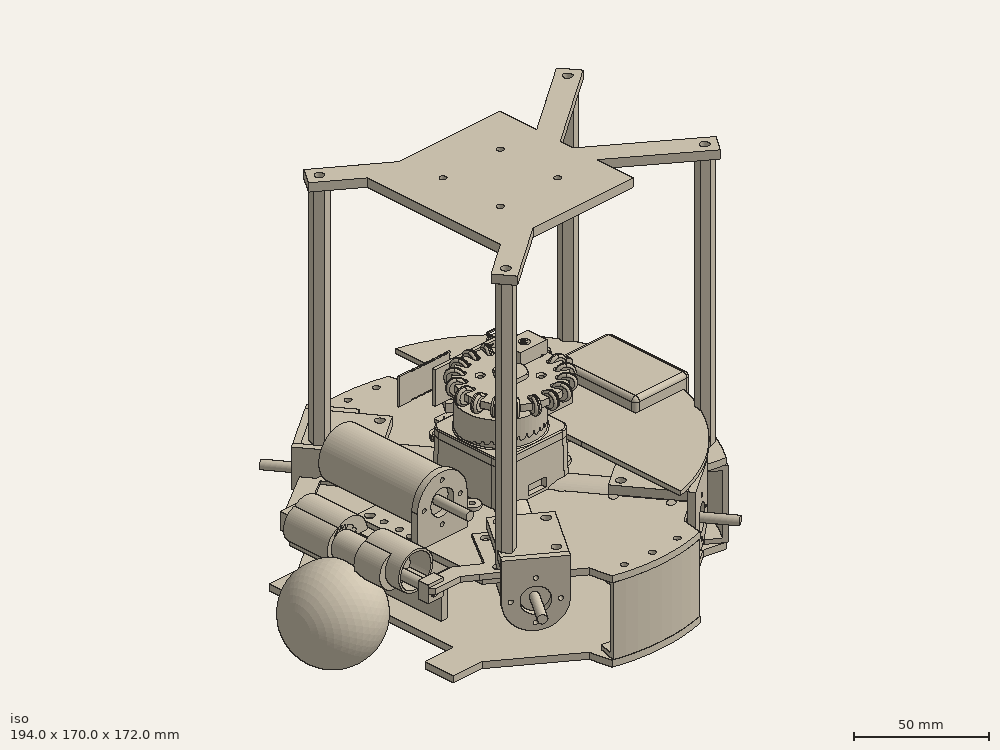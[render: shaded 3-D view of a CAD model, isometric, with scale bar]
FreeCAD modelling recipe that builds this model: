
FCSTD DOCUMENT  (FreeCAD 1.0R39109 (Git))
Label: SN_model_2025
License: All rights reserved
LicenseURL: https://en.wikipedia.org/wiki/All_rights_reserved
objects: Part::Feature×311, Sketcher::SketchObject×77, App::Part×52, PartDesign::Pad×50, PartDesign::Pocket×47, PartDesign::Body×32, PartDesign::SubShapeBinder×27, PartDesign::PolarPattern×11, PartDesign::Revolution×4, Part::FeaturePython×2, Part::Sphere×1, PartDesign::Fillet×1, Part::Cylinder×1, Part::Cut×1
note: 857 computed .brp shape members not serialized (recipe doc carries the construction recipe); baked Part::Feature solids carry a one-line shape summary decoded from their .brp

FEATURE [Sketcher::SketchObject] Sketch
  ArcFitTolerance = 0
  AttachmentSupport = -> [XY_Plane008]
  FullyConstrained = true
  MakeInternals = false
  MapMode = 5
  sketch-geometry (1):
    g0: Circle CenterX=0 CenterY=0 CenterZ=0 NormalX=0 NormalY=0 NormalZ=1 AngleXU=0 Radius=85
  constraints (2):
    c: Coincident(g0,g-1)
    c: Diameter(g0) = 170
FEATURE [Sketcher::SketchObject] Sketch005
  ArcFitTolerance = 0
  AttachmentSupport = -> [XZ_Plane009]
  FullyConstrained = true
  MakeInternals = false
  MapMode = 5
  Placement = pos=(0,0,0) rot=(1,0,0;1.5708rad)
  sketch-geometry (6):
    g0: ArcOfHyperbola CenterX=0 CenterY=94.5 CenterZ=0 NormalX=0 NormalY=0 NormalZ=1 MajorRadius=17.5 MinorRadius=15.6742 AngleXU=1.5708 StartAngle=0 EndAngle=1.02375
    g1: LineSegment [constr] StartX=5e-16 StartY=112 StartZ=0 EndX=-5e-16 EndY=77 EndZ=0
    g2: LineSegment [constr] StartX=-15.6742 StartY=112 StartZ=0 EndX=15.6742 EndY=112 EndZ=0
    g3: GeomPoint [constr] X=2.6e-15 Y=117.993 Z=0
    g4: LineSegment StartX=-19 StartY=122 StartZ=0 EndX=0 EndY=122 EndZ=0
    g5: LineSegment StartX=0 StartY=112 StartZ=0 EndX=0 EndY=122 EndZ=0
  constraints (15):
    c: InternalAlignment(g1,g0)
    c: InternalAlignment(g2,g0)
    c: InternalAlignment(g3,g0)
    c: Horizontal(g2)
    c: PointOnObject(g0,g-2)
    c: PointOnObject(g0,g-2)
    c: DistanceY(g0,g0) = 10
    c: DistanceX(g0,g0) = 19
    c: DistanceY(g1,g0) = 35
    c: Coincident(g4,g0)
    c: Coincident(g5,g0)
    c: Coincident(g5,g4)
    c: Vertical(g5)
    c: Horizontal(g4)
    c: DistanceY(g-1,g0) = 112
FEATURE [PartDesign::Pad] Pad  label="Structural layer"
  Direction = (0,0,1)
  Length = 3
  Length2 = 10
  Profile = -> Sketch
  ReferenceAxis = -> Sketch [N_Axis]
  Suppressed = false
  Type = 0
FEATURE [Sketcher::SketchObject] Sketch001
  ArcFitTolerance = 0
  AttachmentSupport = -> [Pad]
  ExternalGeometry = -> [Pad]
  FullyConstrained = false
  MakeInternals = false
  MapMode = 5
  Placement = pos=(0,0,3) rot=(0,0,1;0rad)
  sketch-geometry (7):
    g0: LineSegment StartX=-10.6686 StartY=100.741 StartZ=0 EndX=44.4806 EndY=91.0164 EndZ=0
    g1: LineSegment StartX=44.4806 StartY=91.0164 StartZ=0 EndX=41.5109 EndY=74.1744 EndZ=0
    g2: LineSegment StartX=32.942 StartY=68.1744 StartZ=0 EndX=-7.63834 EndY=75.3298 EndZ=0
    g3: LineSegment StartX=-13.6383 StartY=83.8987 StartZ=0 EndX=-10.6686 EndY=100.741 EndZ=0
    g4: LineSegment StartX=32.942 StartY=68.1744 StartZ=0 EndX=41.5109 EndY=74.1744 EndZ=0
    g5: LineSegment StartX=-13.6383 StartY=83.8987 StartZ=0 EndX=-7.63834 EndY=75.3298 EndZ=0
    g6: LineSegment [constr] StartX=-98.5042 StartY=90.5189 StartZ=0 EndX=89.0462 EndY=57.4487 EndZ=0
  constraints (18):
    c: Coincident(g0,g1)
    c: Coincident(g3,g0)
    c: Coincident(g4,g2)
    c: Coincident(g4,g1)
    c: Coincident(g5,g3)
    c: Coincident(g5,g2)
    c: Angle(g4,g2) = 2.35619
    c: Angle(g2,g5) = 2.35619
    c: DistanceX(g3,g2) = 6
    c: Angle(g6,g-1) = 0.174533
    c: Parallel(g2,g6)
    c: Parallel(g0,g2)
    c: Perpendicular(g6,g1)
    c: Equal(g1,g3)
    c: Parallel(g1,g3)
    c: PointOnObject(g3,g-3)
    c: PointOnObject(g1,g-3)
    c: Distance(g0) = 56
FEATURE [PartDesign::Pocket] Pocket
  BaseFeature = -> Pad
  Direction = (0,0,-1)
  Length = 5
  Length2 = 5
  Profile = -> Sketch001
  ReferenceAxis = -> Sketch001 [N_Axis]
  Suppressed = false
  Type = 1
FEATURE [PartDesign::PolarPattern] PolarPattern
  Angle = 110
  Axis = -> Sketch001 [N_Axis]
  BaseFeature = -> Pocket
  Mode = 0
  Occurrences = 2
  Offset = 120
  Originals = -> [Pocket]
  Suppressed = false
  TransformMode = 0
FEATURE [PartDesign::Revolution] Revolution
  Angle = 360
  Angle2 = 60
  Axis = (0,2e-16,1)
  Base = (0,0,0)
  Placement = pos=(0,0,0) rot=(1,0,0;1.5708rad)
  Profile = -> Sketch005
  ReferenceAxis = -> Sketch005 [V_Axis]
  Suppressed = false
  Type = 0
FEATURE [Sketcher::SketchObject] Sketch015
  ArcFitTolerance = 0
  AttachmentSupport = -> [PolarPattern]
  FullyConstrained = true
  MakeInternals = false
  MapMode = 5
  Placement = pos=(0,0,3) rot=(0,0,1;0rad)
  sketch-geometry (4):
    g0: LineSegment StartX=-111 StartY=31 StartZ=0 EndX=-31 EndY=111 EndZ=0
    g1: LineSegment StartX=-31 StartY=111 StartZ=0 EndX=-1 EndY=81 EndZ=0
    g2: LineSegment StartX=-1 StartY=81 StartZ=0 EndX=-81 EndY=1 EndZ=0
    g3: LineSegment StartX=-81 StartY=1 StartZ=0 EndX=-111 EndY=31 EndZ=0
  constraints (12):
    c: Coincident(g0,g1)
    c: Coincident(g1,g2)
    c: Coincident(g2,g3)
    c: Coincident(g3,g0)
    c: Equal(g3,g1)
    c: Equal(g0,g2)
    c: Angle(g3,g0) = 1.5708
    c: DistanceX(g2,g-1) = 81
    c: DistanceY(g-1,g1) = 81
    c: DistanceX(g0,g1) = 30
    c: DistanceX(g2,g1) = 80
    c: Angle(g-1,g2) = 0.785398
FEATURE [PartDesign::Pocket] Pocket004
  BaseFeature = -> PolarPattern
  Direction = (0,0,-1)
  Length = 5
  Length2 = 5
  Profile = -> Sketch015
  ReferenceAxis = -> Sketch015 [N_Axis]
  Suppressed = false
  Type = 1
FEATURE [Sketcher::SketchObject] Sketch016
  ArcFitTolerance = 0
  AttachmentSupport = -> [XZ_Plane016]
  FullyConstrained = true
  MakeInternals = false
  MapMode = 5
  Placement = pos=(0,0,0) rot=(1,0,0;1.5708rad)
  sketch-geometry (8):
    g0: LineSegment StartX=-88 StartY=-1 StartZ=0 EndX=-79 EndY=-1 EndZ=0
    g1: LineSegment StartX=-79 StartY=-34 StartZ=0 EndX=-88 EndY=-34 EndZ=0
    g2: LineSegment StartX=-88 StartY=-34 StartZ=0 EndX=-88 EndY=-1 EndZ=0
    g3: LineSegment StartX=-79 StartY=-1 StartZ=0 EndX=-79 EndY=-3 EndZ=0
    g4: LineSegment StartX=-79 StartY=-3 StartZ=0 EndX=-86 EndY=-3 EndZ=0
    g5: LineSegment StartX=-86 StartY=-3 StartZ=0 EndX=-86 EndY=-32 EndZ=0
    g6: LineSegment StartX=-86 StartY=-32 StartZ=0 EndX=-79 EndY=-32 EndZ=0
    g7: LineSegment StartX=-79 StartY=-32 StartZ=0 EndX=-79 EndY=-34 EndZ=0
  constraints (24):
    c: Coincident(g1,g2)
    c: Coincident(g2,g0)
    c: Horizontal(g0)
    c: Horizontal(g1)
    c: Vertical(g2)
    c: DistanceY(g1,g0) = 33
    c: DistanceX(g1,g1) = 9
    c: DistanceX(g0,g-1) = 88
    c: DistanceY(g1,g-1) = 34
    c: Equal(g1,g0)
    c: Coincident(g3,g0)
    c: Vertical(g3)
    c: Coincident(g4,g3)
    c: Horizontal(g4)
    c: Coincident(g5,g4)
    c: Vertical(g5)
    c: Coincident(g6,g5)
    c: Horizontal(g6)
    c: Coincident(g7,g6)
    c: Coincident(g7,g1)
    c: Vertical(g7)
    c: Equal(g3,g7)
    c: DistanceY(g3,g3) = 2
    c: DistanceX(g0,g4) = 2
FEATURE [PartDesign::Revolution] Revolution001
  Angle = 30
  Angle2 = 60
  Axis = (1e-16,1e-16,1)
  Base = (0,0,0)
  Midplane = true
  Placement = pos=(0,0,0) rot=(1,0,0;1.5708rad)
  Profile = -> Sketch016
  ReferenceAxis = -> Z_Axis016
  Reversed = true
  Suppressed = false
  Type = 0
FEATURE [Part::Feature] Part__Feature268  label="OmniBase_Predeterminado004"
  Placement = pos=(4.80373,-0.638646,40.5) rot=(0,0,1;0rad)
  shape: bbox 44 x 43.9 x 9 mm, 104 faces (baked)
FEATURE [Part::Feature] Part__Feature269  label="Roller_Predeterminado072"
  Placement = pos=(4.80373,20.3614,41.6192) rot=(0,0,1;0rad)
  shape: bbox 2.6 x 8.659 x 8.659 mm, 10 faces (baked)
FEATURE [Part::Feature] Part__Feature270  label="Roller_Predeterminado073"
  Placement = pos=(-2.3787,19.0949,41.6192) rot=(0,0,1;0.349066rad)
  shape: bbox 4.664 x 8.342 x 8.659 mm, 10 faces (baked)
FEATURE [Part::Feature] Part__Feature271  label="Roller_Predeterminado074"
  Placement = pos=(-8.69481,15.4483,41.6192) rot=(0,0,1;0.698132rad)
  shape: bbox 6.71 x 7.451 x 8.659 mm, 10 faces (baked)
FEATURE [Part::Feature] Part__Feature272  label="Roller_Predeterminado075"
  Placement = pos=(-13.3828,9.86135,41.6192) rot=(0,0,1;1.0472rad)
  shape: bbox 7.965 x 5.765 x 8.659 mm, 10 faces (baked)
FEATURE [Part::Feature] Part__Feature273  label="Roller_Predeterminado076"
  Placement = pos=(-15.8772,3.00797,41.6192) rot=(0,0,1;1.39626rad)
  shape: bbox 8.632 x 3.688 x 8.659 mm, 10 faces (baked)
FEATURE [Part::Feature] Part__Feature274  label="Roller_Predeterminado077"
  Placement = pos=(-15.8772,-4.28526,41.6192) rot=(0,0,1;1.74533rad)
  shape: bbox 8.632 x 3.688 x 8.659 mm, 10 faces (baked)
FEATURE [Part::Feature] Part__Feature275  label="Roller_Predeterminado078"
  Placement = pos=(-13.3828,-11.1386,41.6192) rot=(0,0,1;2.0944rad)
  shape: bbox 7.965 x 5.765 x 8.659 mm, 10 faces (baked)
FEATURE [Part::Feature] Part__Feature276  label="Roller_Predeterminado079"
  Placement = pos=(-8.69481,-16.7256,41.6192) rot=(0,0,1;2.44346rad)
  shape: bbox 6.71 x 7.451 x 8.659 mm, 10 faces (baked)
FEATURE [Part::Feature] Part__Feature277  label="Roller_Predeterminado080"
  Placement = pos=(-2.3787,-20.3722,41.6192) rot=(0,0,1;2.79253rad)
  shape: bbox 4.664 x 8.342 x 8.659 mm, 10 faces (baked)
FEATURE [Part::Feature] Part__Feature278  label="Roller_Predeterminado081"
  Placement = pos=(4.80373,-21.6386,41.6192) rot=(0,0,1;3.14159rad)
  shape: bbox 2.6 x 8.659 x 8.659 mm, 10 faces (baked)
FEATURE [Part::Feature] Part__Feature279  label="Roller_Predeterminado082"
  Placement = pos=(11.9862,-20.3722,41.6192) rot=(0,0,1;3.49066rad)
  shape: bbox 4.664 x 8.342 x 8.659 mm, 10 faces (baked)
FEATURE [Part::Feature] Part__Feature280  label="Roller_Predeterminado083"
  Placement = pos=(18.3023,-16.7256,41.6192) rot=(0,0,1;3.83972rad)
  shape: bbox 6.71 x 7.451 x 8.659 mm, 10 faces (baked)
FEATURE [Part::Feature] Part__Feature281  label="Roller_Predeterminado084"
  Placement = pos=(22.9903,-11.1386,41.6192) rot=(0,0,-1;2.0944rad)
  shape: bbox 7.965 x 5.765 x 8.659 mm, 10 faces (baked)
FEATURE [Part::Feature] Part__Feature282  label="Roller_Predeterminado085"
  Placement = pos=(25.4847,-4.28526,41.6192) rot=(0,0,-1;1.74533rad)
  shape: bbox 8.632 x 3.688 x 8.659 mm, 10 faces (baked)
FEATURE [Part::Feature] Part__Feature283  label="Roller_Predeterminado086"
  Placement = pos=(25.4847,3.00797,41.6192) rot=(0,0,-1;1.39626rad)
  shape: bbox 8.632 x 3.688 x 8.659 mm, 10 faces (baked)
FEATURE [Part::Feature] Part__Feature284  label="Roller_Predeterminado087"
  Placement = pos=(22.9903,9.86135,41.6192) rot=(0,0,-1;1.0472rad)
  shape: bbox 7.965 x 5.765 x 8.659 mm, 10 faces (baked)
FEATURE [Part::Feature] Part__Feature285  label="Roller_Predeterminado088"
  Placement = pos=(18.3023,15.4483,41.6192) rot=(0,0,-1;0.698132rad)
  shape: bbox 6.71 x 7.451 x 8.659 mm, 10 faces (baked)
FEATURE [Part::Feature] Part__Feature286  label="Roller_Predeterminado089"
  Placement = pos=(11.9862,19.0949,41.6192) rot=(0,0,-1;0.349066rad)
  shape: bbox 4.664 x 8.342 x 8.659 mm, 10 faces (baked)
FEATURE [Part::Feature] Part__Feature287  label="Nut_Predeterminado004"
  Placement = pos=(4.80373,-0.638646,43.5) rot=(0,0,1;1.0472rad)
  shape: bbox 13.86 x 12.93 x 2 mm, 24 faces (baked)
FEATURE [App::Part] OmniWheel054  label="OmniWheel 1"
  Group = -> [Part__Feature268,Part__Feature269,Part__Feature270,Part__Feature271,Part__Feature272,Part__Feature273,Part__Feature274,Part__Feature275,Part__Feature276,Part__Feature277,Part__Feature278,Part__Feature279,Part__Feature280,Part__Feature281,Part__Feature282,Part__Feature283,Part__Feature284,Part__Feature285,Part__Feature286,Part__Feature287]
  Origin = -> Origin019
  Placement = pos=(-23.8855,35.1581,-6.8) rot=(-0.419215,-0.805305,-0.419215;1.78566rad)
FEATURE [Sketcher::SketchObject] Sketch023
  ArcFitTolerance = 0
  AttachmentSupport = -> [XY_Plane024]
  FullyConstrained = true
  MakeInternals = false
  MapMode = 5
  sketch-geometry (9):
    g0: Circle CenterX=0 CenterY=0 CenterZ=0 NormalX=0 NormalY=0 NormalZ=1 AngleXU=0 Radius=20
    g1: LineSegment StartX=27.7128 StartY=-4 StartZ=0 EndX=35.7128 EndY=-4 EndZ=0
    g2: LineSegment StartX=35.7128 StartY=-4 StartZ=0 EndX=35.7128 EndY=4 EndZ=0
    g3: LineSegment StartX=35.7128 StartY=4 StartZ=0 EndX=27.7128 EndY=4 EndZ=0
    g4: LineSegment StartX=-27.7128 StartY=-4 StartZ=0 EndX=-35.7128 EndY=-4 EndZ=0
    g5: LineSegment StartX=-35.7128 StartY=-4 StartZ=0 EndX=-35.7128 EndY=4 EndZ=0
    g6: LineSegment StartX=-35.7128 StartY=4 StartZ=0 EndX=-27.7128 EndY=4 EndZ=0
    g7: ArcOfCircle CenterX=0 CenterY=0 CenterZ=0 NormalX=0 NormalY=0 NormalZ=1 AngleXU=0 Radius=28 StartAngle=0.143348 EndAngle=2.99825
    g8: ArcOfCircle CenterX=0 CenterY=0 CenterZ=0 NormalX=0 NormalY=0 NormalZ=1 AngleXU=0 Radius=28 StartAngle=3.28494 EndAngle=6.13984
  constraints (25):
    c: Coincident(g0,g-1)
    c: Diameter(g0) = 40
    c: Horizontal(g1)
    c: Coincident(g2,g1)
    c: Coincident(g3,g2)
    c: Horizontal(g3)
    c: Horizontal(g4)
    c: Coincident(g5,g4)
    c: Vertical(g5)
    c: Coincident(g6,g5)
    c: Horizontal(g6)
    c: Coincident(g7,g0)
    c: Coincident(g7,g6)
    c: Coincident(g7,g3)
    c: Coincident(g8,g0)
    c: Coincident(g8,g4)
    c: Coincident(g8,g1)
    c: Diameter(g7) = 56
    c: Diameter(g8) = 56
    c: Symmetric(g1,g2,g-1)
    c: Equal(g5,g2)
    c: Equal(g6,g3)
    c: Equal(g4,g1)
    c: DistanceY(g2,g2) = 8
    c: DistanceX(g6,g6) = 8
FEATURE [PartDesign::Pad] Pad007
  Direction = (0,0,1)
  Length = 3
  Length2 = 10
  Profile = -> Sketch023
  ReferenceAxis = -> Sketch023 [N_Axis]
  Suppressed = false
  Type = 0
FEATURE [Sketcher::SketchObject] Sketch025
  ArcFitTolerance = 0
  AttachmentSupport = -> [XY_Plane026]
  FullyConstrained = true
  MakeInternals = false
  MapMode = 5
  sketch-geometry (2):
    g0: Circle CenterX=0 CenterY=0 CenterZ=0 NormalX=0 NormalY=0 NormalZ=1 AngleXU=0 Radius=90
    g1: Circle CenterX=0 CenterY=0 CenterZ=0 NormalX=0 NormalY=0 NormalZ=1 AngleXU=0 Radius=95
  constraints (4):
    c: Diameter(g0) = 180
    c: Coincident(g1,g-1)
    c: Diameter(g1) = 190
    c: Coincident(g0,g-1)
FEATURE [PartDesign::Pad] Pad008
  Direction = (0,0,1)
  Length = 180
  Length2 = 10
  Profile = -> Sketch025
  ReferenceAxis = -> Sketch025 [N_Axis]
  Suppressed = false
  Type = 0
FEATURE [PartDesign::Body] Body008  label="Cylinder"
  AllowCompound = false
  Group = -> [Sketch025,Pad008]
  Origin = -> Origin026
  Placement = pos=(0,0,-44) rot=(0,0,1;0rad)
  Tip = -> Pad008
FEATURE [Sketcher::SketchObject] Sketch061
  ArcFitTolerance = 0
  FullyConstrained = true
  MakeInternals = false
  MapMode = 5
  Placement = pos=(0,0,2) rot=(0,0,1;0rad)
  sketch-geometry (1):
    g0: Circle CenterX=0 CenterY=0 CenterZ=0 NormalX=0 NormalY=0 NormalZ=1 AngleXU=0 Radius=12.5
  constraints (2):
    c: Coincident(g0,g-1)
    c: Diameter(g0) = 25
FEATURE [PartDesign::Pocket] Pocket019
  BaseFeature = -> Pocket004
  Direction = (0,0,-1)
  Length = 5
  Length2 = 5
  Profile = -> Sketch061
  ReferenceAxis = -> Sketch061 [N_Axis]
  Suppressed = false
  Type = 4
FEATURE [Part::Feature] Part__Feature439  label="114-00841-68--3DModel-STEP-56544 v1"
  Placement = pos=(24.0935,-0.00012972,0.814608) rot=(0.57735,0.57735,0.57735;2.0944rad)
  shape: bbox 11.35 x 11.95 x 1.68 mm, 239 faces (baked)
FEATURE [Part::Feature] Part__Feature453  label="MIMXRT1052CVJ5B v1"
  Placement = pos=(1.30183,-0.0809243,0.815) rot=(0,0.707107,0.707107;3.14159rad)
  shape: bbox 12 x 12 x 1.27 mm, 6 faces (baked)
FEATURE [App::Part] MIMXRT1052CVJ5B_v1  label="MIMXRT1052CVJ5B v198"
  Group = -> [Part__Feature453]
  Origin = -> Origin053
FEATURE [Part::Feature] Part__Feature589  label="MicroUSB Molex 473460001 v1"
  Placement = pos=(-28.9499,0.13174,2.07033) rot=(0.57735,-0.57735,-0.57735;2.0944rad)
  shape: bbox 5.43 x 7.98 x 2.94 mm, 406 faces (baked)
FEATURE [Part::Feature] Part__Feature590  label="COMPOUND"
  shape: bbox 2.54 x 2.54 x 2.799 mm, 22 faces, 0 solids (baked)
FEATURE [Part::Feature] Part__Feature591  label="COMPOUND001"
  shape: bbox 2.54 x 2.54 x 2.799 mm, 22 faces, 0 solids (baked)
FEATURE [Part::Feature] Part__Feature592  label="COMPOUND002"
  shape: bbox 2.54 x 2.54 x 2.799 mm, 23 faces, 0 solids (baked)
FEATURE [Part::Feature] Part__Feature593  label="COMPOUND003"
  shape: bbox 2.54 x 2.54 x 2.799 mm, 22 faces, 0 solids (baked)
FEATURE [Part::Feature] Part__Feature594  label="COMPOUND004"
  shape: bbox 2.54 x 2.54 x 2.799 mm, 22 faces, 0 solids (baked)
FEATURE [Part::Feature] Part__Feature595  label="COMPOUND005"
  shape: bbox 2.54 x 2.54 x 2.799 mm, 23 faces, 0 solids (baked)
FEATURE [App::Part] COMPOUND  label="COMPOUND006"
  Group = -> [Part__Feature590,Part__Feature591,Part__Feature592,Part__Feature593,Part__Feature594,Part__Feature595]
  Origin = -> Origin055
FEATURE [Part::Feature] Part__Feature596  label="COMPOUND007"
  shape: bbox 0.6304 x 0.63 x 12.7 mm, 14 faces (baked)
FEATURE [Part::Feature] Part__Feature597  label="COMPOUND008"
  shape: bbox 0.6304 x 0.63 x 12.7 mm, 14 faces (baked)
FEATURE [Part::Feature] Part__Feature598  label="COMPOUND009"
  shape: bbox 0.6304 x 0.63 x 12.7 mm, 14 faces (baked)
FEATURE [Part::Feature] Part__Feature599  label="COMPOUND010"
  shape: bbox 0.6304 x 0.63 x 12.7 mm, 14 faces (baked)
FEATURE [Part::Feature] Part__Feature600  label="COMPOUND011"
  shape: bbox 0.6304 x 0.63 x 12.7 mm, 14 faces (baked)
FEATURE [Part::Feature] Part__Feature601  label="COMPOUND012"
  shape: bbox 0.6304 x 0.63 x 12.7 mm, 14 faces (baked)
FEATURE [App::Part] COMPOUND001  label="COMPOUND013"
  Group = -> [Part__Feature596,Part__Feature597,Part__Feature598,Part__Feature599,Part__Feature600,Part__Feature601]
  Origin = -> Origin056
FEATURE [App::Part] Pin_Header_1x6_TH_Pitch_2_54mm_v1  label="Pin Header 1x6 TH Pitch 2.54mm v1"
  Group = -> [COMPOUND,COMPOUND001]
  Origin = -> Origin054
  Placement = pos=(-16.51,-7.62,-0.814) rot=(0,1,0;3.14159rad)
FEATURE [Part::Feature] Part__Feature602  label="COMPOUND014"
  shape: bbox 2.54 x 2.54 x 2.799 mm, 22 faces, 0 solids (baked)
FEATURE [Part::Feature] Part__Feature603  label="COMPOUND015"
  shape: bbox 2.54 x 2.54 x 2.799 mm, 22 faces, 0 solids (baked)
FEATURE [Part::Feature] Part__Feature604  label="COMPOUND016"
  shape: bbox 2.54 x 2.54 x 2.799 mm, 23 faces, 0 solids (baked)
FEATURE [Part::Feature] Part__Feature605  label="COMPOUND017"
  shape: bbox 2.54 x 2.54 x 2.799 mm, 22 faces, 0 solids (baked)
FEATURE [Part::Feature] Part__Feature606  label="COMPOUND018"
  shape: bbox 2.54 x 2.54 x 2.799 mm, 22 faces, 0 solids (baked)
FEATURE [Part::Feature] Part__Feature607  label="COMPOUND019"
  shape: bbox 2.54 x 2.54 x 2.799 mm, 23 faces, 0 solids (baked)
FEATURE [App::Part] COMPOUND002  label="COMPOUND020"
  Group = -> [Part__Feature602,Part__Feature603,Part__Feature604,Part__Feature605,Part__Feature606,Part__Feature607]
  Origin = -> Origin058
FEATURE [Part::Feature] Part__Feature608  label="COMPOUND021"
  shape: bbox 0.6304 x 0.63 x 12.7 mm, 14 faces (baked)
FEATURE [Part::Feature] Part__Feature609  label="COMPOUND022"
  shape: bbox 0.6304 x 0.63 x 12.7 mm, 14 faces (baked)
FEATURE [Part::Feature] Part__Feature610  label="COMPOUND023"
  shape: bbox 0.6304 x 0.63 x 12.7 mm, 14 faces (baked)
FEATURE [Part::Feature] Part__Feature611  label="COMPOUND024"
  shape: bbox 0.6304 x 0.63 x 12.7 mm, 14 faces (baked)
FEATURE [Part::Feature] Part__Feature612  label="COMPOUND025"
  shape: bbox 0.6304 x 0.63 x 12.7 mm, 14 faces (baked)
FEATURE [Part::Feature] Part__Feature613  label="COMPOUND026"
  shape: bbox 0.6304 x 0.63 x 12.7 mm, 14 faces (baked)
FEATURE [App::Part] COMPOUND003  label="COMPOUND027"
  Group = -> [Part__Feature608,Part__Feature609,Part__Feature610,Part__Feature611,Part__Feature612,Part__Feature613]
  Origin = -> Origin059
FEATURE [App::Part] Pin_Header_1x6_TH_Pitch_2_54mm_v002  label="Pin Header 1x6 TH Pitch 2.54mm v002"
  Group = -> [COMPOUND002,COMPOUND003]
  Origin = -> Origin057
  Placement = pos=(-1.27,-7.62,-0.814) rot=(0,1,0;3.14159rad)
FEATURE [Part::Feature] Part__Feature614  label="COMPOUND028"
  shape: bbox 2.54 x 2.54 x 2.799 mm, 22 faces, 0 solids (baked)
FEATURE [Part::Feature] Part__Feature615  label="COMPOUND029"
  shape: bbox 2.54 x 2.54 x 2.799 mm, 22 faces, 0 solids (baked)
FEATURE [Part::Feature] Part__Feature616  label="COMPOUND030"
  shape: bbox 2.54 x 2.54 x 2.799 mm, 23 faces, 0 solids (baked)
FEATURE [Part::Feature] Part__Feature617  label="COMPOUND031"
  shape: bbox 2.54 x 2.54 x 2.799 mm, 22 faces, 0 solids (baked)
FEATURE [Part::Feature] Part__Feature618  label="COMPOUND032"
  shape: bbox 2.54 x 2.54 x 2.799 mm, 22 faces, 0 solids (baked)
FEATURE [Part::Feature] Part__Feature619  label="COMPOUND033"
  shape: bbox 2.54 x 2.54 x 2.799 mm, 23 faces, 0 solids (baked)
FEATURE [App::Part] COMPOUND004  label="COMPOUND034"
  Group = -> [Part__Feature614,Part__Feature615,Part__Feature616,Part__Feature617,Part__Feature618,Part__Feature619]
  Origin = -> Origin060
FEATURE [Part::Feature] Part__Feature620  label="COMPOUND035"
  shape: bbox 0.6304 x 0.63 x 12.7 mm, 14 faces (baked)
FEATURE [Part::Feature] Part__Feature621  label="COMPOUND036"
  shape: bbox 0.6304 x 0.63 x 12.7 mm, 14 faces (baked)
FEATURE [Part::Feature] Part__Feature622  label="COMPOUND037"
  shape: bbox 0.6304 x 0.63 x 12.7 mm, 14 faces (baked)
FEATURE [Part::Feature] Part__Feature623  label="COMPOUND038"
  shape: bbox 0.6304 x 0.63 x 12.7 mm, 14 faces (baked)
FEATURE [Part::Feature] Part__Feature624  label="COMPOUND039"
  shape: bbox 0.6304 x 0.63 x 12.7 mm, 14 faces (baked)
FEATURE [Part::Feature] Part__Feature625  label="COMPOUND040"
  shape: bbox 0.6304 x 0.63 x 12.7 mm, 14 faces (baked)
FEATURE [App::Part] COMPOUND005  label="COMPOUND041"
  Group = -> [Part__Feature620,Part__Feature621,Part__Feature622,Part__Feature623,Part__Feature624,Part__Feature625]
  Origin = -> Origin010
FEATURE [App::Part] Pin_Header_1x6_TH_Pitch_2_54mm_v003  label="Pin Header 1x6 TH Pitch 2.54mm v003"
  Group = -> [COMPOUND004,COMPOUND005]
  Origin = -> Origin011
  Placement = pos=(13.97,-7.62,-0.814) rot=(0,1,0;3.14159rad)
FEATURE [Part::Feature] Part__Feature626  label="COMPOUND042"
  shape: bbox 2.54 x 2.54 x 2.799 mm, 22 faces, 0 solids (baked)
FEATURE [Part::Feature] Part__Feature627  label="COMPOUND043"
  shape: bbox 2.54 x 2.54 x 2.799 mm, 22 faces, 0 solids (baked)
FEATURE [Part::Feature] Part__Feature628  label="COMPOUND044"
  shape: bbox 2.54 x 2.54 x 2.799 mm, 23 faces, 0 solids (baked)
FEATURE [Part::Feature] Part__Feature629  label="COMPOUND045"
  shape: bbox 2.54 x 2.54 x 2.799 mm, 22 faces, 0 solids (baked)
FEATURE [Part::Feature] Part__Feature630  label="COMPOUND046"
  shape: bbox 2.54 x 2.54 x 2.799 mm, 22 faces, 0 solids (baked)
FEATURE [Part::Feature] Part__Feature631  label="COMPOUND047"
  shape: bbox 2.54 x 2.54 x 2.799 mm, 23 faces, 0 solids (baked)
FEATURE [App::Part] COMPOUND006  label="COMPOUND048"
  Group = -> [Part__Feature626,Part__Feature627,Part__Feature628,Part__Feature629,Part__Feature630,Part__Feature631]
  Origin = -> Origin012
FEATURE [Part::Feature] Part__Feature632  label="COMPOUND049"
  shape: bbox 0.6304 x 0.63 x 12.7 mm, 14 faces (baked)
FEATURE [Part::Feature] Part__Feature633  label="COMPOUND050"
  shape: bbox 0.6304 x 0.63 x 12.7 mm, 14 faces (baked)
FEATURE [Part::Feature] Part__Feature634  label="COMPOUND051"
  shape: bbox 0.6304 x 0.63 x 12.7 mm, 14 faces (baked)
FEATURE [Part::Feature] Part__Feature635  label="COMPOUND052"
  shape: bbox 0.6304 x 0.63 x 12.7 mm, 14 faces (baked)
FEATURE [Part::Feature] Part__Feature636  label="COMPOUND053"
  shape: bbox 0.6304 x 0.63 x 12.7 mm, 14 faces (baked)
FEATURE [Part::Feature] Part__Feature637  label="COMPOUND054"
  shape: bbox 0.6304 x 0.63 x 12.7 mm, 14 faces (baked)
FEATURE [App::Part] COMPOUND007  label="COMPOUND055"
  Group = -> [Part__Feature632,Part__Feature633,Part__Feature634,Part__Feature635,Part__Feature636,Part__Feature637]
  Origin = -> Origin013
FEATURE [App::Part] Pin_Header_1x6_TH_Pitch_2_54mm_v004  label="Pin Header 1x6 TH Pitch 2.54mm v004"
  Group = -> [COMPOUND006,COMPOUND007]
  Origin = -> Origin014
  Placement = pos=(29.21,-7.62,-0.814) rot=(0,1,0;3.14159rad)
FEATURE [Part::Feature] Part__Feature638  label="COMPOUND056"
  shape: bbox 2.54 x 2.54 x 2.799 mm, 22 faces, 0 solids (baked)
FEATURE [Part::Feature] Part__Feature639  label="COMPOUND057"
  shape: bbox 2.54 x 2.54 x 2.799 mm, 22 faces, 0 solids (baked)
FEATURE [Part::Feature] Part__Feature640  label="COMPOUND058"
  shape: bbox 2.54 x 2.54 x 2.799 mm, 23 faces, 0 solids (baked)
FEATURE [Part::Feature] Part__Feature641  label="COMPOUND059"
  shape: bbox 2.54 x 2.54 x 2.799 mm, 22 faces, 0 solids (baked)
FEATURE [Part::Feature] Part__Feature642  label="COMPOUND060"
  shape: bbox 2.54 x 2.54 x 2.799 mm, 22 faces, 0 solids (baked)
FEATURE [Part::Feature] Part__Feature643  label="COMPOUND061"
  shape: bbox 2.54 x 2.54 x 2.799 mm, 23 faces, 0 solids (baked)
FEATURE [App::Part] COMPOUND008  label="COMPOUND062"
  Group = -> [Part__Feature638,Part__Feature639,Part__Feature640,Part__Feature641,Part__Feature642,Part__Feature643]
  Origin = -> Origin061
FEATURE [Part::Feature] Part__Feature644  label="COMPOUND063"
  shape: bbox 0.6304 x 0.63 x 12.7 mm, 14 faces (baked)
FEATURE [Part::Feature] Part__Feature645  label="COMPOUND064"
  shape: bbox 0.6304 x 0.63 x 12.7 mm, 14 faces (baked)
FEATURE [Part::Feature] Part__Feature646  label="COMPOUND065"
  shape: bbox 0.6304 x 0.63 x 12.7 mm, 14 faces (baked)
FEATURE [Part::Feature] Part__Feature647  label="COMPOUND066"
  shape: bbox 0.6304 x 0.63 x 12.7 mm, 14 faces (baked)
FEATURE [Part::Feature] Part__Feature648  label="COMPOUND067"
  shape: bbox 0.6304 x 0.63 x 12.7 mm, 14 faces (baked)
FEATURE [Part::Feature] Part__Feature649  label="COMPOUND068"
  shape: bbox 0.6304 x 0.63 x 12.7 mm, 14 faces (baked)
FEATURE [App::Part] COMPOUND009  label="COMPOUND069"
  Group = -> [Part__Feature644,Part__Feature645,Part__Feature646,Part__Feature647,Part__Feature648,Part__Feature649]
  Origin = -> Origin062
FEATURE [App::Part] Pin_Header_1x6_TH_Pitch_2_54mm_v1_Mirror_  label="Pin Header 1x6 TH Pitch 2.54mm v1(Mirror)"
  Group = -> [COMPOUND008,COMPOUND009]
  Origin = -> Origin017
  Placement = pos=(-16.51,7.62,-0.814) rot=(0,0,1;3.14159rad)
FEATURE [Part::Feature] Part__Feature650  label="COMPOUND070"
  shape: bbox 2.54 x 2.54 x 2.799 mm, 22 faces, 0 solids (baked)
FEATURE [Part::Feature] Part__Feature651  label="COMPOUND071"
  shape: bbox 2.54 x 2.54 x 2.799 mm, 22 faces, 0 solids (baked)
FEATURE [Part::Feature] Part__Feature652  label="COMPOUND072"
  shape: bbox 2.54 x 2.54 x 2.799 mm, 23 faces, 0 solids (baked)
FEATURE [Part::Feature] Part__Feature653  label="COMPOUND073"
  shape: bbox 2.54 x 2.54 x 2.799 mm, 22 faces, 0 solids (baked)
FEATURE [Part::Feature] Part__Feature654  label="COMPOUND074"
  shape: bbox 2.54 x 2.54 x 2.799 mm, 22 faces, 0 solids (baked)
FEATURE [Part::Feature] Part__Feature655  label="COMPOUND075"
  shape: bbox 2.54 x 2.54 x 2.799 mm, 23 faces, 0 solids (baked)
FEATURE [App::Part] COMPOUND010  label="COMPOUND076"
  Group = -> [Part__Feature650,Part__Feature651,Part__Feature652,Part__Feature653,Part__Feature654,Part__Feature655]
  Origin = -> Origin064
FEATURE [Part::Feature] Part__Feature656  label="COMPOUND077"
  shape: bbox 0.6304 x 0.63 x 12.7 mm, 14 faces (baked)
FEATURE [Part::Feature] Part__Feature657  label="COMPOUND078"
  shape: bbox 0.6304 x 0.63 x 12.7 mm, 14 faces (baked)
FEATURE [Part::Feature] Part__Feature658  label="COMPOUND079"
  shape: bbox 0.6304 x 0.63 x 12.7 mm, 14 faces (baked)
FEATURE [Part::Feature] Part__Feature659  label="COMPOUND080"
  shape: bbox 0.6304 x 0.63 x 12.7 mm, 14 faces (baked)
FEATURE [Part::Feature] Part__Feature660  label="COMPOUND081"
  shape: bbox 0.6304 x 0.63 x 12.7 mm, 14 faces (baked)
FEATURE [Part::Feature] Part__Feature661  label="COMPOUND082"
  shape: bbox 0.6304 x 0.63 x 12.7 mm, 14 faces (baked)
FEATURE [App::Part] COMPOUND011  label="COMPOUND083"
  Group = -> [Part__Feature656,Part__Feature657,Part__Feature658,Part__Feature659,Part__Feature660,Part__Feature661]
  Origin = -> Origin065
FEATURE [App::Part] Pin_Header_1x6_TH_Pitch_2_54mm_v1_Mirror_001  label="Pin Header 1x6 TH Pitch 2.54mm v1(Mirror)001"
  Group = -> [COMPOUND010,COMPOUND011]
  Origin = -> Origin063
  Placement = pos=(-1.27,7.62,-0.814) rot=(0,0,1;3.14159rad)
FEATURE [Part::Feature] Part__Feature662  label="COMPOUND084"
  shape: bbox 2.54 x 2.54 x 2.799 mm, 22 faces, 0 solids (baked)
FEATURE [Part::Feature] Part__Feature663  label="COMPOUND085"
  shape: bbox 2.54 x 2.54 x 2.799 mm, 22 faces, 0 solids (baked)
FEATURE [Part::Feature] Part__Feature664  label="COMPOUND086"
  shape: bbox 2.54 x 2.54 x 2.799 mm, 23 faces, 0 solids (baked)
FEATURE [Part::Feature] Part__Feature665  label="COMPOUND087"
  shape: bbox 2.54 x 2.54 x 2.799 mm, 22 faces, 0 solids (baked)
FEATURE [Part::Feature] Part__Feature666  label="COMPOUND088"
  shape: bbox 2.54 x 2.54 x 2.799 mm, 22 faces, 0 solids (baked)
FEATURE [Part::Feature] Part__Feature667  label="COMPOUND089"
  shape: bbox 2.54 x 2.54 x 2.799 mm, 23 faces, 0 solids (baked)
FEATURE [App::Part] COMPOUND012  label="COMPOUND090"
  Group = -> [Part__Feature662,Part__Feature663,Part__Feature664,Part__Feature665,Part__Feature666,Part__Feature667]
  Origin = -> Origin067
FEATURE [Part::Feature] Part__Feature668  label="COMPOUND091"
  shape: bbox 0.6304 x 0.63 x 12.7 mm, 14 faces (baked)
FEATURE [Part::Feature] Part__Feature669  label="COMPOUND092"
  shape: bbox 0.6304 x 0.63 x 12.7 mm, 14 faces (baked)
FEATURE [Part::Feature] Part__Feature670  label="COMPOUND093"
  shape: bbox 0.6304 x 0.63 x 12.7 mm, 14 faces (baked)
FEATURE [Part::Feature] Part__Feature671  label="COMPOUND094"
  shape: bbox 0.6304 x 0.63 x 12.7 mm, 14 faces (baked)
FEATURE [Part::Feature] Part__Feature672  label="COMPOUND095"
  shape: bbox 0.6304 x 0.63 x 12.7 mm, 14 faces (baked)
FEATURE [Part::Feature] Part__Feature673  label="COMPOUND096"
  shape: bbox 0.6304 x 0.63 x 12.7 mm, 14 faces (baked)
FEATURE [App::Part] COMPOUND013  label="COMPOUND097"
  Group = -> [Part__Feature668,Part__Feature669,Part__Feature670,Part__Feature671,Part__Feature672,Part__Feature673]
  Origin = -> Origin022
FEATURE [App::Part] Pin_Header_1x6_TH_Pitch_2_54mm_v1_Mirror_002  label="Pin Header 1x6 TH Pitch 2.54mm v1(Mirror)002"
  Group = -> [COMPOUND012,COMPOUND013]
  Origin = -> Origin066
  Placement = pos=(13.97,7.62,-0.814) rot=(0,0,1;3.14159rad)
FEATURE [Part::Feature] Part__Feature674  label="COMPOUND098"
  shape: bbox 2.54 x 2.54 x 2.799 mm, 22 faces, 0 solids (baked)
FEATURE [Part::Feature] Part__Feature675  label="COMPOUND099"
  shape: bbox 2.54 x 2.54 x 2.799 mm, 22 faces, 0 solids (baked)
FEATURE [Part::Feature] Part__Feature676  label="COMPOUND100"
  shape: bbox 2.54 x 2.54 x 2.799 mm, 23 faces, 0 solids (baked)
FEATURE [Part::Feature] Part__Feature677  label="COMPOUND101"
  shape: bbox 2.54 x 2.54 x 2.799 mm, 22 faces, 0 solids (baked)
FEATURE [Part::Feature] Part__Feature678  label="COMPOUND102"
  shape: bbox 2.54 x 2.54 x 2.799 mm, 22 faces, 0 solids (baked)
FEATURE [Part::Feature] Part__Feature679  label="COMPOUND103"
  shape: bbox 2.54 x 2.54 x 2.799 mm, 23 faces, 0 solids (baked)
FEATURE [App::Part] COMPOUND014  label="COMPOUND104"
  Group = -> [Part__Feature674,Part__Feature675,Part__Feature676,Part__Feature677,Part__Feature678,Part__Feature679]
  Origin = -> Origin069
FEATURE [Part::Feature] Part__Feature680  label="COMPOUND105"
  shape: bbox 0.6304 x 0.63 x 12.7 mm, 14 faces (baked)
FEATURE [Part::Feature] Part__Feature681  label="COMPOUND106"
  shape: bbox 0.6304 x 0.63 x 12.7 mm, 14 faces (baked)
FEATURE [Part::Feature] Part__Feature682  label="COMPOUND107"
  shape: bbox 0.6304 x 0.63 x 12.7 mm, 14 faces (baked)
FEATURE [Part::Feature] Part__Feature683  label="COMPOUND108"
  shape: bbox 0.6304 x 0.63 x 12.7 mm, 14 faces (baked)
FEATURE [Part::Feature] Part__Feature684  label="COMPOUND109"
  shape: bbox 0.6304 x 0.63 x 12.7 mm, 14 faces (baked)
FEATURE [Part::Feature] Part__Feature685  label="COMPOUND110"
  shape: bbox 0.6304 x 0.63 x 12.7 mm, 14 faces (baked)
FEATURE [App::Part] COMPOUND015  label="COMPOUND111"
  Group = -> [Part__Feature680,Part__Feature681,Part__Feature682,Part__Feature683,Part__Feature684,Part__Feature685]
  Origin = -> Origin070
FEATURE [App::Part] Pin_Header_1x6_TH_Pitch_2_54mm_v1_Mirror_003  label="Pin Header 1x6 TH Pitch 2.54mm v1(Mirror)003"
  Group = -> [COMPOUND014,COMPOUND015]
  Origin = -> Origin068
  Placement = pos=(29.21,7.62,-0.814) rot=(0,0,1;3.14159rad)
FEATURE [Part::Feature] Part__Feature716  label="PTS810 SJK 250 SMTR LFS v1"
  Placement = pos=(12.85,-0.068585,1.06859) rot=(1,0,0;1.5708rad)
  shape: bbox 4.2 x 3.2 x 2 mm, 27 faces (baked)
FEATURE [Part::Feature] Part__Feature717  label="PTS810 SJK 250 SMTR LFS v002"
  Placement = pos=(12.85,-0.068585,1.06859) rot=(1,0,0;1.5708rad)
  shape: bbox 3.181 x 2.381 x 1.2 mm, 10 faces (baked)
FEATURE [App::Part] PTS810_SJK_250_SMTR_LFS_v1  label="PTS810 SJK 250 SMTR LFS v007"
  Group = -> [Part__Feature716,Part__Feature717]
  Origin = -> Origin075
FEATURE [Part::Feature] Part__Feature722  label="COMPOUND136"
  shape: bbox 60.96 x 17.78 x 1.63 mm, 71 faces (baked)
FEATURE [App::Part] COMPOUND020  label="COMPOUND159"
  Group = -> [Part__Feature722]
  Origin = -> Origin076
FEATURE [Part::Sphere] Sphere  label="Ball"
  Angle1 = -90
  Angle2 = 90
  Angle3 = 360
  AttacherType = Attacher::AttachEngine3D
  Placement = pos=(-88,0,-21) rot=(0,1,0;1.5708rad)
  Radius = 21
FEATURE [Sketcher::SketchObject] Sketch065
  ArcFitTolerance = 0
  AttachmentSupport = -> [XY_Plane226]
  FullyConstrained = true
  MakeInternals = false
  MapMode = 5
  sketch-geometry (12):
    g0: LineSegment StartX=101.78 StartY=40.22 StartZ=0 EndX=101.78 EndY=32.22 EndZ=0
    g1: LineSegment StartX=-66.22 StartY=32.22 StartZ=0 EndX=-66.22 EndY=40.22 EndZ=0
    g2: LineSegment StartX=-66.22 StartY=32.22 StartZ=0 EndX=7.78 EndY=32.22 EndZ=0
    g3: LineSegment StartX=7.78 StartY=32.22 StartZ=0 EndX=7.78 EndY=0 EndZ=0
    g4: LineSegment StartX=7.78 StartY=0 StartZ=0 EndX=27.78 EndY=0 EndZ=0
    g5: LineSegment StartX=27.78 StartY=0 StartZ=0 EndX=27.78 EndY=32.22 EndZ=0
    g6: LineSegment StartX=27.78 StartY=32.22 StartZ=0 EndX=101.78 EndY=32.22 EndZ=0
    g7: LineSegment StartX=-66.22 StartY=40.22 StartZ=0 EndX=0 EndY=40.22 EndZ=0
    g8: LineSegment StartX=101.78 StartY=40.22 StartZ=0 EndX=35.56 EndY=40.22 EndZ=0
    g9: LineSegment StartX=0 StartY=40.22 StartZ=0 EndX=0 EndY=44.52 EndZ=0
    g10: LineSegment StartX=0 StartY=44.52 StartZ=0 EndX=35.56 EndY=44.52 EndZ=0
    g11: LineSegment StartX=35.56 StartY=44.52 StartZ=0 EndX=35.56 EndY=40.22 EndZ=0
  constraints (36):
    c: Vertical(g0)
    c: Vertical(g1)
    c: DistanceY(g0,g0) = 8
    c: Coincident(g2,g1)
    c: Horizontal(g2)
    c: Vertical(g3)
    c: Coincident(g4,g3)
    c: Horizontal(g4)
    c: Coincident(g5,g4)
    c: Vertical(g5)
    c: Coincident(g6,g5)
    c: Coincident(g6,g0)
    c: Horizontal(g6)
    c: Equal(g2,g6)
    c: Horizontal(g2,g5)
    c: DistanceX(g1,g0) = 168
    c: Coincident(g7,g1)
    c: PointOnObject(g7,g-2)
    c: Horizontal(g7)
    c: Coincident(g8,g0)
    c: Horizontal(g8)
    c: DistanceX(g7,g8) = 35.56
    c: Equal(g1,g0)
    c: Coincident(g9,g7)
    c: Vertical(g9)
    c: Coincident(g10,g9)
    c: Horizontal(g10)
    c: Coincident(g11,g10)
    c: Coincident(g11,g8)
    c: Vertical(g11)
    c: DistanceY(g11,g11) = 4.3
    c: PointOnObject(g4,g-1)
    c: Coincident(g2,g3)
    c: DistanceX(g6,g6) = 74
    c: DistanceX(g1,g-1) = 66.22
    c: DistanceY(g-1,g1) = 32.22
FEATURE [PartDesign::Pad] Pad044
  Direction = (0,0,1)
  Length = 6
  Length2 = 10
  Profile = -> Sketch065
  ReferenceAxis = -> Sketch065 [N_Axis]
  Reversed = true
  Suppressed = false
  Type = 0
FEATURE [Sketcher::SketchObject] Sketch074
  ArcFitTolerance = 0
  AttachmentSupport = -> [XY_Plane229]
  FullyConstrained = true
  MakeInternals = false
  MapMode = 5
  sketch-geometry (1):
    g0: Circle CenterX=0 CenterY=0 CenterZ=0 NormalX=0 NormalY=0 NormalZ=1 AngleXU=0 Radius=12
  constraints (2):
    c: Diameter(g0) = 24
    c: Coincident(g0,g-1)
FEATURE [PartDesign::Pad] Pad051
  Direction = (0,0,1)
  Length = 56.5
  Length2 = 10
  Profile = -> Sketch074
  ReferenceAxis = -> Sketch074 [N_Axis]
  Suppressed = false
  Type = 0
FEATURE [Sketcher::SketchObject] Sketch075
  ArcFitTolerance = 0
  AttachmentSupport = -> [XY_Plane230]
  FullyConstrained = true
  MakeInternals = false
  MapMode = 5
  sketch-geometry (1):
    g0: Circle CenterX=0 CenterY=0 CenterZ=0 NormalX=0 NormalY=0 NormalZ=1 AngleXU=0 Radius=12
  constraints (2):
    c: Diameter(g0) = 24
    c: Coincident(g0,g-1)
FEATURE [PartDesign::Pad] Pad052
  Direction = (0,0,1)
  Length = 56.5
  Length2 = 10
  Profile = -> Sketch075
  ReferenceAxis = -> Sketch075 [N_Axis]
  Suppressed = false
  Type = 0
FEATURE [Sketcher::SketchObject] Sketch081
  ArcFitTolerance = 0
  AttachmentSupport = -> [XY_Plane235]
  FullyConstrained = true
  MakeInternals = false
  MapMode = 5
  sketch-geometry (1):
    g0: Circle CenterX=0 CenterY=0 CenterZ=0 NormalX=0 NormalY=0 NormalZ=1 AngleXU=0 Radius=12
  constraints (2):
    c: Diameter(g0) = 24
    c: Coincident(g0,g-1)
FEATURE [PartDesign::Pad] Pad057
  Direction = (0,0,1)
  Length = 56.5
  Length2 = 10
  Profile = -> Sketch081
  ReferenceAxis = -> Sketch081 [N_Axis]
  Suppressed = false
  Type = 0
FEATURE [Sketcher::SketchObject] Sketch082
  ArcFitTolerance = 0
  AttachmentSupport = -> [XZ_Plane237]
  FullyConstrained = true
  MakeInternals = false
  MapMode = 5
  Placement = pos=(0,0,0) rot=(1,0,0;1.5708rad)
  sketch-geometry (1):
    g0: Circle CenterX=0 CenterY=0 CenterZ=0 NormalX=0 NormalY=0 NormalZ=1 AngleXU=0 Radius=12
  constraints (2):
    c: Coincident(g0,g-1)
    c: Diameter(g0) = 24
FEATURE [PartDesign::Pad] Pad058
  Direction = (0,-1,2e-16)
  Length = 50
  Length2 = 10
  Placement = pos=(0,0,0) rot=(1,0,0;1.5708rad)
  Profile = -> Sketch082
  ReferenceAxis = -> Sketch082 [N_Axis]
  Reversed = true
  Suppressed = false
  Type = 0
FEATURE [Sketcher::SketchObject] Sketch083
  ArcFitTolerance = 0
  AttachmentSupport = -> [XZ_Plane238]
  FullyConstrained = true
  MakeInternals = false
  MapMode = 5
  Placement = pos=(0,0,0) rot=(1,0,0;1.5708rad)
  sketch-geometry (1):
    g0: Circle CenterX=0 CenterY=0 CenterZ=0 NormalX=0 NormalY=0 NormalZ=1 AngleXU=0 Radius=8
  constraints (2):
    c: Coincident(g0,g-1)
    c: Diameter(g0) = 16
FEATURE [PartDesign::Pad] Pad059
  Direction = (0,-1,2e-16)
  Length = 50.5
  Length2 = 10
  Placement = pos=(0,0,0) rot=(1,0,0;1.5708rad)
  Profile = -> Sketch083
  ReferenceAxis = -> Sketch083 [N_Axis]
  Reversed = true
  Suppressed = false
  Type = 0
FEATURE [Sketcher::SketchObject] Sketch084
  ArcFitTolerance = 0
  AttachmentSupport = -> [XZ_Plane241]
  FullyConstrained = true
  MakeInternals = false
  MapMode = 5
  Placement = pos=(0,0,0) rot=(1,0,0;1.5708rad)
  sketch-geometry (5):
    g0: Circle CenterX=0 CenterY=0 CenterZ=0 NormalX=0 NormalY=0 NormalZ=1 AngleXU=0 Radius=5
    g1: LineSegment StartX=-13 StartY=18 StartZ=0 EndX=13 EndY=18 EndZ=0
    g2: LineSegment StartX=-13 StartY=18 StartZ=0 EndX=-13 EndY=-3.6e-15 EndZ=0
    g3: LineSegment StartX=13 StartY=18 StartZ=0 EndX=13 EndY=-3.6e-15 EndZ=0
    g4: ArcOfCircle CenterX=0 CenterY=0 CenterZ=0 NormalX=0 NormalY=0 NormalZ=1 AngleXU=0 Radius=13 StartAngle=3.14159 EndAngle=6.28319
  constraints (13):
    c: Coincident(g0,g-1)
    c: Diameter(g0) = 10
    c: DistanceX(g1,g1) = 26
    c: Symmetric(g1,g1,g-2)
    c: DistanceY(g0,g1) = 18
    c: Coincident(g2,g1)
    c: PointOnObject(g2,g-1)
    c: Vertical(g2)
    c: Coincident(g3,g1)
    c: PointOnObject(g3,g-1)
    c: Coincident(g4,g0)
    c: Coincident(g4,g2)
    c: Coincident(g4,g3)
FEATURE [PartDesign::Pad] Pad062
  Direction = (0,-1,2e-16)
  Length = 3
  Length2 = 10
  Placement = pos=(0,0,0) rot=(1,0,0;1.5708rad)
  Profile = -> Sketch084
  ReferenceAxis = -> Sketch084 [N_Axis]
  Suppressed = false
  Type = 0
FEATURE [Sketcher::SketchObject] Sketch085
  ArcFitTolerance = 0
  AttachmentSupport = -> [Pad062]
  ExternalGeometry = -> [Pad062]
  FullyConstrained = true
  MakeInternals = false
  MapMode = 5
  Placement = pos=(0,-3,0) rot=(1,0,0;1.5708rad)
  sketch-geometry (4):
    g0: LineSegment StartX=-13 StartY=18 StartZ=0 EndX=-13 EndY=14 EndZ=0
    g1: LineSegment StartX=-13 StartY=14 StartZ=0 EndX=13 EndY=14 EndZ=0
    g2: LineSegment StartX=13 StartY=14 StartZ=0 EndX=13 EndY=18 EndZ=0
    g3: LineSegment StartX=13 StartY=18 StartZ=0 EndX=-13 EndY=18 EndZ=0
  constraints (10):
    c: Coincident(g0,g-3)
    c: Vertical(g0)
    c: Coincident(g1,g0)
    c: Horizontal(g1)
    c: Coincident(g2,g1)
    c: Coincident(g2,g-3)
    c: Vertical(g2)
    c: Coincident(g3,g2)
    c: Coincident(g3,g0)
    c: DistanceY(g0,g0) = 4
FEATURE [PartDesign::Pad] Pad063
  BaseFeature = -> Pad062
  Direction = (0,-1,2e-16)
  Length = 30
  Length2 = 10
  Placement = pos=(0,0,0) rot=(1,0,0;1.5708rad)
  Profile = -> Sketch085
  ReferenceAxis = -> Sketch085 [N_Axis]
  Suppressed = false
  Type = 0
FEATURE [Sketcher::SketchObject] Sketch086
  ArcFitTolerance = 0
  AttachmentSupport = -> [Pad063]
  ExternalGeometry = -> [Pad063]
  FullyConstrained = true
  MakeInternals = false
  MapMode = 5
  Placement = pos=(0,7.9e-15,18) rot=(0,0,1;3.14159rad)
  sketch-geometry (4):
    g0: Circle CenterX=-9 CenterY=7 CenterZ=0 NormalX=0 NormalY=0 NormalZ=1 AngleXU=0 Radius=2
    g1: Circle CenterX=9 CenterY=7 CenterZ=0 NormalX=0 NormalY=0 NormalZ=1 AngleXU=0 Radius=2
    g2: Circle CenterX=-9 CenterY=29 CenterZ=0 NormalX=0 NormalY=0 NormalZ=1 AngleXU=0 Radius=2
    g3: Circle CenterX=9 CenterY=29 CenterZ=0 NormalX=0 NormalY=0 NormalZ=1 AngleXU=0 Radius=2
  constraints (10):
    c: Diameter(g2) = 4
    c: Diameter(g3) = 4
    c: Diameter(g1) = 4
    c: Diameter(g0) = 4
    c: Symmetric(g2,g3,g-2)
    c: Symmetric(g0,g1,g-2)
    c: Vertical(g2,g0)
    c: DistanceX(g-4,g2) = 4
    c: DistanceY(g2,g-4) = 4
    c: DistanceY(g-4,g0) = 4
FEATURE [PartDesign::Pocket] Pocket029
  BaseFeature = -> Pad063
  Direction = (0,0,-1)
  Length = 5
  Length2 = 5
  Placement = pos=(0,0,0) rot=(1,0,0;1.5708rad)
  Profile = -> Sketch086
  ReferenceAxis = -> Sketch086 [N_Axis]
  Suppressed = false
  Type = 1
FEATURE [Sketcher::SketchObject] Sketch087
  ArcFitTolerance = 0
  AttachmentSupport = -> [Pocket029]
  FullyConstrained = true
  MakeInternals = false
  MapMode = 5
  Placement = pos=(0,9e-16,0) rot=(-1,0,0;1.5708rad)
  sketch-geometry (1):
    g0: Circle CenterX=0 CenterY=9.5 CenterZ=0 NormalX=0 NormalY=0 NormalZ=1 AngleXU=0 Radius=1
  constraints (3):
    c: PointOnObject(g0,g-2)
    c: Diameter(g0) = 2
    c: DistanceY(g-1,g0) = 9.5
FEATURE [PartDesign::Pocket] Pocket030
  BaseFeature = -> Pocket029
  Direction = (0,-1,-2e-16)
  Length = 5
  Length2 = 5
  Placement = pos=(0,0,0) rot=(1,0,0;1.5708rad)
  Profile = -> Sketch087
  ReferenceAxis = -> Sketch087 [N_Axis]
  Suppressed = false
  Type = 1
FEATURE [PartDesign::PolarPattern] PolarPattern012
  Angle = 360
  Axis = -> Sketch087 [N_Axis]
  BaseFeature = -> Pocket030
  Mode = 0
  Occurrences = 4
  Offset = 120
  Originals = -> [Pocket030]
  Placement = pos=(0,0,0) rot=(1,0,0;1.5708rad)
  Suppressed = false
  TransformMode = 0
FEATURE [PartDesign::SubShapeBinder] Binder
  BindCopyOnChange = 0
  BindMode = 0
  ClaimChildren = false
  Context = -> Body [Binder.]
  Fuse = false
  MakeFace = true
  OffsetFill = false
  OffsetIntersection = false
  OffsetJoinType = 0
  OffsetOpenResult = false
  PartialLoad = false
  Relative = true
  Support = -> [Part003[Part005.Body038.Pocket029.Sketch086.]]
  _Version = 2
FEATURE [Sketcher::SketchObject] Sketch088
  ArcFitTolerance = 0
  AttachmentSupport = -> [XZ_Plane242]
  FullyConstrained = true
  MakeInternals = false
  MapMode = 5
  Placement = pos=(0,0,0) rot=(1,0,0;1.5708rad)
  sketch-geometry (5):
    g0: Circle CenterX=0 CenterY=0 CenterZ=0 NormalX=0 NormalY=0 NormalZ=1 AngleXU=0 Radius=6
    g1: LineSegment StartX=-13 StartY=18 StartZ=0 EndX=13 EndY=18 EndZ=0
    g2: LineSegment StartX=-13 StartY=18 StartZ=0 EndX=-13 EndY=0 EndZ=0
    g3: LineSegment StartX=13 StartY=18 StartZ=0 EndX=13 EndY=-3.6e-15 EndZ=0
    g4: ArcOfCircle CenterX=0 CenterY=0 CenterZ=0 NormalX=0 NormalY=0 NormalZ=1 AngleXU=0 Radius=13 StartAngle=3.14159 EndAngle=6.28319
  constraints (13):
    c: Coincident(g0,g-1)
    c: Diameter(g0) = 12
    c: DistanceX(g1,g1) = 26
    c: Symmetric(g1,g1,g-2)
    c: DistanceY(g0,g1) = 18
    c: Coincident(g2,g1)
    c: PointOnObject(g2,g-1)
    c: Vertical(g2)
    c: Coincident(g3,g1)
    c: PointOnObject(g3,g-1)
    c: Coincident(g4,g0)
    c: Coincident(g4,g2)
    c: Coincident(g4,g3)
FEATURE [PartDesign::Pad] Pad064
  Direction = (0,-1,2e-16)
  Length = 3
  Length2 = 10
  Placement = pos=(0,0,0) rot=(1,0,0;1.5708rad)
  Profile = -> Sketch088
  ReferenceAxis = -> Sketch088 [N_Axis]
  Suppressed = false
  Type = 0
FEATURE [Sketcher::SketchObject] Sketch089
  ArcFitTolerance = 0
  AttachmentSupport = -> [Pad064]
  ExternalGeometry = -> [Pad064]
  FullyConstrained = true
  MakeInternals = false
  MapMode = 5
  Placement = pos=(0,-3,0) rot=(1,0,0;1.5708rad)
  sketch-geometry (4):
    g0: LineSegment StartX=-13 StartY=18 StartZ=0 EndX=-13 EndY=14 EndZ=0
    g1: LineSegment StartX=-13 StartY=14 StartZ=0 EndX=13 EndY=14 EndZ=0
    g2: LineSegment StartX=13 StartY=14 StartZ=0 EndX=13 EndY=18 EndZ=0
    g3: LineSegment StartX=13 StartY=18 StartZ=0 EndX=-13 EndY=18 EndZ=0
  constraints (10):
    c: Coincident(g0,g-3)
    c: Vertical(g0)
    c: Coincident(g1,g0)
    c: Horizontal(g1)
    c: Coincident(g2,g1)
    c: Coincident(g2,g-3)
    c: Vertical(g2)
    c: Coincident(g3,g2)
    c: Coincident(g3,g0)
    c: DistanceY(g0,g0) = 4
FEATURE [PartDesign::Pad] Pad065
  BaseFeature = -> Pad064
  Direction = (0,-1,2e-16)
  Length = 30
  Length2 = 10
  Placement = pos=(0,0,0) rot=(1,0,0;1.5708rad)
  Profile = -> Sketch089
  ReferenceAxis = -> Sketch089 [N_Axis]
  Suppressed = false
  Type = 0
FEATURE [Sketcher::SketchObject] Sketch090
  ArcFitTolerance = 0
  AttachmentSupport = -> [Pad065]
  ExternalGeometry = -> [Pad065]
  FullyConstrained = true
  MakeInternals = false
  MapMode = 5
  Placement = pos=(0,7.9e-15,18) rot=(0,0,1;3.14159rad)
  sketch-geometry (4):
    g0: Circle CenterX=-9 CenterY=7 CenterZ=0 NormalX=0 NormalY=0 NormalZ=1 AngleXU=0 Radius=2
    g1: Circle CenterX=9 CenterY=7 CenterZ=0 NormalX=0 NormalY=0 NormalZ=1 AngleXU=0 Radius=2
    g2: Circle CenterX=-9 CenterY=29 CenterZ=0 NormalX=0 NormalY=0 NormalZ=1 AngleXU=0 Radius=2
    g3: Circle CenterX=9 CenterY=29 CenterZ=0 NormalX=0 NormalY=0 NormalZ=1 AngleXU=0 Radius=2
  constraints (10):
    c: Diameter(g2) = 4
    c: Diameter(g3) = 4
    c: Diameter(g1) = 4
    c: Diameter(g0) = 4
    c: Symmetric(g2,g3,g-2)
    c: Symmetric(g0,g1,g-2)
    c: Vertical(g2,g0)
    c: DistanceX(g-4,g2) = 4
    c: DistanceY(g2,g-4) = 4
    c: DistanceY(g-4,g0) = 4
FEATURE [PartDesign::Pocket] Pocket032
  BaseFeature = -> Pad065
  Direction = (0,0,-1)
  Length = 5
  Length2 = 5
  Placement = pos=(0,0,0) rot=(1,0,0;1.5708rad)
  Profile = -> Sketch090
  ReferenceAxis = -> Sketch090 [N_Axis]
  Suppressed = false
  Type = 1
FEATURE [Sketcher::SketchObject] Sketch091
  ArcFitTolerance = 0
  AttachmentSupport = -> [Pocket032]
  FullyConstrained = true
  MakeInternals = false
  MapMode = 5
  Placement = pos=(0,8e-16,0) rot=(-1,0,0;1.5708rad)
  sketch-geometry (1):
    g0: Circle CenterX=0 CenterY=9.5 CenterZ=0 NormalX=0 NormalY=0 NormalZ=1 AngleXU=0 Radius=1
  constraints (3):
    c: PointOnObject(g0,g-2)
    c: Diameter(g0) = 2
    c: DistanceY(g-1,g0) = 9.5
FEATURE [PartDesign::Pocket] Pocket033
  BaseFeature = -> Pocket032
  Direction = (0,-1,-2e-16)
  Length = 5
  Length2 = 5
  Placement = pos=(0,0,0) rot=(1,0,0;1.5708rad)
  Profile = -> Sketch091
  ReferenceAxis = -> Sketch091 [N_Axis]
  Suppressed = false
  Type = 1
FEATURE [PartDesign::PolarPattern] PolarPattern013
  Angle = 360
  Axis = -> Sketch091 [N_Axis]
  BaseFeature = -> Pocket033
  Mode = 0
  Occurrences = 4
  Offset = 120
  Originals = -> [Pocket033]
  Placement = pos=(0,0,0) rot=(1,0,0;1.5708rad)
  Suppressed = false
  TransformMode = 0
FEATURE [PartDesign::Body] Body039  label="Moteur support 2"
  AllowCompound = false
  Group = -> [Sketch088,Pad064,Sketch089,Pad065,Sketch090,Pocket032,Sketch091,Pocket033,PolarPattern013]
  Origin = -> Origin242
  Placement = pos=(43.5918,62.2556,-8) rot=(0,0,-1;0.610865rad)
  Tip = -> PolarPattern013
FEATURE [Sketcher::SketchObject] Sketch092
  ArcFitTolerance = 0
  AttachmentSupport = -> [XZ_Plane243]
  FullyConstrained = true
  MakeInternals = false
  MapMode = 5
  Placement = pos=(0,0,0) rot=(1,0,0;1.5708rad)
  sketch-geometry (5):
    g0: Circle CenterX=0 CenterY=0 CenterZ=0 NormalX=0 NormalY=0 NormalZ=1 AngleXU=0 Radius=6
    g1: LineSegment StartX=-13 StartY=18 StartZ=0 EndX=13 EndY=18 EndZ=0
    g2: LineSegment StartX=-13 StartY=18 StartZ=0 EndX=-13 EndY=0 EndZ=0
    g3: LineSegment StartX=13 StartY=18 StartZ=0 EndX=13 EndY=-3.6e-15 EndZ=0
    g4: ArcOfCircle CenterX=0 CenterY=0 CenterZ=0 NormalX=0 NormalY=0 NormalZ=1 AngleXU=0 Radius=13 StartAngle=3.14159 EndAngle=6.28319
  constraints (13):
    c: Coincident(g0,g-1)
    c: Diameter(g0) = 12
    c: DistanceX(g1,g1) = 26
    c: Symmetric(g1,g1,g-2)
    c: DistanceY(g0,g1) = 18
    c: Coincident(g2,g1)
    c: PointOnObject(g2,g-1)
    c: Vertical(g2)
    c: Coincident(g3,g1)
    c: PointOnObject(g3,g-1)
    c: Coincident(g4,g0)
    c: Coincident(g4,g2)
    c: Coincident(g4,g3)
FEATURE [PartDesign::Pad] Pad066
  Direction = (0,-1,2e-16)
  Length = 3
  Length2 = 10
  Placement = pos=(0,0,0) rot=(1,0,0;1.5708rad)
  Profile = -> Sketch092
  ReferenceAxis = -> Sketch092 [N_Axis]
  Suppressed = false
  Type = 0
FEATURE [Sketcher::SketchObject] Sketch093
  ArcFitTolerance = 0
  AttachmentSupport = -> [Pad066]
  ExternalGeometry = -> [Pad066]
  FullyConstrained = true
  MakeInternals = false
  MapMode = 5
  Placement = pos=(0,-3,0) rot=(1,0,0;1.5708rad)
  sketch-geometry (4):
    g0: LineSegment StartX=-13 StartY=18 StartZ=0 EndX=-13 EndY=14 EndZ=0
    g1: LineSegment StartX=-13 StartY=14 StartZ=0 EndX=13 EndY=14 EndZ=0
    g2: LineSegment StartX=13 StartY=14 StartZ=0 EndX=13 EndY=18 EndZ=0
    g3: LineSegment StartX=13 StartY=18 StartZ=0 EndX=-13 EndY=18 EndZ=0
  constraints (10):
    c: Coincident(g0,g-3)
    c: Vertical(g0)
    c: Coincident(g1,g0)
    c: Horizontal(g1)
    c: Coincident(g2,g1)
    c: Coincident(g2,g-3)
    c: Vertical(g2)
    c: Coincident(g3,g2)
    c: Coincident(g3,g0)
    c: DistanceY(g0,g0) = 4
FEATURE [PartDesign::Pad] Pad067
  BaseFeature = -> Pad066
  Direction = (0,-1,2e-16)
  Length = 30
  Length2 = 10
  Placement = pos=(0,0,0) rot=(1,0,0;1.5708rad)
  Profile = -> Sketch093
  ReferenceAxis = -> Sketch093 [N_Axis]
  Suppressed = false
  Type = 0
FEATURE [Sketcher::SketchObject] Sketch094
  ArcFitTolerance = 0
  AttachmentSupport = -> [Pad067]
  ExternalGeometry = -> [Pad067]
  FullyConstrained = true
  MakeInternals = false
  MapMode = 5
  Placement = pos=(0,7.9e-15,18) rot=(0,0,1;3.14159rad)
  sketch-geometry (4):
    g0: Circle CenterX=-9 CenterY=7 CenterZ=0 NormalX=0 NormalY=0 NormalZ=1 AngleXU=0 Radius=2
    g1: Circle CenterX=9 CenterY=7 CenterZ=0 NormalX=0 NormalY=0 NormalZ=1 AngleXU=0 Radius=2
    g2: Circle CenterX=-9 CenterY=29 CenterZ=0 NormalX=0 NormalY=0 NormalZ=1 AngleXU=0 Radius=2
    g3: Circle CenterX=9 CenterY=29 CenterZ=0 NormalX=0 NormalY=0 NormalZ=1 AngleXU=0 Radius=2
  constraints (10):
    c: Diameter(g2) = 4
    c: Diameter(g3) = 4
    c: Diameter(g1) = 4
    c: Diameter(g0) = 4
    c: Symmetric(g2,g3,g-2)
    c: Symmetric(g0,g1,g-2)
    c: Vertical(g2,g0)
    c: DistanceX(g-4,g2) = 4
    c: DistanceY(g2,g-4) = 4
    c: DistanceY(g-4,g0) = 4
FEATURE [PartDesign::Pocket] Pocket034
  BaseFeature = -> Pad067
  Direction = (0,0,-1)
  Length = 5
  Length2 = 5
  Placement = pos=(0,0,0) rot=(1,0,0;1.5708rad)
  Profile = -> Sketch094
  ReferenceAxis = -> Sketch094 [N_Axis]
  Suppressed = false
  Type = 1
FEATURE [Sketcher::SketchObject] Sketch095
  ArcFitTolerance = 0
  AttachmentSupport = -> [Pocket034]
  FullyConstrained = true
  MakeInternals = false
  MapMode = 5
  Placement = pos=(0,8e-16,0) rot=(-1,0,0;1.5708rad)
  sketch-geometry (1):
    g0: Circle CenterX=0 CenterY=9.5 CenterZ=0 NormalX=0 NormalY=0 NormalZ=1 AngleXU=0 Radius=1
  constraints (3):
    c: PointOnObject(g0,g-2)
    c: Diameter(g0) = 2
    c: DistanceY(g-1,g0) = 9.5
FEATURE [PartDesign::Pocket] Pocket035
  BaseFeature = -> Pocket034
  Direction = (0,-1,-2e-16)
  Length = 5
  Length2 = 5
  Placement = pos=(0,0,0) rot=(1,0,0;1.5708rad)
  Profile = -> Sketch095
  ReferenceAxis = -> Sketch095 [N_Axis]
  Suppressed = false
  Type = 1
FEATURE [PartDesign::PolarPattern] PolarPattern014
  Angle = 360
  Axis = -> Sketch095 [N_Axis]
  BaseFeature = -> Pocket035
  Mode = 0
  Occurrences = 4
  Offset = 120
  Originals = -> [Pocket035]
  Placement = pos=(0,0,0) rot=(1,0,0;1.5708rad)
  Suppressed = false
  TransformMode = 0
FEATURE [PartDesign::Body] Body040  label="Moteur support 3"
  AllowCompound = false
  Group = -> [Sketch092,Pad066,Sketch093,Pad067,Sketch094,Pocket034,Sketch095,Pocket035,PolarPattern014]
  Origin = -> Origin243
  Placement = pos=(43.5918,-62.2556,-8) rot=(0,0,1;3.75246rad)
  Tip = -> PolarPattern014
FEATURE [Sketcher::SketchObject] Sketch096
  ArcFitTolerance = 0
  AttachmentSupport = -> [XZ_Plane244]
  FullyConstrained = true
  MakeInternals = false
  MapMode = 5
  Placement = pos=(0,0,0) rot=(1,0,0;1.5708rad)
  sketch-geometry (5):
    g0: Circle CenterX=0 CenterY=0 CenterZ=0 NormalX=0 NormalY=0 NormalZ=1 AngleXU=0 Radius=6
    g1: LineSegment StartX=-13 StartY=18 StartZ=0 EndX=13 EndY=18 EndZ=0
    g2: LineSegment StartX=-13 StartY=18 StartZ=0 EndX=-13 EndY=0 EndZ=0
    g3: LineSegment StartX=13 StartY=18 StartZ=0 EndX=13 EndY=-3.6e-15 EndZ=0
    g4: ArcOfCircle CenterX=0 CenterY=0 CenterZ=0 NormalX=0 NormalY=0 NormalZ=1 AngleXU=0 Radius=13 StartAngle=3.14159 EndAngle=6.28319
  constraints (13):
    c: Coincident(g0,g-1)
    c: Diameter(g0) = 12
    c: DistanceX(g1,g1) = 26
    c: Symmetric(g1,g1,g-2)
    c: DistanceY(g0,g1) = 18
    c: Coincident(g2,g1)
    c: PointOnObject(g2,g-1)
    c: Vertical(g2)
    c: Coincident(g3,g1)
    c: PointOnObject(g3,g-1)
    c: Coincident(g4,g0)
    c: Coincident(g4,g2)
    c: Coincident(g4,g3)
FEATURE [PartDesign::Pad] Pad068
  Direction = (0,-1,2e-16)
  Length = 3
  Length2 = 10
  Placement = pos=(0,0,0) rot=(1,0,0;1.5708rad)
  Profile = -> Sketch096
  ReferenceAxis = -> Sketch096 [N_Axis]
  Suppressed = false
  Type = 0
FEATURE [Sketcher::SketchObject] Sketch097
  ArcFitTolerance = 0
  AttachmentSupport = -> [Pad068]
  ExternalGeometry = -> [Pad068]
  FullyConstrained = true
  MakeInternals = false
  MapMode = 5
  Placement = pos=(0,-3,0) rot=(1,0,0;1.5708rad)
  sketch-geometry (4):
    g0: LineSegment StartX=-13 StartY=18 StartZ=0 EndX=-13 EndY=14 EndZ=0
    g1: LineSegment StartX=-13 StartY=14 StartZ=0 EndX=13 EndY=14 EndZ=0
    g2: LineSegment StartX=13 StartY=14 StartZ=0 EndX=13 EndY=18 EndZ=0
    g3: LineSegment StartX=13 StartY=18 StartZ=0 EndX=-13 EndY=18 EndZ=0
  constraints (10):
    c: Coincident(g0,g-3)
    c: Vertical(g0)
    c: Coincident(g1,g0)
    c: Horizontal(g1)
    c: Coincident(g2,g1)
    c: Coincident(g2,g-3)
    c: Vertical(g2)
    c: Coincident(g3,g2)
    c: Coincident(g3,g0)
    c: DistanceY(g0,g0) = 4
FEATURE [PartDesign::Pad] Pad069
  BaseFeature = -> Pad068
  Direction = (0,-1,2e-16)
  Length = 30
  Length2 = 10
  Placement = pos=(0,0,0) rot=(1,0,0;1.5708rad)
  Profile = -> Sketch097
  ReferenceAxis = -> Sketch097 [N_Axis]
  Suppressed = false
  Type = 0
FEATURE [Sketcher::SketchObject] Sketch098
  ArcFitTolerance = 0
  AttachmentSupport = -> [Pad069]
  ExternalGeometry = -> [Pad069]
  FullyConstrained = true
  MakeInternals = false
  MapMode = 5
  Placement = pos=(0,7.9e-15,18) rot=(0,0,1;3.14159rad)
  sketch-geometry (4):
    g0: Circle CenterX=-9 CenterY=7 CenterZ=0 NormalX=0 NormalY=0 NormalZ=1 AngleXU=0 Radius=2
    g1: Circle CenterX=9 CenterY=7 CenterZ=0 NormalX=0 NormalY=0 NormalZ=1 AngleXU=0 Radius=2
    g2: Circle CenterX=-9 CenterY=29 CenterZ=0 NormalX=0 NormalY=0 NormalZ=1 AngleXU=0 Radius=2
    g3: Circle CenterX=9 CenterY=29 CenterZ=0 NormalX=0 NormalY=0 NormalZ=1 AngleXU=0 Radius=2
  constraints (10):
    c: Diameter(g2) = 4
    c: Diameter(g3) = 4
    c: Diameter(g1) = 4
    c: Diameter(g0) = 4
    c: Symmetric(g2,g3,g-2)
    c: Symmetric(g0,g1,g-2)
    c: Vertical(g2,g0)
    c: DistanceX(g-4,g2) = 4
    c: DistanceY(g2,g-4) = 4
    c: DistanceY(g-4,g0) = 4
FEATURE [PartDesign::Pocket] Pocket036
  BaseFeature = -> Pad069
  Direction = (0,0,-1)
  Length = 5
  Length2 = 5
  Placement = pos=(0,0,0) rot=(1,0,0;1.5708rad)
  Profile = -> Sketch098
  ReferenceAxis = -> Sketch098 [N_Axis]
  Suppressed = false
  Type = 1
FEATURE [Sketcher::SketchObject] Sketch099
  ArcFitTolerance = 0
  AttachmentSupport = -> [Pocket036]
  FullyConstrained = true
  MakeInternals = false
  MapMode = 5
  Placement = pos=(0,8e-16,0) rot=(-1,0,0;1.5708rad)
  sketch-geometry (1):
    g0: Circle CenterX=0 CenterY=9.5 CenterZ=0 NormalX=0 NormalY=0 NormalZ=1 AngleXU=0 Radius=1
  constraints (3):
    c: PointOnObject(g0,g-2)
    c: Diameter(g0) = 2
    c: DistanceY(g-1,g0) = 9.5
FEATURE [PartDesign::Pocket] Pocket037
  BaseFeature = -> Pocket036
  Direction = (0,-1,-2e-16)
  Length = 5
  Length2 = 5
  Placement = pos=(0,0,0) rot=(1,0,0;1.5708rad)
  Profile = -> Sketch099
  ReferenceAxis = -> Sketch099 [N_Axis]
  Suppressed = false
  Type = 1
FEATURE [PartDesign::PolarPattern] PolarPattern015
  Angle = 360
  Axis = -> Sketch099 [N_Axis]
  BaseFeature = -> Pocket037
  Mode = 0
  Occurrences = 4
  Offset = 120
  Originals = -> [Pocket037]
  Placement = pos=(0,0,0) rot=(1,0,0;1.5708rad)
  Suppressed = false
  TransformMode = 0
FEATURE [PartDesign::Body] Body041  label="Moteur support 4"
  AllowCompound = false
  Group = -> [Sketch096,Pad068,Sketch097,Pad069,Sketch098,Pocket036,Sketch099,Pocket037,PolarPattern015]
  Origin = -> Origin244
  Placement = pos=(-43.5918,-62.2556,-8) rot=(0,0,1;2.53073rad)
  Tip = -> PolarPattern015
FEATURE [PartDesign::SubShapeBinder] Binder005
  BindCopyOnChange = 0
  BindMode = 0
  ClaimChildren = false
  Context = -> Body [Binder005.]
  Fuse = false
  MakeFace = true
  OffsetFill = false
  OffsetIntersection = false
  OffsetJoinType = 0
  OffsetOpenResult = false
  PartialLoad = false
  Relative = true
  Support = -> [Part003[Part006.Body039.Pocket032.Sketch090.]]
  _Version = 2
FEATURE [PartDesign::Pocket] Pocket031
  BaseFeature = -> Pocket019
  Direction = (0,0,-1)
  Length = 5
  Length2 = 5
  Profile = -> Binder
  Reversed = true
  Suppressed = false
  Type = 1
FEATURE [PartDesign::Pocket] Pocket038
  BaseFeature = -> Pocket031
  Direction = (0,0,-1)
  Length = 5
  Length2 = 5
  Profile = -> Binder005
  Reversed = true
  Suppressed = false
  Type = 1
FEATURE [PartDesign::SubShapeBinder] Binder006
  BindCopyOnChange = 0
  BindMode = 0
  ClaimChildren = false
  Context = -> Body [Binder006.]
  Fuse = false
  MakeFace = true
  OffsetFill = false
  OffsetIntersection = false
  OffsetJoinType = 0
  OffsetOpenResult = false
  PartialLoad = false
  Relative = true
  Support = -> [Part003[Part007.Body040.Pocket034.Sketch094.]]
  _Version = 2
FEATURE [PartDesign::Pocket] Pocket039
  BaseFeature = -> Pocket038
  Direction = (0,0,-1)
  Length = 5
  Length2 = 5
  Profile = -> Binder006
  Reversed = true
  Suppressed = false
  Type = 1
FEATURE [PartDesign::SubShapeBinder] Binder007
  BindCopyOnChange = 0
  BindMode = 0
  ClaimChildren = false
  Context = -> Body [Binder007.]
  Fuse = false
  MakeFace = true
  OffsetFill = false
  OffsetIntersection = false
  OffsetJoinType = 0
  OffsetOpenResult = false
  PartialLoad = false
  Relative = true
  Support = -> [Part003[Part008.Body041.Pocket036.Sketch098.]]
  _Version = 2
FEATURE [PartDesign::Pocket] Pocket040
  BaseFeature = -> Pocket039
  Direction = (0,0,-1)
  Length = 5
  Length2 = 5
  Profile = -> Binder007
  Reversed = true
  Suppressed = false
  Type = 1
FEATURE [Sketcher::SketchObject] Sketch102
  ArcFitTolerance = 0
  AttachmentSupport = -> [XY_Plane248]
  FullyConstrained = true
  MakeInternals = false
  MapMode = 5
  sketch-geometry (1):
    g0: Circle CenterX=0 CenterY=0 CenterZ=0 NormalX=0 NormalY=0 NormalZ=1 AngleXU=0 Radius=85
  constraints (2):
    c: Coincident(g0,g-1)
    c: Diameter(g0) = 170
FEATURE [PartDesign::Pad] Pad070  label="Structural layer001"
  Direction = (0,0,1)
  Length = 3
  Length2 = 10
  Profile = -> Sketch102
  ReferenceAxis = -> Sketch102 [N_Axis]
  Suppressed = false
  Type = 0
FEATURE [Sketcher::SketchObject] Sketch109
  ArcFitTolerance = 0
  AttachmentSupport = -> [YZ_Plane251]
  FullyConstrained = true
  MakeInternals = false
  MapMode = 5
  Placement = pos=(0,0,0) rot=(0.57735,0.57735,0.57735;2.0944rad)
  sketch-geometry (4):
    g0: LineSegment StartX=-40 StartY=7 StartZ=0 EndX=40 EndY=7 EndZ=0
    g1: LineSegment StartX=40 StartY=7 StartZ=0 EndX=40 EndY=-7 EndZ=0
    g2: LineSegment StartX=40 StartY=-7 StartZ=0 EndX=-40 EndY=-7 EndZ=0
    g3: LineSegment StartX=-40 StartY=-7 StartZ=0 EndX=-40 EndY=7 EndZ=0
  constraints (10):
    c: Coincident(g0,g1)
    c: Coincident(g1,g2)
    c: Coincident(g2,g3)
    c: Coincident(g3,g0)
    c: Horizontal(g2)
    c: Vertical(g1)
    c: Symmetric(g2,g0,g-1)
    c: Symmetric(g0,g0,g-2)
    c: DistanceX(g0,g0) = 80
    c: DistanceY(g1,g1) = 14
FEATURE [PartDesign::Pad] Pad076
  Direction = (1,0,0)
  Length = 3
  Length2 = 10
  Placement = pos=(0,0,0) rot=(1,1,1;2.0944rad)
  Profile = -> Sketch109
  ReferenceAxis = -> Sketch109 [N_Axis]
  Suppressed = false
  Type = 0
FEATURE [Sketcher::SketchObject] Sketch121
  ArcFitTolerance = 0
  AttachmentSupport = -> [XZ_Plane255]
  FullyConstrained = true
  MakeInternals = false
  MapMode = 5
  Placement = pos=(0,0,0) rot=(1,0,0;1.5708rad)
  sketch-geometry (5):
    g0: Circle CenterX=0 CenterY=0 CenterZ=0 NormalX=0 NormalY=0 NormalZ=1 AngleXU=0 Radius=6
    g1: LineSegment StartX=-13 StartY=17 StartZ=0 EndX=13 EndY=17 EndZ=0
    g2: LineSegment StartX=-13 StartY=17 StartZ=0 EndX=-13 EndY=0 EndZ=0
    g3: LineSegment StartX=13 StartY=17 StartZ=0 EndX=13 EndY=-3.6e-15 EndZ=0
    g4: ArcOfCircle CenterX=0 CenterY=0 CenterZ=0 NormalX=0 NormalY=0 NormalZ=1 AngleXU=0 Radius=13 StartAngle=3.14159 EndAngle=6.28319
  constraints (13):
    c: Coincident(g0,g-1)
    c: Diameter(g0) = 12
    c: DistanceX(g1,g1) = 26
    c: Symmetric(g1,g1,g-2)
    c: DistanceY(g0,g1) = 17
    c: Coincident(g2,g1)
    c: PointOnObject(g2,g-1)
    c: Vertical(g2)
    c: Coincident(g3,g1)
    c: PointOnObject(g3,g-1)
    c: Coincident(g4,g0)
    c: Coincident(g4,g2)
    c: Coincident(g4,g3)
FEATURE [PartDesign::Pad] Pad085
  Direction = (0,-1,2e-16)
  Length = 3
  Length2 = 10
  Placement = pos=(0,0,0) rot=(1,0,0;1.5708rad)
  Profile = -> Sketch121
  ReferenceAxis = -> Sketch121 [N_Axis]
  Suppressed = false
  Type = 0
FEATURE [Sketcher::SketchObject] Sketch122
  ArcFitTolerance = 0
  AttachmentSupport = -> [Pad085]
  ExternalGeometry = -> [Pad085]
  FullyConstrained = true
  MakeInternals = false
  MapMode = 5
  Placement = pos=(0,-3,0) rot=(1,0,0;1.5708rad)
  sketch-geometry (4):
    g0: LineSegment StartX=-13 StartY=17 StartZ=0 EndX=-13 EndY=14 EndZ=0
    g1: LineSegment StartX=-13 StartY=14 StartZ=0 EndX=13 EndY=14 EndZ=0
    g2: LineSegment StartX=13 StartY=14 StartZ=0 EndX=13 EndY=17 EndZ=0
    g3: LineSegment StartX=13 StartY=17 StartZ=0 EndX=-13 EndY=17 EndZ=0
  constraints (10):
    c: Coincident(g0,g-3)
    c: Vertical(g0)
    c: Coincident(g1,g0)
    c: Horizontal(g1)
    c: Coincident(g2,g1)
    c: Coincident(g2,g-3)
    c: Vertical(g2)
    c: Coincident(g3,g2)
    c: Coincident(g3,g0)
    c: DistanceY(g0,g0) = 3
FEATURE [PartDesign::Pad] Pad086
  BaseFeature = -> Pad085
  Direction = (0,-1,2e-16)
  Length = 30
  Length2 = 10
  Placement = pos=(0,0,0) rot=(1,0,0;1.5708rad)
  Profile = -> Sketch122
  ReferenceAxis = -> Sketch122 [N_Axis]
  Suppressed = false
  Type = 0
FEATURE [Sketcher::SketchObject] Sketch123
  ArcFitTolerance = 0
  AttachmentSupport = -> [Pad086]
  ExternalGeometry = -> [Pad086]
  FullyConstrained = true
  MakeInternals = false
  MapMode = 5
  Placement = pos=(2.4e-15,7.5e-15,17) rot=(0,0,1;3.14159rad)
  sketch-geometry (4):
    g0: Circle CenterX=-9 CenterY=7 CenterZ=0 NormalX=0 NormalY=0 NormalZ=1 AngleXU=0 Radius=2
    g1: Circle CenterX=9 CenterY=7 CenterZ=0 NormalX=0 NormalY=0 NormalZ=1 AngleXU=0 Radius=2
    g2: Circle CenterX=-9 CenterY=29 CenterZ=0 NormalX=0 NormalY=0 NormalZ=1 AngleXU=0 Radius=2
    g3: Circle CenterX=9 CenterY=29 CenterZ=0 NormalX=0 NormalY=0 NormalZ=1 AngleXU=0 Radius=2
  constraints (10):
    c: Diameter(g2) = 4
    c: Diameter(g3) = 4
    c: Diameter(g1) = 4
    c: Diameter(g0) = 4
    c: Symmetric(g2,g3,g-2)
    c: Symmetric(g0,g1,g-2)
    c: Vertical(g2,g0)
    c: DistanceX(g-4,g2) = 4
    c: DistanceY(g2,g-4) = 4
    c: DistanceY(g-4,g0) = 4
FEATURE [PartDesign::Pocket] Pocket048
  BaseFeature = -> Pad086
  Direction = (0,0,-1)
  Length = 5
  Length2 = 5
  Placement = pos=(0,0,0) rot=(1,0,0;1.5708rad)
  Profile = -> Sketch123
  ReferenceAxis = -> Sketch123 [N_Axis]
  Suppressed = false
  Type = 1
FEATURE [Sketcher::SketchObject] Sketch124
  ArcFitTolerance = 0
  AttachmentSupport = -> [Pocket048]
  FullyConstrained = true
  MakeInternals = false
  MapMode = 5
  Placement = pos=(0,7e-16,0) rot=(-1,0,0;1.5708rad)
  sketch-geometry (1):
    g0: Circle CenterX=0 CenterY=9.5 CenterZ=0 NormalX=0 NormalY=0 NormalZ=1 AngleXU=0 Radius=1
  constraints (3):
    c: PointOnObject(g0,g-2)
    c: Diameter(g0) = 2
    c: DistanceY(g-1,g0) = 9.5
FEATURE [PartDesign::Pocket] Pocket049
  BaseFeature = -> Pocket048
  Direction = (0,-1,-2e-16)
  Length = 5
  Length2 = 5
  Placement = pos=(0,0,0) rot=(1,0,0;1.5708rad)
  Profile = -> Sketch124
  ReferenceAxis = -> Sketch124 [N_Axis]
  Suppressed = false
  Type = 1
FEATURE [PartDesign::PolarPattern] PolarPattern018
  Angle = 360
  Axis = -> Sketch124 [N_Axis]
  BaseFeature = -> Pocket049
  Mode = 0
  Occurrences = 4
  Offset = 120
  Originals = -> [Pocket049]
  Placement = pos=(0,0,0) rot=(1,0,0;1.5708rad)
  Suppressed = false
  TransformMode = 0
FEATURE [PartDesign::SubShapeBinder] Binder008
  BindCopyOnChange = 0
  BindMode = 0
  ClaimChildren = false
  Context = -> Body [Binder008.]
  Fuse = false
  MakeFace = true
  OffsetFill = false
  OffsetIntersection = false
  OffsetJoinType = 0
  OffsetOpenResult = false
  PartialLoad = false
  Relative = true
  Support = -> [Part011[Body050.Pocket048.Sketch123.]]
  _Version = 2
FEATURE [PartDesign::Pocket] Pocket050
  BaseFeature = -> Pocket040
  Direction = (0,0,-1)
  Length = 5
  Length2 = 5
  Profile = -> Binder008
  Suppressed = false
  Type = 1
FEATURE [PartDesign::SubShapeBinder] Binder010
  BindCopyOnChange = 0
  BindMode = 0
  ClaimChildren = false
  Context = -> Part015 [Body025.Binder010.]
  Fuse = false
  MakeFace = true
  OffsetFill = false
  OffsetIntersection = false
  OffsetJoinType = 0
  OffsetOpenResult = false
  PartialLoad = false
  Relative = true
  _Version = 2
FEATURE [PartDesign::Pocket] Pocket052
  BaseFeature = -> Pad044
  Direction = (0,0,-1)
  Length = 5
  Length2 = 5
  Profile = -> Binder010
  Suppressed = false
  Type = 1
FEATURE [Sketcher::SketchObject] Sketch126
  ArcFitTolerance = 0
  FullyConstrained = false
  MakeInternals = false
  MapMode = 5
  Placement = pos=(0,0,2) rot=(0,0,1;0rad)
  sketch-geometry (8):
    g0: Circle CenterX=-65.799 CenterY=-46 CenterZ=0 NormalX=0 NormalY=0 NormalZ=1 AngleXU=0 Radius=1.5
    g1: Circle CenterX=-46 CenterY=-65.799 CenterZ=0 NormalX=0 NormalY=0 NormalZ=1 AngleXU=0 Radius=1.5
    g2: LineSegment [constr] StartX=103.375 StartY=103.375 StartZ=0 EndX=-110.971 EndY=-110.971 EndZ=0
    g3: LineSegment [constr] StartX=0 StartY=0 StartZ=0 EndX=106.113 EndY=-106.113 EndZ=0
    g4: Circle CenterX=25 CenterY=-75.9117 CenterZ=0 NormalX=0 NormalY=0 NormalZ=1 AngleXU=0 Radius=1.5
    g5: Circle CenterX=75.9117 CenterY=-25 CenterZ=0 NormalX=0 NormalY=0 NormalZ=1 AngleXU=0 Radius=1.5
    g6: Circle CenterX=65.799 CenterY=46 CenterZ=0 NormalX=0 NormalY=0 NormalZ=1 AngleXU=0 Radius=1.5
    g7: Circle CenterX=46 CenterY=65.799 CenterZ=0 NormalX=0 NormalY=0 NormalZ=1 AngleXU=0 Radius=1.5
  constraints (19):
    c: Diameter(g1) = 3
    c: Diameter(g0) = 3
    c: Angle(g2,g-1) = 2.35619
    c: Symmetric(g1,g0,g2)
    c: Distance(g1,g2) = 14
    c: Distance(g1,g-2) = 46
    c: PointOnObject(g-1,g2)
    c: Coincident(g3,g-1)
    c: Perpendicular(g2,g3)
    c: Diameter(g7) = 3
    c: Diameter(g6) = 3
    c: Diameter(g5) = 3
    c: Diameter(g4) = 3
    c: Symmetric(g4,g5,g3)
    c: Symmetric(g7,g6,g2)
    c: Distance(g4,g3) = 36
    c: Distance(g6,g2) = 14
    c: Distance(g4,g-2) = 25
    c: Distance(g7,g-2) = 46
FEATURE [PartDesign::Pocket] Pocket055
  BaseFeature = -> Pocket050
  Direction = (0,0,-1)
  Length = 50
  Length2 = 5
  Profile = -> Sketch126
  ReferenceAxis = -> Sketch126 [N_Axis]
  Suppressed = false
  Type = 4
FEATURE [PartDesign::SubShapeBinder] Binder013
  BindCopyOnChange = 0
  BindMode = 0
  ClaimChildren = false
  Context = -> Part014 [Body044.Binder013.]
  Fuse = false
  MakeFace = true
  OffsetFill = false
  OffsetIntersection = false
  OffsetJoinType = 0
  OffsetOpenResult = false
  PartialLoad = false
  Relative = true
  Support = -> [Body[Pocket055.Sketch126.]]
  _Version = 2
FEATURE [PartDesign::Pocket] Pocket094
  BaseFeature = -> Pad070
  Direction = (0,0,-1)
  Length = 5
  Length2 = 5
  Profile = -> Binder013
  Suppressed = false
  Type = 1
FEATURE [PartDesign::PolarPattern] PolarPattern021
  Angle = 70
  Axis = -> Sketch001 [N_Axis]
  BaseFeature = -> Pocket055
  Mode = 0
  Occurrences = 2
  Offset = 120
  Originals = -> [Pocket]
  Reversed = true
  Suppressed = false
  TransformMode = 0
FEATURE [PartDesign::PolarPattern] PolarPattern022
  Angle = 360
  Axis = -> Sketch001 [N_Axis]
  BaseFeature = -> PolarPattern021
  Mode = 0
  Occurrences = 2
  Offset = 120
  Originals = -> [Pocket]
  Suppressed = false
  TransformMode = 0
FEATURE [PartDesign::SubShapeBinder] Binder027
  BindCopyOnChange = 0
  BindMode = 0
  ClaimChildren = false
  Context = -> Part014 [Body044.Binder027.]
  Fuse = false
  MakeFace = true
  OffsetFill = false
  OffsetIntersection = false
  OffsetJoinType = 0
  OffsetOpenResult = false
  PartialLoad = false
  Relative = true
  Support = -> [Body[Pocket.Sketch001.]]
  _Version = 2
FEATURE [PartDesign::Pocket] Pocket096
  BaseFeature = -> Pocket094
  Direction = (0,0,-1)
  Length = 5
  Length2 = 5
  Profile = -> Binder027
  Suppressed = false
  Type = 1
FEATURE [PartDesign::PolarPattern] PolarPattern023
  Angle = 110
  Axis = -> Z_Axis248
  BaseFeature = -> Pocket096
  Mode = 0
  Occurrences = 2
  Offset = 120
  Originals = -> [Pocket096]
  Suppressed = false
  TransformMode = 0
FEATURE [PartDesign::PolarPattern] PolarPattern024
  Angle = 70
  Axis = -> Z_Axis248
  BaseFeature = -> PolarPattern023
  Mode = 0
  Occurrences = 2
  Offset = 120
  Originals = -> [Pocket096]
  Reversed = true
  Suppressed = false
  TransformMode = 0
FEATURE [PartDesign::PolarPattern] PolarPattern025
  Angle = 180
  Axis = -> Z_Axis248
  BaseFeature = -> PolarPattern024
  Mode = 0
  Occurrences = 2
  Offset = 120
  Originals = -> [Pocket096]
  Suppressed = false
  TransformMode = 0
FEATURE [PartDesign::SubShapeBinder] Binder028
  BindCopyOnChange = 0
  BindMode = 0
  ClaimChildren = false
  Context = -> Part014 [Body044.Binder028.]
  Fuse = false
  MakeFace = true
  OffsetFill = false
  OffsetIntersection = false
  OffsetJoinType = 0
  OffsetOpenResult = false
  PartialLoad = false
  Relative = true
  Support = -> [Body[Pocket004.Sketch015.]]
  _Version = 2
FEATURE [PartDesign::Pocket] Pocket097
  BaseFeature = -> PolarPattern025
  Direction = (0,0,-1)
  Length = 5
  Length2 = 5
  Profile = -> Binder028
  Suppressed = false
  Type = 1
FEATURE [Sketcher::SketchObject] Sketch127
  ArcFitTolerance = 0
  AttachmentSupport = -> [XZ_Plane256]
  FullyConstrained = true
  MakeInternals = false
  MapMode = 5
  Placement = pos=(0,0,0) rot=(1,0,0;1.5708rad)
  sketch-geometry (8):
    g0: LineSegment StartX=-88 StartY=-1 StartZ=0 EndX=-79 EndY=-1 EndZ=0
    g1: LineSegment StartX=-79 StartY=-34 StartZ=0 EndX=-88 EndY=-34 EndZ=0
    g2: LineSegment StartX=-88 StartY=-34 StartZ=0 EndX=-88 EndY=-1 EndZ=0
    g3: LineSegment StartX=-79 StartY=-1 StartZ=0 EndX=-79 EndY=-3 EndZ=0
    g4: LineSegment StartX=-79 StartY=-3 StartZ=0 EndX=-86 EndY=-3 EndZ=0
    g5: LineSegment StartX=-86 StartY=-3 StartZ=0 EndX=-86 EndY=-32 EndZ=0
    g6: LineSegment StartX=-86 StartY=-32 StartZ=0 EndX=-79 EndY=-32 EndZ=0
    g7: LineSegment StartX=-79 StartY=-32 StartZ=0 EndX=-79 EndY=-34 EndZ=0
  constraints (24):
    c: Coincident(g1,g2)
    c: Coincident(g2,g0)
    c: Horizontal(g0)
    c: Horizontal(g1)
    c: Vertical(g2)
    c: DistanceY(g1,g0) = 33
    c: DistanceX(g1,g1) = 9
    c: DistanceX(g0,g-1) = 88
    c: DistanceY(g1,g-1) = 34
    c: Equal(g1,g0)
    c: Coincident(g3,g0)
    c: Vertical(g3)
    c: Coincident(g4,g3)
    c: Horizontal(g4)
    c: Coincident(g5,g4)
    c: Vertical(g5)
    c: Coincident(g6,g5)
    c: Horizontal(g6)
    c: Coincident(g7,g6)
    c: Coincident(g7,g1)
    c: Vertical(g7)
    c: Equal(g3,g7)
    c: DistanceY(g3,g3) = 2
    c: DistanceX(g0,g4) = 2
FEATURE [PartDesign::Revolution] Revolution002
  Angle = 70
  Angle2 = 60
  Axis = (1e-16,1e-16,1)
  Base = (0,0,0)
  Midplane = true
  Placement = pos=(0,0,0) rot=(1,0,0;1.5708rad)
  Profile = -> Sketch127
  ReferenceAxis = -> Z_Axis256
  Reversed = true
  Suppressed = false
  Type = 0
FEATURE [Sketcher::SketchObject] Sketch128
  ArcFitTolerance = 0
  AttachmentSupport = -> [XZ_Plane257]
  FullyConstrained = true
  MakeInternals = false
  MapMode = 5
  Placement = pos=(0,0,0) rot=(1,0,0;1.5708rad)
  sketch-geometry (8):
    g0: LineSegment StartX=-88 StartY=-1 StartZ=0 EndX=-79 EndY=-1 EndZ=0
    g1: LineSegment StartX=-79 StartY=-34 StartZ=0 EndX=-88 EndY=-34 EndZ=0
    g2: LineSegment StartX=-88 StartY=-34 StartZ=0 EndX=-88 EndY=-1 EndZ=0
    g3: LineSegment StartX=-79 StartY=-1 StartZ=0 EndX=-79 EndY=-3 EndZ=0
    g4: LineSegment StartX=-79 StartY=-3 StartZ=0 EndX=-86 EndY=-3 EndZ=0
    g5: LineSegment StartX=-86 StartY=-3 StartZ=0 EndX=-86 EndY=-32 EndZ=0
    g6: LineSegment StartX=-86 StartY=-32 StartZ=0 EndX=-79 EndY=-32 EndZ=0
    g7: LineSegment StartX=-79 StartY=-32 StartZ=0 EndX=-79 EndY=-34 EndZ=0
  constraints (24):
    c: Coincident(g1,g2)
    c: Coincident(g2,g0)
    c: Horizontal(g0)
    c: Horizontal(g1)
    c: Vertical(g2)
    c: DistanceY(g1,g0) = 33
    c: DistanceX(g1,g1) = 9
    c: DistanceX(g0,g-1) = 88
    c: DistanceY(g1,g-1) = 34
    c: Equal(g1,g0)
    c: Coincident(g3,g0)
    c: Vertical(g3)
    c: Coincident(g4,g3)
    c: Horizontal(g4)
    c: Coincident(g5,g4)
    c: Vertical(g5)
    c: Coincident(g6,g5)
    c: Horizontal(g6)
    c: Coincident(g7,g6)
    c: Coincident(g7,g1)
    c: Vertical(g7)
    c: Equal(g3,g7)
    c: DistanceY(g3,g3) = 2
    c: DistanceX(g0,g4) = 2
FEATURE [PartDesign::Revolution] Revolution003
  Angle = 30
  Angle2 = 60
  Axis = (1e-16,1e-16,1)
  Base = (0,0,0)
  Midplane = true
  Placement = pos=(0,0,0) rot=(1,0,0;1.5708rad)
  Profile = -> Sketch128
  ReferenceAxis = -> Z_Axis257
  Reversed = true
  Suppressed = false
  Type = 0
FEATURE [Part::Feature] Part__Feature1464  label="LD19_BASE"
  Placement = pos=(-9e-15,-8.62399,0) rot=(0,0,1;0rad)
  shape: bbox 53.95 x 46.29 x 3.551 mm, 34 faces (baked)
FEATURE [Part::Feature] Part__Feature1465  label="LD19_EMITTER"
  Placement = pos=(5.47382e-06,-8.59716,0) rot=(0,0,1;0rad)
  shape: bbox 39.74 x 39.74 x 11.25 mm, 29 faces (baked)
FEATURE [Part::Feature] Part__Feature1466  label="LD19_BODY"
  Placement = pos=(5.47382e-06,-8.59716,-2e-15) rot=(0,0,1;0rad)
  shape: bbox 38.52 x 38.52 x 18.7 mm, 15 faces (baked)
FEATURE [PartDesign::SubShapeBinder] Binder032
  BindCopyOnChange = 0
  BindMode = 0
  ClaimChildren = false
  Context = -> Body [Binder032.]
  Fuse = false
  MakeFace = true
  OffsetFill = false
  OffsetIntersection = false
  OffsetJoinType = 0
  OffsetOpenResult = false
  PartialLoad = false
  Relative = true
  Support = -> [LD19[Part__Feature1464.Edge77,Part__Feature1464.Edge78,Part__Feature1464.Edge73,Part__Feature1464.Edge74,Part__Feature1464.Edge75,Part__Feature1464.Edge76]]
  _Version = 2
FEATURE [PartDesign::Pocket] Pocket101
  BaseFeature = -> PolarPattern022
  Direction = (0,0,-1)
  Length = 5
  Length2 = 5
  Profile = -> Binder032
  Suppressed = false
  Type = 1
FEATURE [Sketcher::SketchObject] Sketch130
  ArcFitTolerance = 0
  AttachmentSupport = -> [XY_Plane049]
  FullyConstrained = false
  MakeInternals = false
  MapMode = 5
  sketch-geometry (6):
    g0: ArcOfCircle CenterX=0 CenterY=0 CenterZ=0 NormalX=0 NormalY=0 NormalZ=1 AngleXU=0 Radius=77.5 StartAngle=4.97117 EndAngle=7.5952
    g1: LineSegment StartX=19.8431 StartY=-22.5 StartZ=0 EndX=19.8431 EndY=22.5 EndZ=0
    g2: ArcOfCircle CenterX=0 CenterY=0 CenterZ=0 NormalX=0 NormalY=0 NormalZ=1 AngleXU=0 Radius=30 StartAngle=5.43464 EndAngle=5.43512
    g3: ArcOfCircle CenterX=0 CenterY=0 CenterZ=0 NormalX=0 NormalY=0 NormalZ=1 AngleXU=0 Radius=30 StartAngle=0.848062 EndAngle=0.848549
    g4: LineSegment StartX=19.8322 StartY=-74.9195 StartZ=0 EndX=19.8322 EndY=-22.5097 EndZ=0
    g5: LineSegment StartX=19.8322 StartY=22.5097 StartZ=0 EndX=19.8322 EndY=74.9195 EndZ=0
  constraints (16):
    c: Coincident(g0,g-1)
    c: Symmetric(g1,g1,g-1)
    c: Diameter(g0) = 155
    c: DistanceY(g1,g1) = 45
    c: Coincident(g2,g0)
    c: Coincident(g2,g1)
    c: Coincident(g3,g0)
    c: Coincident(g3,g1)
    c: Diameter(g3) = 60
    c: Coincident(g4,g0)
    c: Coincident(g4,g2)
    c: Coincident(g5,g3)
    c: Coincident(g5,g0)
    c: Vertical(g0,g0)
    c: Vertical(g2,g3)
    c: Vertical(g4)
FEATURE [PartDesign::Pad] Pad088
  Direction = (0,0,1)
  Length = 2
  Length2 = 10
  Profile = -> Sketch130
  ReferenceAxis = -> Sketch130 [N_Axis]
  Suppressed = false
  Type = 0
FEATURE [Sketcher::SketchObject] Sketch131
  ArcFitTolerance = 0
  AttachmentSupport = -> [XZ_Plane259]
  FullyConstrained = true
  MakeInternals = false
  MapMode = 5
  Placement = pos=(0,0,0) rot=(1,0,0;1.5708rad)
  sketch-geometry (4):
    g0: LineSegment StartX=-22 StartY=15 StartZ=0 EndX=22 EndY=15 EndZ=0
    g1: LineSegment StartX=22 StartY=15 StartZ=0 EndX=22 EndY=-15 EndZ=0
    g2: LineSegment StartX=22 StartY=-15 StartZ=0 EndX=-22 EndY=-15 EndZ=0
    g3: LineSegment StartX=-22 StartY=-15 StartZ=0 EndX=-22 EndY=15 EndZ=0
  constraints (10):
    c: Coincident(g0,g1)
    c: Coincident(g1,g2)
    c: Coincident(g2,g3)
    c: Coincident(g3,g0)
    c: Horizontal(g2)
    c: Vertical(g3)
    c: DistanceY(g1,g1) = 30
    c: Symmetric(g1,g0,g-1)
    c: Symmetric(g0,g0,g-2)
    c: DistanceX(g0,g0) = 44
FEATURE [PartDesign::SubShapeBinder] Binder034
  BindCopyOnChange = 0
  BindMode = 0
  ClaimChildren = false
  Context = -> Body [Binder034.]
  Fuse = false
  MakeFace = true
  OffsetFill = false
  OffsetIntersection = false
  OffsetJoinType = 0
  OffsetOpenResult = false
  PartialLoad = false
  Relative = true
  Support = -> [Part004[Body053.Pad089.Sketch131.]]
  _Version = 2
FEATURE [PartDesign::Pocket] Pocket103
  BaseFeature = -> Pocket101
  Direction = (-7e-16,-4e-16,-1)
  Length = 5
  Length2 = 5
  Profile = -> Binder034
  Reversed = true
  Suppressed = false
  Type = 1
FEATURE [PartDesign::SubShapeBinder] Binder035
  BindCopyOnChange = 0
  BindMode = 0
  ClaimChildren = false
  Context = -> Part [Body024.Binder035.]
  Fuse = false
  MakeFace = true
  OffsetFill = false
  OffsetIntersection = false
  OffsetJoinType = 0
  OffsetOpenResult = false
  PartialLoad = false
  Relative = true
  Support = -> [Part004[Body053.Pad089.Sketch131.]]
  _Version = 2
FEATURE [PartDesign::Pocket] Pocket104
  BaseFeature = -> Pad088
  Direction = (-2e-16,-8e-16,-1)
  Length = 5
  Length2 = 5
  Profile = -> Binder035
  Reversed = true
  Suppressed = false
  Type = 1
FEATURE [PartDesign::Body] Body024  label="PCB board"
  AllowCompound = false
  Group = -> [Sketch130,Pad088,Binder035,Pocket104]
  Origin = -> Origin049
  Placement = pos=(0,0,16) rot=(0,0,1;0rad)
  Tip = -> Pocket104
FEATURE [Sketcher::SketchObject] Sketch133
  ArcFitTolerance = 0
  AttachmentSupport = -> [XZ_Plane259]
  FullyConstrained = true
  MakeInternals = false
  MapMode = 5
  Placement = pos=(0,0,0) rot=(1,0,0;1.5708rad)
  sketch-geometry (4):
    g0: LineSegment StartX=-21.5 StartY=14.5 StartZ=0 EndX=21.5 EndY=14.5 EndZ=0
    g1: LineSegment StartX=21.5 StartY=14.5 StartZ=0 EndX=21.5 EndY=-14.5 EndZ=0
    g2: LineSegment StartX=21.5 StartY=-14.5 StartZ=0 EndX=-21.5 EndY=-14.5 EndZ=0
    g3: LineSegment StartX=-21.5 StartY=-14.5 StartZ=0 EndX=-21.5 EndY=14.5 EndZ=0
  constraints (10):
    c: Coincident(g0,g1)
    c: Coincident(g1,g2)
    c: Coincident(g2,g3)
    c: Coincident(g3,g0)
    c: Horizontal(g2)
    c: Vertical(g1)
    c: Symmetric(g0,g0,g-2)
    c: Symmetric(g2,g0,g-1)
    c: DistanceX(g0,g0) = 43
    c: DistanceY(g1,g1) = 29
FEATURE [PartDesign::Pad] Pad089
  Direction = (0,-1,2e-16)
  Length = 60
  Length2 = 10
  Placement = pos=(0,0,0) rot=(1,0,0;1.5708rad)
  Profile = -> Sketch133
  ReferenceAxis = -> Sketch133 [N_Axis]
  Suppressed = false
  Type = 0
FEATURE [PartDesign::Fillet] Fillet
  Base = -> Pad089 [Edge7,Edge4,Edge10,Edge12,Edge2,Edge5,Edge1,Edge8,Edge3,Edge11,Edge9,Edge6]
  BaseFeature = -> Pad089
  Placement = pos=(0,0,0) rot=(1,0,0;1.5708rad)
  Radius = 2
  SupportTransform = false
  Suppressed = false
  UseAllEdges = false
FEATURE [PartDesign::Body] Body053  label="Batterie"
  AllowCompound = false
  Group = -> [Sketch131,Sketch133,Pad089,Fillet]
  Origin = -> Origin259
  Placement = pos=(64,-2.9e-14,-36.5) rot=(0.57735,-0.57735,0.57735;4.18879rad)
  Tip = -> Fillet
FEATURE [App::Part] Part004  label="Powerpack"
  Group = -> [Body053]
  Origin = -> Origin037
  Placement = pos=(0,0,3) rot=(0,0,1;0rad)
FEATURE [PartDesign::SubShapeBinder] Binder038
  BindCopyOnChange = 0
  BindMode = 0
  ClaimChildren = false
  Context = -> Body [Binder038.]
  Fuse = false
  MakeFace = true
  OffsetFill = false
  OffsetIntersection = false
  OffsetJoinType = 0
  OffsetOpenResult = false
  PartialLoad = false
  Relative = true
  Support = -> [Part013[Body049.Pocket108.Sketch137.]]
  _Version = 2
FEATURE [PartDesign::Pocket] Pocket109
  BaseFeature = -> Pocket103
  Direction = (0,0,-1)
  Length = 5
  Length2 = 5
  Profile = -> Binder038
  Reversed = true
  Suppressed = false
  Type = 1
FEATURE [Sketcher::SketchObject] Sketch138
  ArcFitTolerance = 0
  AttachmentSupport = -> [Pocket097]
  ExternalGeometry = -> [Pocket097]
  FullyConstrained = true
  MakeInternals = false
  MapMode = 5
  Placement = pos=(0,0,0) rot=(1,0,0;3.14159rad)
  sketch-geometry (3):
    g0: LineSegment StartX=7.63834 StartY=75.3298 StartZ=0 EndX=17.2106 EndY=49.0304 EndZ=0
    g1: LineSegment StartX=17.2106 StartY=49.0304 StartZ=0 EndX=49.0304 EndY=17.2106 EndZ=0
    g2: LineSegment StartX=49.0304 StartY=17.2106 StartZ=0 EndX=75.3298 EndY=7.63834 EndZ=0
  constraints (8):
    c: Coincident(g0,g-3)
    c: Coincident(g1,g0)
    c: Coincident(g2,g1)
    c: Coincident(g2,g-4)
    c: Distance(g1) = 45
    c: Equal(g0,g2)
    c: Angle(g0,g-3) = 2.18166
    c: Angle(g-4,g2) = 2.18166
FEATURE [Sketcher::SketchObject] Sketch193
  ArcFitTolerance = 0
  FullyConstrained = false
  MakeInternals = false
  MapMode = 5
  Placement = pos=(0,0,0) rot=(1,0,0;3.14159rad)
  sketch-geometry (6):
    g0: LineSegment StartX=7.63834 StartY=75.3298 StartZ=0 EndX=17.2106 EndY=49.0304 EndZ=0
    g1: LineSegment StartX=17.2106 StartY=49.0304 StartZ=0 EndX=49.0304 EndY=17.2106 EndZ=0
    g2: LineSegment StartX=49.0304 StartY=17.2106 StartZ=0 EndX=75.3298 EndY=7.63834 EndZ=0
    g3: LineSegment StartX=7.63834 StartY=75.3298 StartZ=0 EndX=13.6383 EndY=83.8987 EndZ=0
    g4: LineSegment StartX=75.3298 StartY=7.63834 StartZ=0 EndX=83.8987 EndY=13.6383 EndZ=0
    g5: ArcOfCircle CenterX=0 CenterY=0 CenterZ=0 NormalX=0 NormalY=0 NormalZ=1 AngleXU=0 Radius=85 StartAngle=0.161148 EndAngle=1.40965
  constraints (8):
    c: Coincident(g1,g0)
    c: Coincident(g2,g1)
    c: Distance(g1) = 45
    c: Equal(g0,g2)
    c: Coincident(g3,g0)
    c: Coincident(g4,g2)
    c: Coincident(g5,g-1)
    c: Coincident(g5,g3)
FEATURE [PartDesign::Pad] Pad091
  Direction = (0,-1e-16,-1)
  Length = 3
  Length2 = 10
  Placement = pos=(0,0,0) rot=(1,0,0;3.14159rad)
  Profile = -> Sketch193
  ReferenceAxis = -> Sketch193 [N_Axis]
  Suppressed = false
  Type = 0
FEATURE [Sketcher::SketchObject] Sketch248
  ArcFitTolerance = 0
  FullyConstrained = false
  MakeInternals = false
  MapMode = 5
  Placement = pos=(0,0,0) rot=(1,0,0;3.14159rad)
  sketch-geometry (20):
    g0: LineSegment StartX=7.63834 StartY=75.3298 StartZ=0 EndX=17.2106 EndY=49.0304 EndZ=0
    g1: LineSegment StartX=17.2106 StartY=49.0304 StartZ=0 EndX=49.0304 EndY=17.2106 EndZ=0
    g2: LineSegment StartX=49.0304 StartY=17.2106 StartZ=0 EndX=75.3298 EndY=7.63834 EndZ=0
    g3: LineSegment StartX=7.63834 StartY=75.3298 StartZ=0 EndX=-32.942 EndY=68.1744 EndZ=0
    g4: LineSegment StartX=-32.942 StartY=68.1744 StartZ=0 EndX=-41.5109 EndY=74.1744 EndZ=0
    g5: LineSegment StartX=-74.1744 StartY=41.5109 StartZ=0 EndX=-68.1744 EndY=32.942 EndZ=0
    g6: LineSegment StartX=-68.1744 StartY=32.942 StartZ=0 EndX=-75.1847 EndY=-6.81529 EndZ=0
    g7: LineSegment StartX=-6.81529 StartY=-75.1847 StartZ=0 EndX=32.942 EndY=-68.1744 EndZ=0
    g8: LineSegment StartX=32.942 StartY=-68.1744 StartZ=0 EndX=41.5109 EndY=-74.1744 EndZ=0
    g9: LineSegment StartX=74.1744 StartY=-41.5109 StartZ=0 EndX=68.1744 EndY=-32.942 EndZ=0
    g10: LineSegment StartX=68.1744 StartY=-32.942 StartZ=0 EndX=75.3298 EndY=7.63834 EndZ=0
    g11: ArcOfCircle CenterX=0 CenterY=0 CenterZ=0 NormalX=0 NormalY=0 NormalZ=1 AngleXU=0 Radius=85 StartAngle=2.08101 EndAngle=2.63138
    g12: ArcOfCircle CenterX=0 CenterY=0 CenterZ=0 NormalX=0 NormalY=0 NormalZ=1 AngleXU=0 Radius=85 StartAngle=5.2226 EndAngle=5.77297
    g13: LineSegment StartX=-75.1847 StartY=-6.81529 StartZ=0 EndX=-85.7913 EndY=-17.4219 EndZ=0
    g14: LineSegment StartX=-85.7913 StartY=-17.4219 StartZ=0 EndX=-75.1847 EndY=-28.0285 EndZ=0
    g15: LineSegment StartX=-75.1847 StartY=-28.0285 StartZ=0 EndX=-64.5781 EndY=-17.4219 EndZ=0
    g16: LineSegment StartX=-64.5781 StartY=-17.4219 StartZ=0 EndX=-17.4219 EndY=-64.5781 EndZ=0
    g17: LineSegment StartX=-17.4219 StartY=-64.5781 StartZ=0 EndX=-28.0285 EndY=-75.1847 EndZ=0
    g18: LineSegment StartX=-28.0285 StartY=-75.1847 StartZ=0 EndX=-17.4219 EndY=-85.7913 EndZ=0
    g19: LineSegment StartX=-17.4219 StartY=-85.7913 StartZ=0 EndX=-6.81529 EndY=-75.1847 EndZ=0
  constraints (38):
    c: Coincident(g1,g0)
    c: Coincident(g2,g1)
    c: Distance(g1) = 45
    c: Equal(g0,g2)
    c: Coincident(g3,g0)
    c: Coincident(g4,g3)
    c: Coincident(g6,g5)
    c: Coincident(g8,g7)
    c: Coincident(g10,g9)
    c: Coincident(g10,g2)
    c: Coincident(g11,g4)
    c: Coincident(g12,g11)
    c: Coincident(g12,g8)
    c: Coincident(g12,g9)
    c: DistanceX(g6) = -75.1847
    c: DistanceY(g6) = -6.81529
    c: DistanceX(g7) = -6.81529
    c: DistanceY(g7) = -75.1847
    c: Coincident(g13,g6)
    c: Coincident(g14,g13)
    c: Coincident(g15,g14)
    c: Coincident(g16,g15)
    c: Coincident(g17,g16)
    c: Coincident(g18,g17)
    c: Coincident(g19,g18)
    c: Coincident(g19,g7)
    c: Parallel(g13,g15)
    c: Parallel(g17,g19)
    c: Parallel(g16,g14)
    c: Parallel(g16,g18)
    c: Perpendicular(g17,g18)
    c: Perpendicular(g15,g14)
    c: Equal(g15,g17)
    c: Equal(g18,g14)
    c: Equal(g13,g15)
    c: Equal(g17,g19)
    c: Distance(g14) = 15
    c: Distance(g15) = 15
FEATURE [PartDesign::Pad] Pad092
  Direction = (0,-1e-16,-1)
  Length = 3
  Length2 = 10
  Placement = pos=(0,0,0) rot=(1,0,0;3.14159rad)
  Profile = -> Sketch248
  ReferenceAxis = -> Sketch248 [N_Axis]
  Suppressed = false
  Type = 0
FEATURE [PartDesign::SubShapeBinder] Binder039
  BindCopyOnChange = 0
  BindMode = 0
  ClaimChildren = false
  Context = -> Part014 [Body093.Binder039.]
  Fuse = false
  MakeFace = true
  OffsetFill = false
  OffsetIntersection = false
  OffsetJoinType = 0
  OffsetOpenResult = false
  PartialLoad = false
  Relative = true
  Support = -> [Body[Pocket055.Sketch126.]]
  _Version = 2
FEATURE [PartDesign::Pocket] Pocket110
  BaseFeature = -> Pad092
  Direction = (0,0,-1)
  Length = 5
  Length2 = 5
  Placement = pos=(0,0,0) rot=(1,0,0;3.14159rad)
  Profile = -> Binder039
  Suppressed = false
  Type = 1
FEATURE [PartDesign::SubShapeBinder] Binder040
  BindCopyOnChange = 0
  BindMode = 0
  ClaimChildren = false
  Context = -> Part014 [Body073.Binder040.]
  Fuse = false
  MakeFace = true
  OffsetFill = false
  OffsetIntersection = false
  OffsetJoinType = 0
  OffsetOpenResult = false
  PartialLoad = false
  Relative = true
  Support = -> [Body[Pocket055.Sketch126.]]
  _Version = 2
FEATURE [PartDesign::Pocket] Pocket111
  BaseFeature = -> Pad091
  Direction = (0,0,-1)
  Length = 5
  Length2 = 5
  Placement = pos=(0,0,0) rot=(1,0,0;3.14159rad)
  Profile = -> Binder040
  Suppressed = false
  Type = 1
FEATURE [PartDesign::Body] Body073  label="Lower plate small"
  AllowCompound = false
  Group = -> [Sketch193,Pad091,Binder040,Pocket111]
  Origin = -> Origin300
  Placement = pos=(0,0,-34.2) rot=(0,0,1;0.785398rad)
  Tip = -> Pocket111
FEATURE [Sketcher::SketchObject] Sketch249
  ArcFitTolerance = 0
  AttachmentSupport = -> [Pocket052]
  ExternalGeometry = -> [Pocket052]
  FullyConstrained = false
  MakeInternals = false
  MapMode = 5
  Placement = pos=(0,0,-6) rot=(1,0,0;3.14159rad)
  sketch-geometry (18):
    g0: LineSegment StartX=-61.4103 StartY=-33.3313 StartZ=0 EndX=-64.3168 EndY=-34.0745 EndZ=0
    g1: LineSegment StartX=-64.3168 StartY=-34.0745 StartZ=0 EndX=-65.1265 EndY=-36.9631 EndZ=0
    g2: LineSegment StartX=-65.1265 StartY=-36.9631 StartZ=0 EndX=-63.0297 EndY=-39.1087 EndZ=0
    g3: LineSegment StartX=-63.0297 StartY=-39.1087 StartZ=0 EndX=-60.1232 EndY=-38.3655 EndZ=0
    g4: LineSegment StartX=-60.1232 StartY=-38.3655 StartZ=0 EndX=-59.3135 EndY=-35.4769 EndZ=0
    g5: LineSegment StartX=-59.3135 StartY=-35.4769 StartZ=0 EndX=-61.4103 EndY=-33.3313 EndZ=0
    g6: Circle [constr] CenterX=-62.22 CenterY=-36.22 CenterZ=0 NormalX=0 NormalY=0 NormalZ=1 AngleXU=0 Radius=3
    g7: LineSegment [constr] StartX=-62.22 StartY=-36.22 StartZ=0 EndX=-66.22 EndY=-40.22 EndZ=0
    g8: LineSegment [constr] StartX=-62.22 StartY=-36.22 StartZ=0 EndX=-66.22 EndY=-32.22 EndZ=0
    g9: LineSegment StartX=95.3648 StartY=-34.4404 StartZ=0 EndX=95.0313 EndY=-37.4218 EndZ=0
    g10: LineSegment StartX=95.0313 StartY=-37.4218 StartZ=0 EndX=97.4464 EndY=-39.2014 EndZ=0
    g11: LineSegment StartX=97.4464 StartY=-39.2014 StartZ=0 EndX=100.195 EndY=-37.9996 EndZ=0
    g12: LineSegment StartX=100.195 StartY=-37.9996 StartZ=0 EndX=100.529 EndY=-35.0182 EndZ=0
    g13: LineSegment StartX=100.529 StartY=-35.0182 StartZ=0 EndX=98.1136 EndY=-33.2386 EndZ=0
    g14: LineSegment StartX=98.1136 StartY=-33.2386 StartZ=0 EndX=95.3648 EndY=-34.4404 EndZ=0
    g15: Circle [constr] CenterX=97.78 CenterY=-36.22 CenterZ=0 NormalX=0 NormalY=0 NormalZ=1 AngleXU=0 Radius=3
    g16: LineSegment [constr] StartX=101.78 StartY=-32.22 StartZ=0 EndX=97.78 EndY=-36.22 EndZ=0
    g17: LineSegment [constr] StartX=97.78 StartY=-36.22 StartZ=0 EndX=101.78 EndY=-40.22 EndZ=0
  constraints (40):
    c: Coincident(g0,g1)
    c: Coincident(g1,g2)
    c: Coincident(g2,g3)
    c: Coincident(g3,g4)
    c: Coincident(g4,g5)
    c: Coincident(g5,g0)
    c: Equal(g0, g1-g5) x5
    c: PointOnObject(g0,g6)
    c: PointOnObject(g1,g6)
    c: PointOnObject(g2,g6)
    c: PointOnObject(g3,g6)
    c: PointOnObject(g4,g6)
    c: PointOnObject(g5,g6)
    c: Diameter(g6) = 6
    c: Coincident(g7,g6)
    c: Coincident(g7,g-3)
    c: Coincident(g8,g6)
    c: Coincident(g8,g-3)
    c: Equal(g8,g7)
    c: Coincident(g9,g10)
    c: Coincident(g10,g11)
    c: Coincident(g11,g12)
    c: Coincident(g12,g13)
    c: Coincident(g13,g14)
    c: Coincident(g14,g9)
    c: Equal(g9, g10-g14) x5
    c: PointOnObject(g9,g15)
    c: PointOnObject(g10,g15)
    c: PointOnObject(g11,g15)
    c: PointOnObject(g12,g15)
    c: PointOnObject(g13,g15)
    c: PointOnObject(g14,g15)
    c: Diameter(g15) = 6
    c: Coincident(g16,g-4)
    c: Coincident(g16,g15)
    c: Coincident(g17,g15)
    c: Coincident(g17,g-4)
    c: Equal(g16,g17)
    c: Perpendicular(g8,g7)
    c: Perpendicular(g16,g17)
FEATURE [PartDesign::Pad] Pad093
  BaseFeature = -> Pocket052
  Direction = (0,0,-1)
  Length = 50
  Length2 = 10
  Profile = -> Sketch249
  ReferenceAxis = -> Sketch249 [N_Axis]
  Suppressed = false
  Type = 0
FEATURE [Sketcher::SketchObject] Sketch250
  ArcFitTolerance = 0
  AttachmentSupport = -> [Pad093]
  ExternalGeometry = -> [Pad093]
  FullyConstrained = true
  MakeInternals = false
  MapMode = 5
  sketch-geometry (6):
    g0: Circle CenterX=-62.22 CenterY=36.22 CenterZ=0 NormalX=0 NormalY=0 NormalZ=1 AngleXU=0 Radius=1.5
    g1: LineSegment [constr] StartX=-66.22 StartY=32.22 StartZ=0 EndX=-62.22 EndY=36.22 EndZ=0
    g2: LineSegment [constr] StartX=-62.22 StartY=36.22 StartZ=0 EndX=-66.22 EndY=40.22 EndZ=0
    g3: Circle CenterX=97.78 CenterY=36.22 CenterZ=0 NormalX=0 NormalY=0 NormalZ=1 AngleXU=0 Radius=1.5
    g4: LineSegment [constr] StartX=101.78 StartY=32.22 StartZ=0 EndX=97.78 EndY=36.22 EndZ=0
    g5: LineSegment [constr] StartX=97.78 StartY=36.22 StartZ=0 EndX=101.78 EndY=40.22 EndZ=0
  constraints (14):
    c: Diameter(g0) = 3
    c: Coincident(g1,g-3)
    c: Coincident(g1,g0)
    c: Coincident(g2,g-3)
    c: Coincident(g2,g0)
    c: Equal(g1,g2)
    c: Diameter(g3) = 3
    c: Coincident(g4,g-4)
    c: Coincident(g4,g3)
    c: Coincident(g5,g3)
    c: Coincident(g5,g-4)
    c: Equal(g4,g5)
    c: Perpendicular(g2,g1)
    c: Perpendicular(g5,g4)
FEATURE [PartDesign::Pocket] Pocket112
  BaseFeature = -> Pad093
  Direction = (0,0,-1)
  Length = 5
  Length2 = 5
  Profile = -> Sketch250
  ReferenceAxis = -> Sketch250 [N_Axis]
  Suppressed = false
  Type = 1
FEATURE [PartDesign::SubShapeBinder] Binder044
  BindCopyOnChange = 0
  BindMode = 0
  ClaimChildren = false
  Context = -> Part014 [Body093.Binder044.]
  Fuse = false
  MakeFace = true
  OffsetFill = false
  OffsetIntersection = false
  OffsetJoinType = 0
  OffsetOpenResult = false
  PartialLoad = false
  Relative = true
  _Version = 2
FEATURE [PartDesign::Pocket] Pocket116
  BaseFeature = -> Pocket110
  Direction = (0,0,-1)
  Length = 5
  Length2 = 5
  Placement = pos=(0,0,0) rot=(1,0,0;3.14159rad)
  Profile = -> Binder044
  Suppressed = false
  Type = 1
FEATURE [PartDesign::Body] Body093  label="Lower plate large"
  AllowCompound = false
  Group = -> [Sketch248,Pad092,Binder039,Pocket110,Binder044,Pocket116]
  Origin = -> Origin340
  Placement = pos=(0,0,-34.2) rot=(0,0,1;0.785398rad)
  Tip = -> Pocket116
FEATURE [PartDesign::SubShapeBinder] Binder045
  BindCopyOnChange = 0
  BindMode = 0
  ClaimChildren = false
  Context = -> Part014 [Body044.Binder045.]
  Fuse = false
  MakeFace = true
  OffsetFill = false
  OffsetIntersection = false
  OffsetJoinType = 0
  OffsetOpenResult = false
  PartialLoad = false
  Relative = true
  _Version = 2
FEATURE [PartDesign::Pocket] Pocket117
  BaseFeature = -> Pocket097
  Direction = (0,0,-1)
  Length = 5
  Length2 = 5
  Profile = -> Binder045
  Suppressed = false
  Type = 1
FEATURE [PartDesign::Body] Body044  label="Lower plate full"
  AllowCompound = false
  Group = -> [Sketch102,Pad070,Binder013,Pocket094,Binder027,Pocket096,PolarPattern023,PolarPattern024,PolarPattern025,Binder028,Pocket097,Sketch138,Binder045,Pocket117]
  Origin = -> Origin248
  Placement = pos=(0,0,-37.2) rot=(0,0,1;0.785398rad)
  Tip = -> Pocket117
FEATURE [App::Part] Part014  label="Lower plate"
  Group = -> [Body044,Body073,Body093]
  Origin = -> Origin260
FEATURE [Part::Feature] Part__Feature1467  label="rt10"
  shape: bbox 14 x 14 x 16.7 mm, 16 faces (baked)
FEATURE [Part::Feature] Part__Feature1468  label="rt011"
  shape: bbox 5 x 5 x 0.7243 mm, 72 faces (baked)
FEATURE [Part::Feature] Part__Feature1469  label="rt012"
  shape: bbox 12.1 x 4.6 x 2.3 mm, 1904 faces (baked)
FEATURE [Part::Feature] Part__Feature1470  label="rt013"
  shape: bbox 35.56 x 16.51 x 1.6 mm, 134 faces (baked)
FEATURE [Part::Feature] Part__Feature1471  label="rt014"
  shape: bbox 4.35 x 4.35 x 4.4 mm, 6 faces (baked)
FEATURE [Part::Feature] Part__Feature1472  label="rt015"
  shape: bbox 4.35 x 4.35 x 4.4 mm, 6 faces (baked)
FEATURE [Part::Feature] Part__Feature1473  label="rt016"
  shape: bbox 12.11 x 4.605 x 2.705 mm, 1046 faces (baked)
FEATURE [Part::Feature] Part__Feature1474  label="rt017"
  shape: bbox 5 x 7 x 1.1 mm, 7 faces (baked)
FEATURE [Part::Feature] Part__Feature1475  label="rt018"
  shape: bbox 0.4 x 2 x 16.99 mm, 25 faces (baked)
FEATURE [Part::Feature] Part__Feature1476  label="rt019"
  shape: bbox 0.4 x 2 x 16.99 mm, 25 faces (baked)
FEATURE [Part::Feature] Part__Feature1477  label="rt020"
  shape: bbox 0.4 x 2 x 16.99 mm, 25 faces (baked)
FEATURE [Part::Feature] Part__Feature1478  label="rt021"
  shape: bbox 0.4 x 2 x 16.99 mm, 25 faces (baked)
FEATURE [Part::Feature] Part__Feature1479  label="rt022"
  shape: bbox 0.4 x 2 x 16.99 mm, 25 faces (baked)
FEATURE [Part::Feature] Part__Feature1480  label="rt023"
  shape: bbox 0.4 x 2 x 16.99 mm, 25 faces (baked)
FEATURE [Part::Feature] Part__Feature1481  label="rt024"
  shape: bbox 0.4 x 2 x 16.99 mm, 25 faces (baked)
FEATURE [Part::Feature] Part__Feature1482  label="rt025"
  shape: bbox 0.4 x 2 x 16.99 mm, 25 faces (baked)
FEATURE [Part::Feature] Part__Feature1483  label="rt026"
  shape: bbox 2.54 x 20.32 x 8.5 mm, 114 faces (baked)
FEATURE [Part::Feature] Part__Feature1484  label="rt027"
  shape: bbox 0.4 x 2 x 16.99 mm, 25 faces (baked)
FEATURE [Part::Feature] Part__Feature1485  label="rt028"
  shape: bbox 0.4 x 2 x 16.99 mm, 25 faces (baked)
FEATURE [Part::Feature] Part__Feature1486  label="rt029"
  shape: bbox 0.4 x 2 x 16.99 mm, 25 faces (baked)
FEATURE [Part::Feature] Part__Feature1487  label="rt030"
  shape: bbox 0.4 x 2 x 16.99 mm, 25 faces (baked)
FEATURE [Part::Feature] Part__Feature1488  label="rt031"
  shape: bbox 0.4 x 2 x 16.99 mm, 25 faces (baked)
FEATURE [Part::Feature] Part__Feature1489  label="rt032"
  shape: bbox 0.4 x 2 x 16.99 mm, 25 faces (baked)
FEATURE [Part::Feature] Part__Feature1490  label="rt033"
  shape: bbox 0.4 x 2 x 16.99 mm, 25 faces (baked)
FEATURE [Part::Feature] Part__Feature1491  label="rt034"
  shape: bbox 0.4 x 2 x 16.99 mm, 25 faces (baked)
FEATURE [Part::Feature] Part__Feature1492  label="rt035"
  shape: bbox 2.54 x 20.32 x 8.5 mm, 114 faces (baked)
FEATURE [Part::Feature] Part__Feature1495  label="rt038"
  shape: bbox 6 x 7.7 x 8.35 mm, 81 faces (baked)
FEATURE [Part::Feature] Part__Feature1501  label="rt044"
  shape: bbox 8 x 8 x 1.2 mm, 7 faces (baked)
FEATURE [Part::Feature] Part__Feature1503  label="rt046"
  shape: bbox 5 x 6 x 1 mm, 6 faces (baked)
FEATURE [Part::Feature] Part__Feature1507  label="rt050"
  shape: bbox 10 x 10 x 1.5 mm, 6 faces (baked)
FEATURE [Part::Feature] Part__Feature1510  label="rt053"
  shape: bbox 5.08 x 6.35 x 5.715 mm, 90 faces (baked)
FEATURE [Part::Feature] Part__Feature1511  label="rt054"
  shape: bbox 1.676 x 5.486 x 4.293 mm, 91 faces (baked)
FEATURE [Part::Feature] Part__Feature1512  label="rt055"
  shape: bbox 5.842 x 5.486 x 2.017 mm, 71 faces (baked)
FEATURE [Part::Feature] Part__Feature1514  label="rt057"
  shape: bbox 4 x 4 x 1 mm, 7 faces (baked)
FEATURE [Part::Feature] Part__Feature1517  label="rt060"
  shape: bbox 0.4 x 2 x 16.99 mm, 25 faces (baked)
FEATURE [Part::Feature] Part__Feature1518  label="rt061"
  shape: bbox 0.4 x 2 x 16.99 mm, 25 faces (baked)
FEATURE [Part::Feature] Part__Feature1519  label="rt062"
  shape: bbox 0.4 x 2 x 16.99 mm, 25 faces (baked)
FEATURE [Part::Feature] Part__Feature1520  label="rt063"
  shape: bbox 0.4 x 2 x 16.99 mm, 25 faces (baked)
FEATURE [Part::Feature] Part__Feature1521  label="rt064"
  shape: bbox 0.4 x 2 x 16.99 mm, 25 faces (baked)
FEATURE [Part::Feature] Part__Feature1522  label="rt065"
  shape: bbox 0.4 x 2 x 16.99 mm, 25 faces (baked)
FEATURE [Part::Feature] Part__Feature1523  label="rt066"
  shape: bbox 0.4 x 2 x 16.99 mm, 25 faces (baked)
FEATURE [Part::Feature] Part__Feature1524  label="rt067"
  shape: bbox 0.4 x 2 x 16.99 mm, 25 faces (baked)
FEATURE [Part::Feature] Part__Feature1525  label="rt068"
  shape: bbox 2.54 x 20.32 x 8.5 mm, 114 faces (baked)
FEATURE [Part::Feature] Part__Feature1527  label="rt070"
  shape: bbox 3.2 x 1.6 x 1.2 mm, 240 faces (baked)
FEATURE [Part::Feature] Part__Feature1542  label="rt085"
  shape: bbox 1.6 x 2 x 0.65 mm, 6 faces (baked)
FEATURE [Part::Feature] Part__Feature1543  label="rt086"
  shape: bbox 1.4 x 3.2 x 1 mm, 6 faces (baked)
FEATURE [Part::Feature] Part__Feature1544  label="rt087"
  shape: bbox 2.5 x 1.2 x 0.5 mm, 6 faces (baked)
FEATURE [Part::Feature] Part__Feature1547  label="rt090"
  shape: bbox 0.8 x 1.5 x 0.35 mm, 6 faces (baked)
FEATURE [Part::Feature] Part__Feature1548  label="rt091"
  shape: bbox 0.8 x 1.1 x 0.049 mm, 6 faces (baked)
FEATURE [Part::Feature] Part__Feature1549  label="rt092"
  shape: bbox 3 x 3 x 1 mm, 6 faces (baked)
FEATURE [Part::Feature] Part__Feature1576  label="rt119"
  shape: bbox 3 x 3 x 0.3 mm, 6 faces (baked)
FEATURE [Part::Feature] Part__Feature1578  label="rt121"
  shape: bbox 1.2 x 1.6 x 0.62 mm, 6 faces (baked)
FEATURE [Part::Feature] Part__Feature1585  label="rt128"
  shape: bbox 1.5 x 2.5 x 0.6 mm, 7 faces (baked)
FEATURE [Part::Feature] Part__Feature1591  label="rt134"
  shape: bbox 2 x 1.25 x 1.25 mm, 58 faces (baked)
FEATURE [Part::Feature] Part__Feature1603  label="rt146"
  shape: bbox 2 x 1.25 x 1.25 mm, 58 faces (baked)
FEATURE [Part::Feature] Part__Feature1604  label="rt147"
  shape: bbox 2 x 1.25 x 1.25 mm, 58 faces (baked)
FEATURE [Part::Feature] Part__Feature1608  label="rt151"
  shape: bbox 1.5 x 2.5 x 0.6 mm, 7 faces (baked)
FEATURE [Part::Feature] Part__Feature1615  label="rt158"
  shape: bbox 1.351 x 2.201 x 1.05 mm, 34 faces (baked)
FEATURE [Part::Feature] Part__Feature1616  label="rt159"
  shape: bbox 1.6 x 2 x 1 mm, 7 faces (baked)
FEATURE [Part::Feature] Part__Feature1617  label="rt160"
  shape: bbox 0.5 x 1 x 0.5 mm, 58 faces (baked)
FEATURE [Part::Feature] Part__Feature1700  label="rt243"
  shape: bbox 1.25 x 2 x 1.25 mm, 58 faces (baked)
FEATURE [Part::Feature] Part__Feature1702  label="rt245"
  shape: bbox 1.25 x 2 x 1.25 mm, 58 faces (baked)
FEATURE [Part::Feature] Part__Feature1703  label="rt246"
  shape: bbox 1.6 x 2 x 1 mm, 7 faces (baked)
FEATURE [Part::Feature] Part__Feature1722  label="rt265"
  shape: bbox 2 x 1.25 x 1.25 mm, 58 faces (baked)
FEATURE [Part::Feature] Part__Feature1723  label="rt266"
  shape: bbox 1.25 x 2 x 1.25 mm, 58 faces (baked)
FEATURE [Part::Feature] Part__Feature1738  label="rt281"
  shape: bbox 2 x 1.25 x 1.25 mm, 58 faces (baked)
FEATURE [Part::Feature] Part__Feature1739  label="rt282"
  shape: bbox 11.4 x 11.95 x 1.452 mm, 410 faces (baked)
FEATURE [Part::Feature] Part__Feature1740  label="rt283"
  shape: bbox 1.25 x 2 x 1.25 mm, 58 faces (baked)
FEATURE [Part::Feature] Part__Feature1741  label="rt284"
  shape: bbox 2 x 1.25 x 1.25 mm, 58 faces (baked)
FEATURE [Part::Feature] Part__Feature1742  label="rt285"
  shape: bbox 1.25 x 2 x 1.25 mm, 58 faces (baked)
FEATURE [Part::Feature] Part__Feature1750  label="rt293"
  shape: bbox 1.5 x 2.5 x 0.6 mm, 7 faces (baked)
FEATURE [Part::Feature] Part__Feature1754  label="rt297"
  shape: bbox 1.2 x 1.6 x 0.6 mm, 6 faces (baked)
FEATURE [Part::Feature] Part__Feature1757  label="rt300"
  shape: bbox 2 x 1.25 x 1.25 mm, 58 faces (baked)
FEATURE [Part::Feature] Part__Feature1758  label="rt301"
  shape: bbox 1.6 x 2 x 1 mm, 7 faces (baked)
FEATURE [Part::Feature] Part__Feature1768  label="rt311"
  shape: bbox 2.988 x 2.8 x 1.175 mm, 78 faces (baked)
FEATURE [Part::Feature] Part__Feature1772  label="rt315"
  shape: bbox 1.351 x 2.201 x 1.05 mm, 34 faces (baked)
FEATURE [Part::Feature] Part__Feature1776  label="rt319"
  shape: bbox 1.351 x 2.201 x 1.05 mm, 34 faces (baked)
FEATURE [Part::Feature] Part__Feature1777  label="rt320"
  shape: bbox 2.2 x 1.2 x 0.6 mm, 7 faces (baked)
FEATURE [Part::Feature] Part__Feature1778  label="rt321"
  shape: bbox 1.25 x 2 x 1.25 mm, 58 faces (baked)
FEATURE [Part::Feature] Part__Feature1779  label="rt322"
  shape: bbox 1.25 x 2 x 1.25 mm, 58 faces (baked)
FEATURE [Part::Feature] Part__Feature1796  label="rt339"
  shape: bbox 8.34 x 6.62 x 3.56 mm, 238 faces (baked)
FEATURE [Part::Feature] Part__Feature1823  label="rt366"
  shape: bbox 9.58 x 7.53 x 4.16 mm, 463 faces (baked)
FEATURE [Part::Feature] Part__Feature1828  label="rt371"
  shape: bbox 0.4 x 2 x 16.99 mm, 25 faces (baked)
FEATURE [Part::Feature] Part__Feature1829  label="rt372"
  shape: bbox 0.4 x 2 x 16.99 mm, 25 faces (baked)
FEATURE [Part::Feature] Part__Feature1830  label="rt373"
  shape: bbox 0.4 x 2 x 16.99 mm, 25 faces (baked)
FEATURE [Part::Feature] Part__Feature1831  label="rt374"
  shape: bbox 0.4 x 2 x 16.99 mm, 25 faces (baked)
FEATURE [Part::Feature] Part__Feature1832  label="rt375"
  shape: bbox 0.4 x 2 x 16.99 mm, 25 faces (baked)
FEATURE [Part::Feature] Part__Feature1833  label="rt376"
  shape: bbox 0.4 x 2 x 16.99 mm, 25 faces (baked)
FEATURE [Part::Feature] Part__Feature1834  label="rt377"
  shape: bbox 0.4 x 2 x 16.99 mm, 25 faces (baked)
FEATURE [Part::Feature] Part__Feature1835  label="rt378"
  shape: bbox 0.4 x 2 x 16.99 mm, 25 faces (baked)
FEATURE [Part::Feature] Part__Feature1836  label="rt379"
  shape: bbox 2.54 x 20.32 x 8.5 mm, 114 faces (baked)
FEATURE [Part::Feature] Part__Feature1837  label="rt380"
  shape: bbox 0.5 x 1 x 0.3375 mm, 36 faces (baked)
FEATURE [Part::Feature] Part__Feature1857  label="rt400"
  shape: bbox 4.718 x 3.55 x 1.549 mm, 350 faces (baked)
FEATURE [Part::Feature] Part__Feature1862  label="rt405"
  shape: bbox 2.5 x 3.2 x 0.8 mm, 47 faces (baked)
FEATURE [Part::Feature] Part__Feature1863  label="rt406"
  shape: bbox 3.21 x 1.803 x 2.385 mm, 34 faces (baked)
FEATURE [Part::Feature] Part__Feature1874  label="rt417"
  shape: bbox 4.718 x 3.55 x 1.549 mm, 350 faces (baked)
FEATURE [Part::Feature] Part__Feature1878  label="rt421"
  shape: bbox 1.803 x 3.21 x 2.385 mm, 34 faces (baked)
FEATURE [Part::Feature] Part__Feature1886  label="rt429"
  shape: bbox 0.991 x 2.312 x 1.054 mm, 10 faces (baked)
FEATURE [Part::Feature] Part__Feature1887  label="rt430"
  shape: bbox 0.991 x 2.312 x 1.054 mm, 10 faces (baked)
FEATURE [Part::Feature] Part__Feature1888  label="rt431"
  shape: bbox 3.088 x 2.999 x 2.109 mm, 16 faces (baked)
FEATURE [Part::Feature] Part__Feature1889  label="rt432"
  shape: bbox 0.617 x 2.874 x 0.051 mm, 6 faces (baked)
FEATURE [Part::Feature] Part__Feature1890  label="rt433"
  shape: bbox 0.991 x 2.312 x 1.054 mm, 10 faces (baked)
FEATURE [Part::Feature] Part__Feature1891  label="rt434"
  shape: bbox 0.991 x 2.312 x 1.054 mm, 10 faces (baked)
FEATURE [Part::Feature] Part__Feature1892  label="rt435"
  shape: bbox 3.088 x 2.999 x 2.109 mm, 16 faces (baked)
FEATURE [Part::Feature] Part__Feature1893  label="rt436"
  shape: bbox 0.617 x 2.874 x 0.051 mm, 6 faces (baked)
FEATURE [Part::Feature] Part__Feature1905  label="rt448"
  shape: bbox 35.56 x 44.45 x 1.2 mm, 64 faces (baked)
FEATURE [Part::Feature] Part__Feature1906  label="rt449"
  shape: bbox 15.5 x 16.25 x 6.3 mm, 24 faces (baked)
FEATURE [Part::Feature] Part__Feature1907  label="rt450"
  shape: bbox 23.8 x 17 x 8 mm, 20 faces (baked)
FEATURE [App::Part] rt10  label="OpenMV RT1062"
  Group = -> [Part__Feature1467,Part__Feature1468,Part__Feature1469,Part__Feature1470,Part__Feature1471,Part__Feature1472,Part__Feature1473,Part__Feature1474,Part__Feature1475,Part__Feature1476,Part__Feature1477,Part__Feature1478,Part__Feature1479,Part__Feature1480,Part__Feature1481,Part__Feature1482,Part__Feature1483,Part__Feature1484,Part__Feature1485,Part__Feature1486,Part__Feature1487,Part__Feature1488,+86 more]
  Origin = -> Origin341
  Placement = pos=(0,72.5,32.2) rot=(1,0,0;3.14159rad)
FEATURE [PartDesign::SubShapeBinder] Binder047
  BindCopyOnChange = 0
  BindMode = 0
  ClaimChildren = false
  Context = -> Part012 [Body003.Binder047.]
  Fuse = false
  MakeFace = true
  OffsetFill = false
  OffsetIntersection = false
  OffsetJoinType = 0
  OffsetOpenResult = false
  PartialLoad = false
  Relative = true
  Support = -> [Body[Pocket055.Sketch126.]]
  _Version = 2
FEATURE [PartDesign::SubShapeBinder] Binder048
  BindCopyOnChange = 0
  BindMode = 0
  ClaimChildren = false
  Context = -> Part012 [Body051.Binder048.]
  Fuse = false
  MakeFace = true
  OffsetFill = false
  OffsetIntersection = false
  OffsetJoinType = 0
  OffsetOpenResult = false
  PartialLoad = false
  Relative = true
  Support = -> [Body[Pocket055.Sketch126.]]
  _Version = 2
FEATURE [PartDesign::SubShapeBinder] Binder049
  BindCopyOnChange = 0
  BindMode = 0
  ClaimChildren = false
  Context = -> Part012 [Body052.Binder049.]
  Fuse = false
  MakeFace = true
  OffsetFill = false
  OffsetIntersection = false
  OffsetJoinType = 0
  OffsetOpenResult = false
  PartialLoad = false
  Relative = true
  Support = -> [Body[Pocket055.Sketch126.]]
  _Version = 2
FEATURE [PartDesign::Pocket] Pocket119
  BaseFeature = -> Revolution003
  Direction = (0,0,-1)
  Length = 5
  Length2 = 5
  Placement = pos=(0,0,0) rot=(1,0,0;1.5708rad)
  Profile = -> Binder049
  Suppressed = false
  Type = 1
FEATURE [PartDesign::Body] Body052  label="Outer shielding 3"
  AllowCompound = false
  Group = -> [Sketch128,Revolution003,Binder049,Pocket119]
  Origin = -> Origin257
  Placement = pos=(0,-3,0) rot=(0,0,-1;1.5708rad)
  Tip = -> Pocket119
FEATURE [PartDesign::Pocket] Pocket120
  BaseFeature = -> Revolution002
  Direction = (0,0,-1)
  Length = 5
  Length2 = 5
  Placement = pos=(0,0,0) rot=(1,0,0;1.5708rad)
  Profile = -> Binder048
  Suppressed = false
  Type = 1
FEATURE [PartDesign::Body] Body051  label="Outer shielding 2"
  AllowCompound = false
  Group = -> [Sketch127,Revolution002,Binder048,Pocket120]
  Origin = -> Origin256
  Placement = pos=(-3,1e-15,0) rot=(0,0,1;3.14159rad)
  Tip = -> Pocket120
FEATURE [PartDesign::Pocket] Pocket121
  BaseFeature = -> Revolution001
  Direction = (0,0,-1)
  Length = 5
  Length2 = 5
  Placement = pos=(0,0,0) rot=(1,0,0;1.5708rad)
  Profile = -> Binder047
  Suppressed = false
  Type = 1
FEATURE [PartDesign::SubShapeBinder] Binder050
  BindCopyOnChange = 0
  BindMode = 0
  ClaimChildren = false
  Context = -> Body [Binder050.]
  Fuse = false
  MakeFace = true
  OffsetFill = false
  OffsetIntersection = false
  OffsetJoinType = 0
  OffsetOpenResult = false
  PartialLoad = false
  Relative = true
  Support = -> [Part015[Body025.Pocket112.Sketch250.]]
  _Version = 2
FEATURE [PartDesign::Pocket] Pocket122
  BaseFeature = -> Pocket109
  Direction = (-2e-16,-2e-16,-1)
  Length = 5
  Length2 = 5
  Profile = -> Binder050
  Suppressed = false
  Type = 1
FEATURE [Sketcher::SketchObject] Sketch251
  ArcFitTolerance = 0
  FullyConstrained = false
  MakeInternals = false
  MapMode = 5
  Placement = pos=(0,0,3) rot=(0,0,1;0rad)
  sketch-geometry (2):
    g0: Circle CenterX=0 CenterY=0 CenterZ=0 NormalX=0 NormalY=0 NormalZ=1 AngleXU=0 Radius=28
    g1: Circle CenterX=0 CenterY=0 CenterZ=0 NormalX=0 NormalY=0 NormalZ=1 AngleXU=0 Radius=25.25
  constraints (2):
    c: Coincident(g1,g0)
    c: Diameter(g1) = 50.5
FEATURE [PartDesign::Pad] Pad095
  BaseFeature = -> Pad007
  Direction = (0,0,1)
  Length = 5
  Length2 = 10
  Profile = -> Sketch251
  ReferenceAxis = -> Sketch251 [N_Axis]
  Suppressed = false
  Type = 0
FEATURE [Sketcher::SketchObject] Sketch253
  ArcFitTolerance = 0
  AttachmentSupport = -> [Pad076]
  FullyConstrained = true
  MakeInternals = false
  MapMode = 5
  Placement = pos=(0,0,0) rot=(0.57735,0.57735,-0.57735;4.18879rad)
  sketch-geometry (1):
    g0: Circle CenterX=0 CenterY=0 CenterZ=0 NormalX=0 NormalY=0 NormalZ=1 AngleXU=0 Radius=1
  constraints (2):
    c: Coincident(g0,g-1)
    c: Diameter(g0) = 2
FEATURE [PartDesign::Pocket] Pocket123
  BaseFeature = -> Pad076
  Direction = (1,0,0)
  Length = 5
  Length2 = 5
  Placement = pos=(0,0,0) rot=(1,1,1;2.0944rad)
  Profile = -> Sketch253
  ReferenceAxis = -> Sketch253 [N_Axis]
  Suppressed = false
  Type = 1
FEATURE [PartDesign::Body] Body046  label="Kicker plate"
  AllowCompound = false
  Group = -> [Sketch109,Pad076,Sketch253,Pocket123]
  Origin = -> Origin251
  Placement = pos=(-71,0,-8) rot=(0,0,1;0rad)
  Tip = -> Pocket123
FEATURE [Sketcher::SketchObject] Sketch254
  ArcFitTolerance = 0
  AttachmentSupport = -> [Pad058]
  FullyConstrained = true
  MakeInternals = false
  MapMode = 5
  Placement = pos=(0,50,0) rot=(-1,0,0;1.5708rad)
  sketch-geometry (1):
    g0: Circle CenterX=0 CenterY=0 CenterZ=0 NormalX=0 NormalY=0 NormalZ=1 AngleXU=0 Radius=2
  constraints (2):
    c: Coincident(g0,g-1)
    c: Diameter(g0) = 4
FEATURE [PartDesign::Pad] Pad097
  BaseFeature = -> Pad058
  Direction = (0,1,2e-16)
  Length = 17.5
  Length2 = 10
  Placement = pos=(0,0,0) rot=(1,0,0;1.5708rad)
  Profile = -> Sketch254
  ReferenceAxis = -> Sketch254 [N_Axis]
  Suppressed = false
  Type = 0
FEATURE [PartDesign::Body] Body034  label="Dribbler motor"
  AllowCompound = false
  Group = -> [Sketch082,Pad058,Sketch254,Pad097]
  Origin = -> Origin237
  Placement = pos=(-48.5,35,17.9) rot=(0.707107,0,0.707107;3.14159rad)
  Tip = -> Pad097
FEATURE [PartDesign::SubShapeBinder] Binder051
  BindCopyOnChange = 0
  BindMode = 0
  ClaimChildren = false
  Context = -> Part011 [Body050.Binder051.]
  Fuse = false
  MakeFace = true
  OffsetFill = false
  OffsetIntersection = false
  OffsetJoinType = 0
  OffsetOpenResult = false
  PartialLoad = false
  Relative = true
  Support = -> [Part013[Body049.Pocket108.Sketch137.]]
  _Version = 2
FEATURE [PartDesign::Pocket] Pocket124
  BaseFeature = -> PolarPattern018
  Direction = (-8e-16,-4e-16,-1)
  Length = 5
  Length2 = 5
  Placement = pos=(0,0,0) rot=(1,0,0;1.5708rad)
  Profile = -> Binder051
  Suppressed = false
  Type = 1
FEATURE [PartDesign::Body] Body050  label="Dribbler support"
  AllowCompound = false
  Group = -> [Sketch121,Pad085,Sketch122,Pad086,Sketch123,Pocket048,Sketch124,Pocket049,PolarPattern018,Binder051,Pocket124]
  Origin = -> Origin255
  Placement = pos=(-48.5401,-17.9599,18) rot=(1,0,0;3.14159rad)
  Tip = -> Pocket124
FEATURE [Part::Feature] Part__Feature1908  label="HC05_Pcb"
  Placement = pos=(14.7308,31.0562,28.3016) rot=(-1,0,0;1.5708rad)
  shape: bbox 35.75 x 1.502 x 15.75 mm, 1080 faces (baked)
FEATURE [Part::Feature] Part__Feature1909  label="HC05_06"
  Placement = pos=(6.11873,45.8979,22.3358) rot=(-1,0,0;1.5708rad)
  shape: bbox 27.01 x 1.902 x 13.01 mm, 1526 faces (baked)
FEATURE [Part::Feature] Part__Feature1938  label="QSMD7.0x5.0x1.3"
  Placement = pos=(4.0775,46.698,26.3896) rot=(0,0,1;0rad)
  shape: bbox 3.51 x 0.8001 x 2 mm, 196 faces (baked)
FEATURE [App::Part] HC05_06  label="HC05_007"
  Group = -> [Part__Feature1909,Part__Feature1938]
  Origin = -> Origin347
  Placement = pos=(4.98703,-13.3397,5.96586) rot=(0,0,1;0rad)
FEATURE [Part::Feature] Part__Feature1939  label="Pines_90"
  Placement = pos=(31.1058,32.5572,34.6516) rot=(0,1,0;1.5708rad)
  shape: bbox 8.54 x 9.358 x 2.54 mm, 44 faces (baked)
FEATURE [Part::Feature] Part__Feature1940  label="Pines_091"
  Placement = pos=(31.1058,32.5572,34.6516) rot=(0,1,0;1.5708rad)
  shape: bbox 8.54 x 9.358 x 2.54 mm, 44 faces (baked)
FEATURE [Part::Feature] Part__Feature1941  label="Pines_092"
  Placement = pos=(31.1058,32.5572,34.6516) rot=(0,1,0;1.5708rad)
  shape: bbox 8.54 x 9.358 x 2.34 mm, 40 faces (baked)
FEATURE [Part::Feature] Part__Feature1942  label="Pines_093"
  Placement = pos=(31.1058,32.5572,34.6516) rot=(0,1,0;1.5708rad)
  shape: bbox 8.54 x 9.358 x 2.54 mm, 44 faces (baked)
FEATURE [Part::Feature] Part__Feature1943  label="Pines_094"
  Placement = pos=(31.1058,32.5572,34.6516) rot=(0,1,0;1.5708rad)
  shape: bbox 8.54 x 9.358 x 2.54 mm, 44 faces (baked)
FEATURE [Part::Feature] Part__Feature1944  label="Pines_095"
  Placement = pos=(31.1058,32.5572,34.6516) rot=(0,1,0;1.5708rad)
  shape: bbox 8.54 x 9.358 x 2.54 mm, 44 faces (baked)
FEATURE [App::Part] Pines_90  label="Pines_096"
  Group = -> [Part__Feature1939,Part__Feature1940,Part__Feature1941,Part__Feature1942,Part__Feature1943,Part__Feature1944]
  Origin = -> Origin348
FEATURE [Part::Feature] Part__Feature1968  label="Pulsador_Smd"
  Placement = pos=(27.6199,32.5662,22.084) rot=(0,0.707107,0.707107;3.14159rad)
  shape: bbox 3.92 x 1.91 x 2.9 mm, 86 faces (baked)
FEATURE [App::Part] HC05_Modulo  label="Module HC-05"
  Group = -> [Part__Feature1908,HC05_06,Pines_90,Part__Feature1968]
  Origin = -> Origin354
  Placement = pos=(-20.2898,-34.483,-9) rot=(1,0,0;1.5708rad)
FEATURE [Sketcher::SketchObject] Sketch256
  ArcFitTolerance = 0
  AttachmentSupport = -> [Pad095]
  ExternalGeometry = -> [Pad095]
  FullyConstrained = true
  MakeInternals = false
  MapMode = 5
  Placement = pos=(0,0,0) rot=(1,0,0;3.14159rad)
  sketch-geometry (4):
    g0: Circle CenterX=31.7128 CenterY=0 CenterZ=0 NormalX=0 NormalY=0 NormalZ=1 AngleXU=0 Radius=1.5
    g1: Circle CenterX=-31.7128 CenterY=0 CenterZ=0 NormalX=0 NormalY=0 NormalZ=1 AngleXU=0 Radius=1.5
    g2: LineSegment [constr] StartX=31.7128 StartY=0 StartZ=0 EndX=35.7128 EndY=4 EndZ=0
    g3: LineSegment [constr] StartX=31.7128 StartY=0 StartZ=0 EndX=35.7128 EndY=-4 EndZ=0
  constraints (9):
    c: PointOnObject(g0,g-1)
    c: Diameter(g0) = 3
    c: Diameter(g1) = 3
    c: Symmetric(g1,g0,g-2)
    c: Coincident(g2,g0)
    c: Coincident(g2,g-3)
    c: Coincident(g3,g0)
    c: Coincident(g3,g-3)
    c: Perpendicular(g3,g2)
FEATURE [PartDesign::Pocket] Pocket125
  BaseFeature = -> Pad095
  Direction = (0,0,1)
  Length = 5
  Length2 = 5
  Profile = -> Sketch256
  ReferenceAxis = -> Sketch256 [N_Axis]
  Suppressed = false
  Type = 1
FEATURE [PartDesign::Body] Body007  label="Mirror base"
  AllowCompound = false
  Group = -> [Sketch023,Pad007,Sketch251,Pad095,Sketch256,Pocket125]
  Origin = -> Origin024
  Placement = pos=(0,0,56) rot=(0,0,1;0rad)
  Tip = -> Pocket125
FEATURE [PartDesign::SubShapeBinder] Binder052
  BindCopyOnChange = 0
  BindMode = 0
  ClaimChildren = false
  Context = -> Part015 [Body025.Binder052.]
  Fuse = false
  MakeFace = true
  OffsetFill = false
  OffsetIntersection = false
  OffsetJoinType = 0
  OffsetOpenResult = false
  PartialLoad = false
  Relative = true
  Support = -> [Part001[Body007.Pocket125.Sketch256.]]
  _Version = 2
FEATURE [PartDesign::Pocket] Pocket126
  BaseFeature = -> Pocket112
  Direction = (2e-16,0,-1)
  Length = 5
  Length2 = 5
  Profile = -> Binder052
  Suppressed = false
  Type = 1
FEATURE [PartDesign::Body] Body025  label="Support camera "
  AllowCompound = false
  Group = -> [Sketch065,Pad044,Binder010,Pocket052,Sketch249,Pad093,Sketch250,Pocket112,Binder052,Pocket126]
  Origin = -> Origin226
  Placement = pos=(0,0,1) rot=(0,0,1;0rad)
  Tip = -> Pocket126
FEATURE [App::Part] Part015  label="Camera"
  Group = -> [rt10,Body025]
  Origin = -> Origin342
  Placement = pos=(36.22,-17.79,57) rot=(0,0,-1;4.71239rad)
FEATURE [PartDesign::SubShapeBinder] Binder053
  BindCopyOnChange = 0
  BindMode = 0
  ClaimChildren = false
  Context = -> Part012 [Body003.Binder053.]
  Fuse = false
  MakeFace = true
  OffsetFill = false
  OffsetIntersection = false
  OffsetJoinType = 0
  OffsetOpenResult = false
  PartialLoad = false
  Relative = true
  Support = -> [Part015[Body025.Pocket112.Sketch250.]]
  _Version = 2
FEATURE [PartDesign::Pocket] Pocket127
  BaseFeature = -> Pocket121
  Direction = (-2e-16,0,-1)
  Length = 60
  Length2 = 5
  Placement = pos=(0,0,0) rot=(1,0,0;1.5708rad)
  Profile = -> Binder053
  Suppressed = false
  Type = 0
FEATURE [PartDesign::Body] Body003  label="Outer shielding 1"
  AllowCompound = false
  Group = -> [Sketch016,Revolution001,Binder047,Pocket121,Binder053,Pocket127]
  Origin = -> Origin016
  Placement = pos=(1e-15,3,0) rot=(0,0,1;1.5708rad)
  Tip = -> Pocket127
FEATURE [PartDesign::SubShapeBinder] Binder054
  BindCopyOnChange = 0
  BindMode = 0
  ClaimChildren = false
  Context = -> Body [Binder054.]
  Fuse = false
  MakeFace = true
  OffsetFill = false
  OffsetIntersection = false
  OffsetJoinType = 0
  OffsetOpenResult = false
  PartialLoad = false
  Relative = true
  Support = -> [Part015[Body025.Pocket112.Sketch250.]]
  _Version = 2
FEATURE [PartDesign::Pocket] Pocket128
  BaseFeature = -> Pocket122
  Direction = (-2e-16,-2e-16,-1)
  Length = 5
  Length2 = 5
  Profile = -> Binder054
  Suppressed = false
  Type = 1
FEATURE [PartDesign::Body] Body  label="Main plate"
  AllowCompound = false
  Group = -> [Sketch,Pad,Sketch001,Pocket,PolarPattern,Sketch015,Pocket004,Sketch061,Pocket019,Binder,Pocket031,Binder005,Pocket038,Binder006,Pocket039,Binder007,Pocket040,Binder008,Pocket050,Sketch126,Pocket055,PolarPattern021,PolarPattern022,Binder032,Pocket101,Binder034,Pocket103,Binder038,Pocket109,Binder050,Pocket122,Binder054,Pocket128]
  Origin = -> Origin008
  Placement = pos=(0,0,-1) rot=(0,0,1;0.785398rad)
  Tip = -> Pocket128
FEATURE [Sketcher::SketchObject] Sketch077
  ArcFitTolerance = 0
  AttachmentSupport = -> [XY_Plane232]
  FullyConstrained = true
  MakeInternals = false
  MapMode = 5
  sketch-geometry (1):
    g0: Circle CenterX=0 CenterY=0 CenterZ=0 NormalX=0 NormalY=0 NormalZ=1 AngleXU=0 Radius=12
  constraints (2):
    c: Diameter(g0) = 24
    c: Coincident(g0,g-1)
FEATURE [PartDesign::Pad] Pad054
  Direction = (0,0,1)
  Length = 56.5
  Length2 = 28.25
  Profile = -> Sketch077
  ReferenceAxis = -> Sketch077 [N_Axis]
  Suppressed = false
  Type = 0
FEATURE [Sketcher::SketchObject] Sketch257
  ArcFitTolerance = 0
  AttachmentSupport = -> [Pad052]
  FullyConstrained = true
  MakeInternals = false
  MapMode = 5
  Placement = pos=(0,0,0) rot=(1,0,0;3.14159rad)
  sketch-geometry (1):
    g0: Circle CenterX=0 CenterY=0 CenterZ=0 NormalX=0 NormalY=0 NormalZ=1 AngleXU=0 Radius=2
  constraints (2):
    c: Coincident(g0,g-1)
    c: Diameter(g0) = 4
FEATURE [PartDesign::Pad] Pad099
  BaseFeature = -> Pad052
  Direction = (0,0,-1)
  Length = 17.5
  Length2 = 10
  Profile = -> Sketch257
  ReferenceAxis = -> Sketch257 [N_Axis]
  Suppressed = false
  Type = 0
FEATURE [PartDesign::Body] Body029  label="Moteur 1"
  AllowCompound = false
  Group = -> [Sketch075,Pad052,Sketch257,Pad099]
  Origin = -> Origin230
  Placement = pos=(-41.8711,59.7981,-2) rot=(-0.217607,0.690162,-0.690162;2.71306rad)
  Tip = -> Pad099
FEATURE [Sketcher::SketchObject] Sketch258
  ArcFitTolerance = 0
  AttachmentSupport = -> [Pad054]
  FullyConstrained = true
  MakeInternals = false
  MapMode = 5
  Placement = pos=(0,0,0) rot=(1,0,0;3.14159rad)
  sketch-geometry (1):
    g0: Circle CenterX=0 CenterY=0 CenterZ=0 NormalX=0 NormalY=0 NormalZ=1 AngleXU=0 Radius=2
  constraints (2):
    c: Coincident(g0,g-1)
    c: Diameter(g0) = 4
FEATURE [PartDesign::Pad] Pad100
  BaseFeature = -> Pad054
  Direction = (0,0,-1)
  Length = 17.5
  Length2 = 10
  Profile = -> Sketch258
  ReferenceAxis = -> Sketch258 [N_Axis]
  Suppressed = false
  Type = 0
FEATURE [PartDesign::Body] Body031  label="Moteur 2"
  AllowCompound = false
  Group = -> [Sketch077,Pad054,Sketch258,Pad100]
  Origin = -> Origin232
  Placement = pos=(41.8711,59.7981,-8) rot=(0.913318,-0.287968,-0.287968;1.66134rad)
  Tip = -> Pad100
FEATURE [Sketcher::SketchObject] Sketch259
  ArcFitTolerance = 0
  AttachmentSupport = -> [Pad051]
  FullyConstrained = true
  MakeInternals = false
  MapMode = 5
  Placement = pos=(0,0,0) rot=(1,0,0;3.14159rad)
  sketch-geometry (1):
    g0: Circle CenterX=0 CenterY=0 CenterZ=0 NormalX=0 NormalY=0 NormalZ=1 AngleXU=0 Radius=2
  constraints (2):
    c: Coincident(g0,g-1)
    c: Diameter(g0) = 4
FEATURE [PartDesign::Pad] Pad101
  BaseFeature = -> Pad051
  Direction = (0,0,-1)
  Length = 17.5
  Length2 = 10
  Profile = -> Sketch259
  ReferenceAxis = -> Sketch259 [N_Axis]
  Suppressed = false
  Type = 0
FEATURE [PartDesign::Body] Body028  label="Moteur 4"
  AllowCompound = false
  Group = -> [Sketch074,Pad051,Sketch259,Pad101]
  Origin = -> Origin229
  Placement = pos=(-41.8711,-59.7981,-8) rot=(-0.913318,0.287968,-0.287968;1.66134rad)
  Tip = -> Pad101
FEATURE [Sketcher::SketchObject] Sketch260
  ArcFitTolerance = 0
  AttachmentSupport = -> [Pad057]
  FullyConstrained = true
  MakeInternals = false
  MapMode = 5
  Placement = pos=(0,0,0) rot=(1,0,0;3.14159rad)
  sketch-geometry (1):
    g0: Circle CenterX=0 CenterY=0 CenterZ=0 NormalX=0 NormalY=0 NormalZ=1 AngleXU=0 Radius=2
  constraints (2):
    c: Coincident(g0,g-1)
    c: Diameter(g0) = 4
FEATURE [PartDesign::Pad] Pad102
  BaseFeature = -> Pad057
  Direction = (0,0,-1)
  Length = 17.5
  Length2 = 10
  Profile = -> Sketch260
  ReferenceAxis = -> Sketch260 [N_Axis]
  Suppressed = false
  Type = 0
FEATURE [PartDesign::Body] Body033  label="Moteur 3"
  AllowCompound = false
  Group = -> [Sketch081,Pad057,Sketch260,Pad102]
  Origin = -> Origin235
  Placement = pos=(41.8711,-59.7981,-8) rot=(-0.913318,-0.287968,0.287968;1.66134rad)
  Tip = -> Pad102
FEATURE [Sketcher::SketchObject] Sketch261
  ArcFitTolerance = 0
  AttachmentSupport = -> [XY_Plane357]
  FullyConstrained = true
  MakeInternals = false
  MapMode = 5
  sketch-geometry (1):
    g0: Circle CenterX=0 CenterY=0 CenterZ=0 NormalX=0 NormalY=0 NormalZ=1 AngleXU=0 Radius=17.5
  constraints (2):
    c: Coincident(g0,g-1)
    c: Diameter(g0) = 35
FEATURE [PartDesign::Pad] Pad103
  Direction = (0,0,1)
  Length = 12
  Length2 = 10
  Profile = -> Sketch261
  ReferenceAxis = -> Sketch261 [N_Axis]
  Suppressed = false
  Type = 0
FEATURE [PartDesign::Body] Body095  label="Corps"
  AllowCompound = false
  Group = -> [Sketch261,Pad103]
  Origin = -> Origin357
  Placement = pos=(0,0,24) rot=(0,0,1;0rad)
  Tip = -> Pad103
FEATURE [App::Part] LD19  label="LIDAR LD19"
  Group = -> [Part__Feature1464,Part__Feature1465,Part__Feature1466,Body095]
  Origin = -> Origin258
  Placement = pos=(0,0,13) rot=(0,0,-1;4.71239rad)
FEATURE [Sketcher::SketchObject] Sketch262
  ArcFitTolerance = 0
  AttachmentSupport = -> [YZ_Plane009]
  FullyConstrained = false
  MakeInternals = false
  MapMode = 5
  Placement = pos=(0,0,0) rot=(0.57735,0.57735,0.57735;2.0944rad)
  sketch-geometry (2):
    g0: LineSegment StartX=0 StartY=75.6915 StartZ=0 EndX=-25.0741 EndY=123.858 EndZ=0
    g1: LineSegment StartX=0 StartY=75.6915 StartZ=0 EndX=25.0741 EndY=123.858 EndZ=0
  constraints (4):
    c: PointOnObject(g0,g-2)
    c: Coincident(g1,g0)
    c: Symmetric(g0,g1,g-2)
    c: Angle(g1,g0) = 0.959931
FEATURE [Part::Feature] Part__Feature1973  label="OmniBase_Predeterminado007"
  Placement = pos=(4.80373,-0.638646,40.5) rot=(0,0,1;0rad)
  shape: bbox 44 x 43.9 x 9 mm, 104 faces (baked)
FEATURE [Part::Feature] Part__Feature1974  label="Roller_Predeterminado126"
  Placement = pos=(4.80373,20.3614,41.6192) rot=(0,0,1;0rad)
  shape: bbox 2.6 x 8.659 x 8.659 mm, 10 faces (baked)
FEATURE [Part::Feature] Part__Feature1975  label="Roller_Predeterminado127"
  Placement = pos=(-2.3787,19.0949,41.6192) rot=(0,0,1;0.349066rad)
  shape: bbox 4.664 x 8.342 x 8.659 mm, 10 faces (baked)
FEATURE [Part::Feature] Part__Feature1976  label="Roller_Predeterminado128"
  Placement = pos=(-8.69481,15.4483,41.6192) rot=(0,0,1;0.698132rad)
  shape: bbox 6.71 x 7.451 x 8.659 mm, 10 faces (baked)
FEATURE [Part::Feature] Part__Feature1977  label="Roller_Predeterminado129"
  Placement = pos=(-13.3828,9.86135,41.6192) rot=(0,0,1;1.0472rad)
  shape: bbox 7.965 x 5.765 x 8.659 mm, 10 faces (baked)
FEATURE [Part::Feature] Part__Feature1978  label="Roller_Predeterminado130"
  Placement = pos=(-15.8772,3.00797,41.6192) rot=(0,0,1;1.39626rad)
  shape: bbox 8.632 x 3.688 x 8.659 mm, 10 faces (baked)
FEATURE [Part::Feature] Part__Feature1979  label="Roller_Predeterminado131"
  Placement = pos=(-15.8772,-4.28526,41.6192) rot=(0,0,1;1.74533rad)
  shape: bbox 8.632 x 3.688 x 8.659 mm, 10 faces (baked)
FEATURE [Part::Feature] Part__Feature1980  label="Roller_Predeterminado132"
  Placement = pos=(-13.3828,-11.1386,41.6192) rot=(0,0,1;2.0944rad)
  shape: bbox 7.965 x 5.765 x 8.659 mm, 10 faces (baked)
FEATURE [Part::Feature] Part__Feature1981  label="Roller_Predeterminado133"
  Placement = pos=(-8.69481,-16.7256,41.6192) rot=(0,0,1;2.44346rad)
  shape: bbox 6.71 x 7.451 x 8.659 mm, 10 faces (baked)
FEATURE [Part::Feature] Part__Feature1982  label="Roller_Predeterminado134"
  Placement = pos=(-2.3787,-20.3722,41.6192) rot=(0,0,1;2.79253rad)
  shape: bbox 4.664 x 8.342 x 8.659 mm, 10 faces (baked)
FEATURE [Part::Feature] Part__Feature1983  label="Roller_Predeterminado135"
  Placement = pos=(4.80373,-21.6386,41.6192) rot=(0,0,1;3.14159rad)
  shape: bbox 2.6 x 8.659 x 8.659 mm, 10 faces (baked)
FEATURE [Part::Feature] Part__Feature1984  label="Roller_Predeterminado136"
  Placement = pos=(11.9862,-20.3722,41.6192) rot=(0,0,1;3.49066rad)
  shape: bbox 4.664 x 8.342 x 8.659 mm, 10 faces (baked)
FEATURE [Part::Feature] Part__Feature1985  label="Roller_Predeterminado137"
  Placement = pos=(18.3023,-16.7256,41.6192) rot=(0,0,1;3.83972rad)
  shape: bbox 6.71 x 7.451 x 8.659 mm, 10 faces (baked)
FEATURE [Part::Feature] Part__Feature1986  label="Roller_Predeterminado138"
  Placement = pos=(22.9903,-11.1386,41.6192) rot=(0,0,-1;2.0944rad)
  shape: bbox 7.965 x 5.765 x 8.659 mm, 10 faces (baked)
FEATURE [Part::Feature] Part__Feature1987  label="Roller_Predeterminado139"
  Placement = pos=(25.4847,-4.28526,41.6192) rot=(0,0,-1;1.74533rad)
  shape: bbox 8.632 x 3.688 x 8.659 mm, 10 faces (baked)
FEATURE [Part::Feature] Part__Feature1988  label="Roller_Predeterminado140"
  Placement = pos=(25.4847,3.00797,41.6192) rot=(0,0,-1;1.39626rad)
  shape: bbox 8.632 x 3.688 x 8.659 mm, 10 faces (baked)
FEATURE [Part::Feature] Part__Feature1989  label="Roller_Predeterminado141"
  Placement = pos=(22.9903,9.86135,41.6192) rot=(0,0,-1;1.0472rad)
  shape: bbox 7.965 x 5.765 x 8.659 mm, 10 faces (baked)
FEATURE [Part::Feature] Part__Feature1990  label="Roller_Predeterminado142"
  Placement = pos=(18.3023,15.4483,41.6192) rot=(0,0,-1;0.698132rad)
  shape: bbox 6.71 x 7.451 x 8.659 mm, 10 faces (baked)
FEATURE [Part::Feature] Part__Feature1991  label="Roller_Predeterminado143"
  Placement = pos=(11.9862,19.0949,41.6192) rot=(0,0,-1;0.349066rad)
  shape: bbox 4.664 x 8.342 x 8.659 mm, 10 faces (baked)
FEATURE [Part::Feature] Part__Feature1992  label="Nut_Predeterminado007"
  Placement = pos=(4.80373,-0.638646,43.5) rot=(0,0,1;1.0472rad)
  shape: bbox 13.86 x 12.93 x 2 mm, 24 faces (baked)
FEATURE [App::Part] OmniWheel057  label="OmniWheel 2"
  Group = -> [Part__Feature1973,Part__Feature1974,Part__Feature1975,Part__Feature1976,Part__Feature1977,Part__Feature1978,Part__Feature1979,Part__Feature1980,Part__Feature1981,Part__Feature1982,Part__Feature1983,Part__Feature1984,Part__Feature1985,Part__Feature1986,Part__Feature1987,Part__Feature1988,Part__Feature1989,Part__Feature1990,Part__Feature1991,Part__Feature1992]
  Origin = -> Origin358
  Placement = pos=(20.4451,37.5671,-8.7) rot=(-0.913318,0.287968,-0.287968;1.66134rad)
FEATURE [App::Part] Part006  label="Motor assembly 2"
  Group = -> [Body031,Body039,OmniWheel057]
  Origin = -> Origin039
  Placement = pos=(1,-4,0) rot=(0,0,-1;6.24828rad)
FEATURE [Part::Feature] Part__Feature1993  label="OmniBase_Predeterminado008"
  Placement = pos=(4.80373,-0.638646,40.5) rot=(0,0,1;0rad)
  shape: bbox 44 x 43.9 x 9 mm, 104 faces (baked)
FEATURE [Part::Feature] Part__Feature1994  label="Roller_Predeterminado144"
  Placement = pos=(4.80373,20.3614,41.6192) rot=(0,0,1;0rad)
  shape: bbox 2.6 x 8.659 x 8.659 mm, 10 faces (baked)
FEATURE [Part::Feature] Part__Feature1995  label="Roller_Predeterminado145"
  Placement = pos=(-2.3787,19.0949,41.6192) rot=(0,0,1;0.349066rad)
  shape: bbox 4.664 x 8.342 x 8.659 mm, 10 faces (baked)
FEATURE [Part::Feature] Part__Feature1996  label="Roller_Predeterminado146"
  Placement = pos=(-8.69481,15.4483,41.6192) rot=(0,0,1;0.698132rad)
  shape: bbox 6.71 x 7.451 x 8.659 mm, 10 faces (baked)
FEATURE [Part::Feature] Part__Feature1997  label="Roller_Predeterminado147"
  Placement = pos=(-13.3828,9.86135,41.6192) rot=(0,0,1;1.0472rad)
  shape: bbox 7.965 x 5.765 x 8.659 mm, 10 faces (baked)
FEATURE [Part::Feature] Part__Feature1998  label="Roller_Predeterminado148"
  Placement = pos=(-15.8772,3.00797,41.6192) rot=(0,0,1;1.39626rad)
  shape: bbox 8.632 x 3.688 x 8.659 mm, 10 faces (baked)
FEATURE [Part::Feature] Part__Feature1999  label="Roller_Predeterminado149"
  Placement = pos=(-15.8772,-4.28526,41.6192) rot=(0,0,1;1.74533rad)
  shape: bbox 8.632 x 3.688 x 8.659 mm, 10 faces (baked)
FEATURE [Part::Feature] Part__Feature2000  label="Roller_Predeterminado150"
  Placement = pos=(-13.3828,-11.1386,41.6192) rot=(0,0,1;2.0944rad)
  shape: bbox 7.965 x 5.765 x 8.659 mm, 10 faces (baked)
FEATURE [Part::Feature] Part__Feature2001  label="Roller_Predeterminado151"
  Placement = pos=(-8.69481,-16.7256,41.6192) rot=(0,0,1;2.44346rad)
  shape: bbox 6.71 x 7.451 x 8.659 mm, 10 faces (baked)
FEATURE [Part::Feature] Part__Feature2002  label="Roller_Predeterminado152"
  Placement = pos=(-2.3787,-20.3722,41.6192) rot=(0,0,1;2.79253rad)
  shape: bbox 4.664 x 8.342 x 8.659 mm, 10 faces (baked)
FEATURE [Part::Feature] Part__Feature2003  label="Roller_Predeterminado153"
  Placement = pos=(4.80373,-21.6386,41.6192) rot=(0,0,1;3.14159rad)
  shape: bbox 2.6 x 8.659 x 8.659 mm, 10 faces (baked)
FEATURE [Part::Feature] Part__Feature2004  label="Roller_Predeterminado154"
  Placement = pos=(11.9862,-20.3722,41.6192) rot=(0,0,1;3.49066rad)
  shape: bbox 4.664 x 8.342 x 8.659 mm, 10 faces (baked)
FEATURE [Part::Feature] Part__Feature2005  label="Roller_Predeterminado155"
  Placement = pos=(18.3023,-16.7256,41.6192) rot=(0,0,1;3.83972rad)
  shape: bbox 6.71 x 7.451 x 8.659 mm, 10 faces (baked)
FEATURE [Part::Feature] Part__Feature2006  label="Roller_Predeterminado156"
  Placement = pos=(22.9903,-11.1386,41.6192) rot=(0,0,-1;2.0944rad)
  shape: bbox 7.965 x 5.765 x 8.659 mm, 10 faces (baked)
FEATURE [Part::Feature] Part__Feature2007  label="Roller_Predeterminado157"
  Placement = pos=(25.4847,-4.28526,41.6192) rot=(0,0,-1;1.74533rad)
  shape: bbox 8.632 x 3.688 x 8.659 mm, 10 faces (baked)
FEATURE [Part::Feature] Part__Feature2008  label="Roller_Predeterminado158"
  Placement = pos=(25.4847,3.00797,41.6192) rot=(0,0,-1;1.39626rad)
  shape: bbox 8.632 x 3.688 x 8.659 mm, 10 faces (baked)
FEATURE [Part::Feature] Part__Feature2009  label="Roller_Predeterminado159"
  Placement = pos=(22.9903,9.86135,41.6192) rot=(0,0,-1;1.0472rad)
  shape: bbox 7.965 x 5.765 x 8.659 mm, 10 faces (baked)
FEATURE [Part::Feature] Part__Feature2010  label="Roller_Predeterminado160"
  Placement = pos=(18.3023,15.4483,41.6192) rot=(0,0,-1;0.698132rad)
  shape: bbox 6.71 x 7.451 x 8.659 mm, 10 faces (baked)
FEATURE [Part::Feature] Part__Feature2011  label="Roller_Predeterminado161"
  Placement = pos=(11.9862,19.0949,41.6192) rot=(0,0,-1;0.349066rad)
  shape: bbox 4.664 x 8.342 x 8.659 mm, 10 faces (baked)
FEATURE [Part::Feature] Part__Feature2012  label="Nut_Predeterminado008"
  Placement = pos=(4.80373,-0.638646,43.5) rot=(0,0,1;1.0472rad)
  shape: bbox 13.86 x 12.93 x 2 mm, 24 faces (baked)
FEATURE [App::Part] OmniWheel058  label="OmniWheel 3"
  Group = -> [Part__Feature1993,Part__Feature1994,Part__Feature1995,Part__Feature1996,Part__Feature1997,Part__Feature1998,Part__Feature1999,Part__Feature2000,Part__Feature2001,Part__Feature2002,Part__Feature2003,Part__Feature2004,Part__Feature2005,Part__Feature2006,Part__Feature2007,Part__Feature2008,Part__Feature2009,Part__Feature2010,Part__Feature2011,Part__Feature2012]
  Origin = -> Origin359
  Placement = pos=(20.4451,-37.5671,-7.4) rot=(0.913318,0.287968,0.287968;1.66134rad)
FEATURE [App::Part] Part007  label="Motor assembly 3"
  Group = -> [Body033,Body040,OmniWheel058]
  Origin = -> Origin040
  Placement = pos=(1,4,0) rot=(0,0,1;6.24828rad)
FEATURE [Part::Feature] Part__Feature2013  label="OmniBase_Predeterminado009"
  Placement = pos=(4.80373,-0.638646,40.5) rot=(0,0,1;0rad)
  shape: bbox 44 x 43.9 x 9 mm, 104 faces (baked)
FEATURE [Part::Feature] Part__Feature2014  label="Roller_Predeterminado162"
  Placement = pos=(4.80373,20.3614,41.6192) rot=(0,0,1;0rad)
  shape: bbox 2.6 x 8.659 x 8.659 mm, 10 faces (baked)
FEATURE [Part::Feature] Part__Feature2015  label="Roller_Predeterminado163"
  Placement = pos=(-2.3787,19.0949,41.6192) rot=(0,0,1;0.349066rad)
  shape: bbox 4.664 x 8.342 x 8.659 mm, 10 faces (baked)
FEATURE [Part::Feature] Part__Feature2016  label="Roller_Predeterminado164"
  Placement = pos=(-8.69481,15.4483,41.6192) rot=(0,0,1;0.698132rad)
  shape: bbox 6.71 x 7.451 x 8.659 mm, 10 faces (baked)
FEATURE [Part::Feature] Part__Feature2017  label="Roller_Predeterminado165"
  Placement = pos=(-13.3828,9.86135,41.6192) rot=(0,0,1;1.0472rad)
  shape: bbox 7.965 x 5.765 x 8.659 mm, 10 faces (baked)
FEATURE [Part::Feature] Part__Feature2018  label="Roller_Predeterminado166"
  Placement = pos=(-15.8772,3.00797,41.6192) rot=(0,0,1;1.39626rad)
  shape: bbox 8.632 x 3.688 x 8.659 mm, 10 faces (baked)
FEATURE [Part::Feature] Part__Feature2019  label="Roller_Predeterminado167"
  Placement = pos=(-15.8772,-4.28526,41.6192) rot=(0,0,1;1.74533rad)
  shape: bbox 8.632 x 3.688 x 8.659 mm, 10 faces (baked)
FEATURE [Part::Feature] Part__Feature2020  label="Roller_Predeterminado168"
  Placement = pos=(-13.3828,-11.1386,41.6192) rot=(0,0,1;2.0944rad)
  shape: bbox 7.965 x 5.765 x 8.659 mm, 10 faces (baked)
FEATURE [Part::Feature] Part__Feature2021  label="Roller_Predeterminado169"
  Placement = pos=(-8.69481,-16.7256,41.6192) rot=(0,0,1;2.44346rad)
  shape: bbox 6.71 x 7.451 x 8.659 mm, 10 faces (baked)
FEATURE [Part::Feature] Part__Feature2022  label="Roller_Predeterminado170"
  Placement = pos=(-2.3787,-20.3722,41.6192) rot=(0,0,1;2.79253rad)
  shape: bbox 4.664 x 8.342 x 8.659 mm, 10 faces (baked)
FEATURE [Part::Feature] Part__Feature2023  label="Roller_Predeterminado171"
  Placement = pos=(4.80373,-21.6386,41.6192) rot=(0,0,1;3.14159rad)
  shape: bbox 2.6 x 8.659 x 8.659 mm, 10 faces (baked)
FEATURE [Part::Feature] Part__Feature2024  label="Roller_Predeterminado172"
  Placement = pos=(11.9862,-20.3722,41.6192) rot=(0,0,1;3.49066rad)
  shape: bbox 4.664 x 8.342 x 8.659 mm, 10 faces (baked)
FEATURE [Part::Feature] Part__Feature2025  label="Roller_Predeterminado173"
  Placement = pos=(18.3023,-16.7256,41.6192) rot=(0,0,1;3.83972rad)
  shape: bbox 6.71 x 7.451 x 8.659 mm, 10 faces (baked)
FEATURE [Part::Feature] Part__Feature2026  label="Roller_Predeterminado174"
  Placement = pos=(22.9903,-11.1386,41.6192) rot=(0,0,-1;2.0944rad)
  shape: bbox 7.965 x 5.765 x 8.659 mm, 10 faces (baked)
FEATURE [Part::Feature] Part__Feature2027  label="Roller_Predeterminado175"
  Placement = pos=(25.4847,-4.28526,41.6192) rot=(0,0,-1;1.74533rad)
  shape: bbox 8.632 x 3.688 x 8.659 mm, 10 faces (baked)
FEATURE [Part::Feature] Part__Feature2028  label="Roller_Predeterminado176"
  Placement = pos=(25.4847,3.00797,41.6192) rot=(0,0,-1;1.39626rad)
  shape: bbox 8.632 x 3.688 x 8.659 mm, 10 faces (baked)
FEATURE [Part::Feature] Part__Feature2029  label="Roller_Predeterminado177"
  Placement = pos=(22.9903,9.86135,41.6192) rot=(0,0,-1;1.0472rad)
  shape: bbox 7.965 x 5.765 x 8.659 mm, 10 faces (baked)
FEATURE [Part::Feature] Part__Feature2030  label="Roller_Predeterminado178"
  Placement = pos=(18.3023,15.4483,41.6192) rot=(0,0,-1;0.698132rad)
  shape: bbox 6.71 x 7.451 x 8.659 mm, 10 faces (baked)
FEATURE [Part::Feature] Part__Feature2031  label="Roller_Predeterminado179"
  Placement = pos=(11.9862,19.0949,41.6192) rot=(0,0,-1;0.349066rad)
  shape: bbox 4.664 x 8.342 x 8.659 mm, 10 faces (baked)
FEATURE [Part::Feature] Part__Feature2032  label="Nut_Predeterminado009"
  Placement = pos=(4.80373,-0.638646,43.5) rot=(0,0,1;1.0472rad)
  shape: bbox 13.86 x 12.93 x 2 mm, 24 faces (baked)
FEATURE [App::Part] OmniWheel059  label="OmniWheel 4"
  Group = -> [Part__Feature2013,Part__Feature2014,Part__Feature2015,Part__Feature2016,Part__Feature2017,Part__Feature2018,Part__Feature2019,Part__Feature2020,Part__Feature2021,Part__Feature2022,Part__Feature2023,Part__Feature2024,Part__Feature2025,Part__Feature2026,Part__Feature2027,Part__Feature2028,Part__Feature2029,Part__Feature2030,Part__Feature2031,Part__Feature2032]
  Origin = -> Origin360
  Placement = pos=(-28.3089,-32.0608,-7.4) rot=(-0.913318,0.287968,0.287968;4.62184rad)
FEATURE [App::Part] Part008  label="Motor assembly 4"
  Group = -> [Body028,Body041,OmniWheel059]
  Origin = -> Origin041
  Placement = pos=(-1,4,0) rot=(0,0,1;0.034907rad)
FEATURE [Sketcher::SketchObject] Sketch263
  ArcFitTolerance = 0
  AttachmentSupport = -> [PolarPattern012]
  ExternalGeometry = -> [PolarPattern012]
  FullyConstrained = true
  MakeInternals = false
  MapMode = 5
  Placement = pos=(-13,0,0) rot=(0.707107,0,-0.707107;3.14159rad)
  sketch-geometry (5):
    g0: LineSegment StartX=0 StartY=0 StartZ=0 EndX=-18 EndY=0 EndZ=0
    g1: LineSegment StartX=-18 StartY=0 StartZ=0 EndX=-18 EndY=20 EndZ=0
    g2: LineSegment StartX=0 StartY=0 StartZ=0 EndX=3.6e-15 EndY=3 EndZ=0
    g3: LineSegment StartX=3.6e-15 StartY=3 StartZ=0 EndX=-14 EndY=20 EndZ=0
    g4: LineSegment StartX=-14 StartY=20 StartZ=0 EndX=-18 EndY=20 EndZ=0
  constraints (12):
    c: Coincident(g0,g-1)
    c: Coincident(g0,g-3)
    c: Coincident(g1,g0)
    c: Vertical(g1)
    c: Coincident(g2,g0)
    c: Coincident(g2,g-4)
    c: Coincident(g3,g2)
    c: Coincident(g4,g3)
    c: Coincident(g4,g1)
    c: Horizontal(g4)
    c: DistanceY(g1,g1) = 20
    c: PointOnObject(g3,g-5)
FEATURE [PartDesign::Pad] Pad104
  BaseFeature = -> PolarPattern012
  Direction = (-1,0,-2e-16)
  Length = 3
  Length2 = 10
  Placement = pos=(0,0,0) rot=(1,0,0;1.5708rad)
  Profile = -> Sketch263
  ReferenceAxis = -> Sketch263 [N_Axis]
  Suppressed = false
  Type = 0
FEATURE [Sketcher::SketchObject] Sketch264
  ArcFitTolerance = 0
  AttachmentSupport = -> [Pad104]
  ExternalGeometry = -> [Pad104]
  FullyConstrained = true
  MakeInternals = false
  MapMode = 5
  Placement = pos=(13,0,0) rot=(0.707107,0,0.707107;3.14159rad)
  sketch-geometry (5):
    g0: LineSegment StartX=0 StartY=0 StartZ=0 EndX=18 EndY=-2e-15 EndZ=0
    g1: LineSegment StartX=18 StartY=-2e-15 StartZ=0 EndX=18 EndY=20 EndZ=0
    g2: LineSegment StartX=0 StartY=0 StartZ=0 EndX=0 EndY=3 EndZ=0
    g3: LineSegment StartX=0 StartY=3 StartZ=0 EndX=14 EndY=20 EndZ=0
    g4: LineSegment StartX=14 StartY=20 StartZ=0 EndX=18 EndY=20 EndZ=0
  constraints (12):
    c: Coincident(g0,g-1)
    c: Coincident(g0,g-5)
    c: Coincident(g1,g0)
    c: Vertical(g1)
    c: Coincident(g2,g0)
    c: Coincident(g2,g-3)
    c: Coincident(g3,g2)
    c: PointOnObject(g3,g-4)
    c: Coincident(g4,g3)
    c: Coincident(g4,g1)
    c: Horizontal(g4)
    c: DistanceY(g1,g1) = 20
FEATURE [PartDesign::Pad] Pad105
  BaseFeature = -> Pad104
  Direction = (1,0,-2e-16)
  Length = 3
  Length2 = 10
  Placement = pos=(0,0,0) rot=(1,0,0;1.5708rad)
  Profile = -> Sketch264
  ReferenceAxis = -> Sketch264 [N_Axis]
  Suppressed = false
  Type = 0
FEATURE [PartDesign::Body] Body038  label="Moteur support 1"
  AllowCompound = false
  Group = -> [Sketch084,Pad062,Sketch085,Pad063,Sketch086,Pocket029,Sketch087,Pocket030,PolarPattern012,Sketch263,Pad104,Sketch264,Pad105]
  Origin = -> Origin241
  Placement = pos=(-43.5918,62.2556,-2) rot=(0,0,1;0.610865rad)
  Tip = -> Pad105
FEATURE [App::Part] Part005  label="Motor assembly 1"
  Group = -> [OmniWheel054,Body029,Body038]
  Origin = -> Origin038
  Placement = pos=(-1,-4,-6) rot=(0,0,-1;0.034907rad)
FEATURE [App::Part] Part003  label="Powertrain"
  Group = -> [Part005,Part006,Part007,Part008]
  Origin = -> Origin034
  Placement = pos=(0,0,-11) rot=(0,0,1;0rad)
FEATURE [Sketcher::SketchObject] Sketch021
  ArcFitTolerance = 0
  AttachmentSupport = -> [XY_Plane023]
  FullyConstrained = true
  MakeInternals = false
  MapMode = 5
  sketch-geometry (2):
    g0: Circle CenterX=0 CenterY=0 CenterZ=0 NormalX=0 NormalY=0 NormalZ=1 AngleXU=0 Radius=23
    g1: Circle CenterX=0 CenterY=0 CenterZ=0 NormalX=0 NormalY=0 NormalZ=1 AngleXU=0 Radius=25
  constraints (4):
    c: Coincident(g0,g-1)
    c: Diameter(g0) = 46
    c: Coincident(g1,g0)
    c: Diameter(g1) = 50
FEATURE [PartDesign::Pad] Pad006
  Direction = (0,0,1)
  Length = 63.4
  Length2 = 10
  Profile = -> Sketch021
  ReferenceAxis = -> Sketch021 [N_Axis]
  Reversed = true
  Suppressed = false
  Type = 0
FEATURE [PartDesign::Body] Body006  label="Mirror protection"
  AllowCompound = false
  Group = -> [Sketch021,Pad006]
  Origin = -> Origin023
  Placement = pos=(0,0,123.4) rot=(0,0,1;0rad)
  Tip = -> Pad006
FEATURE [Sketcher::SketchObject] Sketch265
  ArcFitTolerance = 0
  AttachmentSupport = -> [Revolution]
  FullyConstrained = true
  MakeInternals = false
  MapMode = 5
  Placement = pos=(0,5.37e-14,122) rot=(0,0,1;3.14159rad)
  sketch-geometry (1):
    g0: Circle CenterX=0 CenterY=0 CenterZ=0 NormalX=0 NormalY=0 NormalZ=1 AngleXU=0 Radius=60
  constraints (2):
    c: Coincident(g0,g-1)
    c: Diameter(g0) = 120
FEATURE [PartDesign::Pad] Pad106
  BaseFeature = -> Revolution
  Direction = (0,0,1)
  Length = 3
  Length2 = 10
  Placement = pos=(0,0,0) rot=(1,0,0;1.5708rad)
  Profile = -> Sketch265
  ReferenceAxis = -> Sketch265 [N_Axis]
  Suppressed = false
  Type = 0
FEATURE [Sketcher::SketchObject] Sketch266
  ArcFitTolerance = 0
  AttachmentSupport = -> [Pad106]
  FullyConstrained = true
  MakeInternals = false
  MapMode = 5
  Placement = pos=(0,-3.37e-14,125) rot=(0,0,1;3.14159rad)
  sketch-geometry (5):
    g0: Circle CenterX=0 CenterY=0 CenterZ=0 NormalX=0 NormalY=0 NormalZ=1 AngleXU=0 Radius=3
    g1: Circle CenterX=-32 CenterY=0 CenterZ=0 NormalX=0 NormalY=0 NormalZ=1 AngleXU=0 Radius=3
    g2: Circle CenterX=32 CenterY=0 CenterZ=0 NormalX=0 NormalY=0 NormalZ=1 AngleXU=0 Radius=3
    g3: Circle CenterX=-44 CenterY=0 CenterZ=0 NormalX=0 NormalY=0 NormalZ=1 AngleXU=0 Radius=2
    g4: Circle CenterX=44 CenterY=0 CenterZ=0 NormalX=0 NormalY=0 NormalZ=1 AngleXU=0 Radius=2
  constraints (12):
    c: Coincident(g0,g-1)
    c: Diameter(g0) = 6
    c: PointOnObject(g1,g-1)
    c: Symmetric(g1,g2,g-2)
    c: Diameter(g1) = 6
    c: Diameter(g2) = 6
    c: DistanceX(g1,g0) = 32
    c: PointOnObject(g3,g-1)
    c: Diameter(g3) = 4
    c: Diameter(g4) = 4
    c: DistanceX(g3,g0) = 44
    c: Symmetric(g3,g4,g-2)
FEATURE [PartDesign::Pocket] Pocket129
  BaseFeature = -> Pad106
  Direction = (0,3e-16,-1)
  Length = 3
  Length2 = 5
  Placement = pos=(0,0,0) rot=(1,0,0;1.5708rad)
  Profile = -> Sketch266
  ReferenceAxis = -> Sketch266 [N_Axis]
  Suppressed = false
  Type = 0
FEATURE [Sketcher::SketchObject] Sketch267
  ArcFitTolerance = 0
  AttachmentSupport = -> [Pocket129]
  FullyConstrained = true
  MakeInternals = false
  MapMode = 5
  Placement = pos=(0,-3.37e-14,125) rot=(0,0,1;3.14159rad)
  sketch-geometry (1):
    g0: Circle CenterX=0 CenterY=0 CenterZ=0 NormalX=0 NormalY=0 NormalZ=1 AngleXU=0 Radius=1.5
  constraints (2):
    c: Coincident(g0,g-1)
    c: Diameter(g0) = 3
FEATURE [PartDesign::Pocket] Pocket130
  BaseFeature = -> Pocket129
  Direction = (0,3e-16,-1)
  Length = 5
  Length2 = 5
  Placement = pos=(0,0,0) rot=(1,0,0;1.5708rad)
  Profile = -> Sketch267
  ReferenceAxis = -> Sketch267 [N_Axis]
  Suppressed = false
  Type = 1
FEATURE [Sketcher::SketchObject] Sketch268
  ArcFitTolerance = 0
  AttachmentSupport = -> [XY_Plane361]
  FullyConstrained = true
  MakeInternals = false
  MapMode = 5
  sketch-geometry (3):
    g0: Circle CenterX=0 CenterY=0 CenterZ=0 NormalX=0 NormalY=0 NormalZ=1 AngleXU=0 Radius=4
    g1: LineSegment StartX=-1.24599 StartY=1.5 StartZ=0 EndX=1.24599 EndY=1.5 EndZ=0
    g2: ArcOfCircle CenterX=0 CenterY=0 CenterZ=0 NormalX=0 NormalY=0 NormalZ=1 AngleXU=0 Radius=1.95 StartAngle=2.26396 EndAngle=7.16082
  constraints (8):
    c: Coincident(g0,g-1)
    c: Diameter(g0) = 8
    c: Horizontal(g1)
    c: Coincident(g2,g0)
    c: Coincident(g2,g1)
    c: Coincident(g2,g1)
    c: Diameter(g2) = 3.9
    c: DistanceY(g0,g1) = 1.5
FEATURE [PartDesign::Pad] Pad107
  Direction = (0,0,1)
  Length = 9.5
  Length2 = 10
  Profile = -> Sketch268
  ReferenceAxis = -> Sketch268 [N_Axis]
  Suppressed = false
  Type = 0
FEATURE [Sketcher::SketchObject] Sketch269
  ArcFitTolerance = 0
  AttachmentSupport = -> [Pad107]
  ExternalGeometry = -> [Pad107]
  FullyConstrained = true
  MakeInternals = false
  MapMode = 5
  Placement = pos=(0,0,9.5) rot=(0,0,1;0rad)
  sketch-geometry (1):
    g0: Circle CenterX=0 CenterY=0 CenterZ=0 NormalX=0 NormalY=0 NormalZ=1 AngleXU=0 Radius=7.5
  constraints (2):
    c: Coincident(g0,g-3)
    c: Diameter(g0) = 15
FEATURE [PartDesign::Pad] Pad108
  BaseFeature = -> Pad107
  Direction = (0,0,1)
  Length = 10
  Length2 = 10
  Profile = -> Sketch269
  ReferenceAxis = -> Sketch269 [N_Axis]
  Suppressed = false
  Type = 0
FEATURE [Sketcher::SketchObject] Sketch270
  ArcFitTolerance = 0
  AttachmentSupport = -> [XZ_Plane361]
  FullyConstrained = true
  MakeInternals = false
  MapMode = 5
  Placement = pos=(0,0,0) rot=(1,0,0;1.5708rad)
  sketch-geometry (1):
    g0: Circle CenterX=0 CenterY=2.5 CenterZ=0 NormalX=0 NormalY=0 NormalZ=1 AngleXU=0 Radius=1.5
  constraints (3):
    c: PointOnObject(g0,g-2)
    c: Diameter(g0) = 3
    c: DistanceY(g-1,g0) = 2.5
FEATURE [PartDesign::Pocket] Pocket131
  BaseFeature = -> Pad108
  Direction = (0,1,-2e-16)
  Length = 5
  Length2 = 5
  Profile = -> Sketch270
  ReferenceAxis = -> Sketch270 [N_Axis]
  Suppressed = false
  Type = 1
FEATURE [PartDesign::Body] Body096  label="Adaptateur 1"
  AllowCompound = false
  Group = -> [Sketch268,Pad107,Sketch269,Pad108,Sketch270,Pocket131]
  Origin = -> Origin361
  Placement = pos=(-44.5,20.5,19) rot=(0,0.707107,0.707107;3.14159rad)
  Tip = -> Pocket131
FEATURE [Sketcher::SketchObject] Sketch274
  ArcFitTolerance = 0
  AttachmentSupport = -> [Pocket130]
  ExternalGeometry = -> [Pocket130]
  FullyConstrained = false
  MakeInternals = false
  MapMode = 5
  Placement = pos=(0,-3.29e-14,122) rot=(1,0,0;3.14159rad)
  sketch-geometry (14):
    g0: LineSegment StartX=-29.1045 StartY=-0.958487 StartZ=0 EndX=-29.7222 EndY=2.02832 EndZ=0
    g1: LineSegment StartX=-29.7222 StartY=2.02832 StartZ=0 EndX=-32.6177 EndY=2.9868 EndZ=0
    g2: LineSegment StartX=-32.6177 StartY=2.9868 StartZ=0 EndX=-34.8955 EndY=0.958487 EndZ=0
    g3: LineSegment StartX=-34.8955 StartY=0.958487 StartZ=0 EndX=-34.2778 EndY=-2.02832 EndZ=0
    g4: LineSegment StartX=-34.2778 StartY=-2.02832 StartZ=0 EndX=-31.3823 EndY=-2.9868 EndZ=0
    g5: LineSegment StartX=-31.3823 StartY=-2.9868 StartZ=0 EndX=-29.1045 EndY=-0.958487 EndZ=0
    g6: Circle [constr] CenterX=-32 CenterY=1.1e-15 CenterZ=0 NormalX=0 NormalY=0 NormalZ=1 AngleXU=0 Radius=3.05
    g7: LineSegment StartX=34.4331 StartY=-1.8391 StartZ=0 EndX=34.8093 EndY=1.18762 EndZ=0
    g8: LineSegment StartX=34.8093 StartY=1.18762 StartZ=0 EndX=32.3761 EndY=3.02672 EndZ=0
    g9: LineSegment StartX=32.3761 StartY=3.02672 StartZ=0 EndX=29.5669 EndY=1.8391 EndZ=0
    g10: LineSegment StartX=29.5669 StartY=1.8391 StartZ=0 EndX=29.1907 EndY=-1.18762 EndZ=0
    g11: LineSegment StartX=29.1907 StartY=-1.18762 StartZ=0 EndX=31.6239 EndY=-3.02672 EndZ=0
    g12: LineSegment StartX=31.6239 StartY=-3.02672 StartZ=0 EndX=34.4331 EndY=-1.8391 EndZ=0
    g13: Circle [constr] CenterX=32 CenterY=0 CenterZ=0 NormalX=0 NormalY=0 NormalZ=1 AngleXU=0 Radius=3.05
  constraints (29):
    c: Coincident(g0,g1)
    c: Coincident(g1,g2)
    c: Coincident(g2,g3)
    c: Coincident(g3,g4)
    c: Coincident(g4,g5)
    c: Coincident(g5,g0)
    c: Equal(g0, g1-g5) x5
    c: PointOnObject(g0,g6)
    c: PointOnObject(g1,g6)
    c: PointOnObject(g2,g6)
    c: PointOnObject(g3,g6)
    c: PointOnObject(g4,g6)
    c: PointOnObject(g5,g6)
    c: Coincident(g6,g-3)
    c: Coincident(g7,g8)
    c: Coincident(g8,g9)
    c: Coincident(g9,g10)
    c: Coincident(g10,g11)
    c: Coincident(g11,g12)
    c: Coincident(g12,g7)
    c: Equal(g7, g8-g12) x5
    c: PointOnObject(g7,g13)
    c: PointOnObject(g8,g13)
    c: PointOnObject(g9,g13)
    c: PointOnObject(g10,g13)
    c: PointOnObject(g11,g13)
    c: PointOnObject(g12,g13)
    c: Diameter(g6) = 6.1
    c: Diameter(g13) = 6.1
FEATURE [PartDesign::Pad] Pad111
  BaseFeature = -> Pocket130
  Direction = (0,0,-1)
  Length = 73.4
  Length2 = 10
  Placement = pos=(0,0,0) rot=(1,0,0;1.5708rad)
  Profile = -> Sketch274
  ReferenceAxis = -> Sketch274 [N_Axis]
  Suppressed = false
  Type = 0
FEATURE [PartDesign::Body] Body001  label="Mirror"
  AllowCompound = false
  Group = -> [Sketch005,Revolution,Sketch262,Sketch265,Pad106,Sketch266,Pocket129,Sketch267,Pocket130,Sketch274,Pad111]
  Origin = -> Origin009
  Placement = pos=(0,0,-0.6) rot=(0,0,1;0rad)
  Tip = -> Pad111
FEATURE [App::Part] Part001  label="Mirror assembly"
  Group = -> [Body007,Body001,Body006]
  Origin = -> Origin025
  Placement = pos=(0,0,10) rot=(0,0,1;4.71239rad)
FEATURE [Sketcher::SketchObject] Sketch277
  ArcFitTolerance = 0
  AttachmentSupport = -> [Pad059]
  FullyConstrained = true
  MakeInternals = false
  MapMode = 5
  Placement = pos=(0,0,0) rot=(1,0,0;1.5708rad)
  sketch-geometry (1):
    g0: Circle CenterX=0 CenterY=0 CenterZ=0 NormalX=0 NormalY=0 NormalZ=1 AngleXU=0 Radius=2.25
  constraints (2):
    c: Coincident(g0,g-1)
    c: Diameter(g0) = 4.5
FEATURE [PartDesign::Pad] Pad114
  BaseFeature = -> Pad059
  Direction = (0,-1,2e-16)
  Length = 5
  Length2 = 10
  Placement = pos=(0,0,0) rot=(1,0,0;1.5708rad)
  Profile = -> Sketch277
  ReferenceAxis = -> Sketch277 [N_Axis]
  Suppressed = false
  Type = 0
FEATURE [Sketcher::SketchObject] Sketch278
  ArcFitTolerance = 0
  AttachmentSupport = -> [XY_Plane365]
  FullyConstrained = true
  MakeInternals = false
  MapMode = 5
  sketch-geometry (11):
    g0: LineSegment StartX=13.4834 StartY=6.80799 StartZ=0 EndX=29.8226 EndY=-18.3521 EndZ=0
    g1: LineSegment StartX=-10 StartY=-11 StartZ=0 EndX=-10 EndY=-6 EndZ=0
    g2: LineSegment StartX=-10 StartY=-6 StartZ=0 EndX=-18 EndY=-6 EndZ=0
    g3: LineSegment StartX=-16 StartY=-4 StartZ=0 EndX=-3.15946 EndY=-4 EndZ=0
    g4: LineSegment StartX=10.07 StartY=-4.4605 StartZ=0 EndX=22.2745 EndY=-23.2539 EndZ=0
    g5: LineSegment StartX=22.2745 StartY=-23.2539 StartZ=0 EndX=29.8226 EndY=-18.3521 EndZ=0
    g6: LineSegment StartX=3 StartY=0 StartZ=0 EndX=13.4834 EndY=6.80799 EndZ=0
    g7: LineSegment StartX=-10 StartY=-11 StartZ=0 EndX=0 EndY=-11 EndZ=0
    g8: LineSegment StartX=0 StartY=-11 StartZ=0 EndX=10.07 EndY=-4.4605 EndZ=0
    g9: LineSegment StartX=-18 StartY=-6 StartZ=0 EndX=-16 EndY=-4 EndZ=0
    g10: LineSegment StartX=-3.15946 StartY=-4 StartZ=0 EndX=3 EndY=0 EndZ=0
  constraints (33):
    c: Vertical(g1)
    c: DistanceY(g1,g1) = 5
    c: Coincident(g2,g1)
    c: Horizontal(g2)
    c: DistanceX(g2,g2) = 8
    c: Coincident(g5,g4)
    c: Coincident(g5,g0)
    c: Perpendicular(g0,g5)
    c: Perpendicular(g4,g5)
    c: Distance(g0) = 30
    c: PointOnObject(g6,g-1)
    c: Coincident(g6,g0)
    c: Parallel(g6,g5)
    c: Distance(g5) = 9
    c: Coincident(g7,g1)
    c: Horizontal(g7)
    c: Coincident(g8,g7)
    c: Coincident(g4,g8)
    c: Parallel(g6,g8)
    c: DistanceX(g7,g7) = 10
    c: Distance(g6) = 12.5
    c: DistanceY(g1) = -6
    c: Coincident(g9,g2)
    c: Coincident(g9,g3)
    c: Angle(g9,g3) = 2.35619
    c: Horizontal(g3)
    c: Coincident(g10,g6)
    c: Parallel(g10,g6)
    c: DistanceX(g-1,g6) = 3
    c: Angle(g8,g7) = 2.56563
    c: DistanceY(g3,g-1) = 4
    c: Coincident(g3,g10)
    c: DistanceX(g1,g-1) = 10
FEATURE [PartDesign::Pad] Pad115
  Direction = (0,0,1)
  Length = 2.5
  Length2 = 10
  Profile = -> Sketch278
  ReferenceAxis = -> Sketch278 [N_Axis]
  Suppressed = false
  Type = 0
FEATURE [Sketcher::SketchObject] Sketch284
  ArcFitTolerance = 0
  AttachmentSupport = -> [Pad114]
  FullyConstrained = true
  MakeInternals = false
  MapMode = 5
  Placement = pos=(0,50.5,0) rot=(-1,0,0;1.5708rad)
  sketch-geometry (1):
    g0: Circle CenterX=0 CenterY=0 CenterZ=0 NormalX=0 NormalY=0 NormalZ=1 AngleXU=0 Radius=2.25
  constraints (2):
    c: Coincident(g0,g-1)
    c: Diameter(g0) = 4.5
FEATURE [PartDesign::Pad] Pad119
  BaseFeature = -> Pad114
  Direction = (0,1,2e-16)
  Length = 21
  Length2 = 10
  Placement = pos=(0,0,0) rot=(1,0,0;1.5708rad)
  Profile = -> Sketch284
  ReferenceAxis = -> Sketch284 [N_Axis]
  Suppressed = false
  Type = 0
FEATURE [PartDesign::Body] Body035  label="Dribbler roll"
  AllowCompound = false
  Group = -> [Sketch083,Pad059,Sketch277,Pad114,Sketch284,Pad119]
  Origin = -> Origin238
  Placement = pos=(-76,30,1) rot=(1,0,0;3.14159rad)
  Tip = -> Pad119
FEATURE [Sketcher::SketchObject] Sketch285
  ArcFitTolerance = 0
  AttachmentSupport = -> [XY_Plane368]
  FullyConstrained = true
  MakeInternals = false
  MapMode = 5
  sketch-geometry (4):
    g0: LineSegment StartX=-65 StartY=10 StartZ=0 EndX=-32 EndY=10 EndZ=0
    g1: LineSegment StartX=-32 StartY=10 StartZ=0 EndX=-32 EndY=-10 EndZ=0
    g2: LineSegment StartX=-32 StartY=-10 StartZ=0 EndX=-65 EndY=-10 EndZ=0
    g3: LineSegment StartX=-65 StartY=-10 StartZ=0 EndX=-65 EndY=10 EndZ=0
  constraints (11):
    c: Coincident(g0,g1)
    c: Coincident(g1,g2)
    c: Coincident(g2,g3)
    c: Coincident(g3,g0)
    c: Horizontal(g0)
    c: Horizontal(g2)
    c: Vertical(g1)
    c: Symmetric(g2,g0,g-1)
    c: DistanceX(g0,g0) = 33
    c: DistanceY(g3,g3) = 20
    c: DistanceX(g0,g-1) = 32
FEATURE [PartDesign::Pad] Pad120
  Direction = (0,0,1)
  Length = 20
  Length2 = 10
  Profile = -> Sketch285
  ReferenceAxis = -> Sketch285 [N_Axis]
  Suppressed = false
  Type = 0
FEATURE [PartDesign::Body] Body102  label="Kicker body"
  AllowCompound = false
  Group = -> [Sketch285,Pad120]
  Origin = -> Origin368
  Placement = pos=(-2,0,-18) rot=(0,0,1;0rad)
  Tip = -> Pad120
FEATURE [App::Part] Part013  label="Kicker"
  Group = -> [Body046,Body102]
  Origin = -> Origin249
  Placement = pos=(4,-2.9e-15,-23) rot=(1,0,0;3.14159rad)
FEATURE [App::Part] Part012  label="Shielding"
  Group = -> [Body003,Body051,Body052,Part013]
  Origin = -> Origin247
FEATURE [Part::Cylinder] Cylinder  label="Cylindre"
  Angle = 360
  AttacherType = Attacher::AttachEngine3D
  FirstAngle = 0
  Height = 23
  Placement = pos=(-72,30,2) rot=(1,0,0;1.5708rad)
  Radius = 9
  SecondAngle = 0
FEATURE [Part::FeaturePython] Tube  # WARN: FeaturePython — macro-defined, semantics opaque (R4)
  AttacherType = Attacher::AttachEngine3D
  Height = 20.5
  InnerRadius = 8
  OuterRadius = 9
  Placement = pos=(-72,-7,2) rot=(0,0.707107,-0.707107;3.14159rad)
FEATURE [PartDesign::SubShapeBinder] Binder058
  BindCopyOnChange = 0
  BindMode = 0
  ClaimChildren = false
  Context = -> Part011 [Body121.Binder058.]
  Fuse = false
  MakeFace = true
  OffsetFill = false
  OffsetIntersection = false
  OffsetJoinType = 0
  OffsetOpenResult = false
  PartialLoad = false
  Relative = true
  _Version = 2
FEATURE [Sketcher::SketchObject] Sketch341
  ArcFitTolerance = 0
  AttachmentSupport = -> [XY_Plane405]
  FullyConstrained = true
  MakeInternals = false
  MapMode = 5
  sketch-geometry (11):
    g0: LineSegment StartX=13.4834 StartY=6.80799 StartZ=0 EndX=29.8226 EndY=-18.3521 EndZ=0
    g1: LineSegment StartX=-10 StartY=-17.5 StartZ=0 EndX=-10 EndY=-12.5 EndZ=0
    g2: LineSegment StartX=-10 StartY=-12.5 StartZ=0 EndX=-18 EndY=-12.5 EndZ=0
    g3: LineSegment StartX=-16 StartY=-10.5 StartZ=0 EndX=-13.1686 EndY=-10.5 EndZ=0
    g4: LineSegment StartX=10.3693 StartY=-4.92144 StartZ=0 EndX=22.2745 EndY=-23.2539 EndZ=0
    g5: LineSegment StartX=22.2745 StartY=-23.2539 StartZ=0 EndX=29.8226 EndY=-18.3521 EndZ=0
    g6: LineSegment StartX=3 StartY=0 StartZ=0 EndX=13.4834 EndY=6.80799 EndZ=0
    g7: LineSegment StartX=-10 StartY=-17.5 StartZ=0 EndX=-9 EndY=-17.5 EndZ=0
    g8: LineSegment StartX=-9 StartY=-17.5 StartZ=0 EndX=10.3693 EndY=-4.92144 EndZ=0
    g9: LineSegment StartX=-18 StartY=-12.5 StartZ=0 EndX=-16 EndY=-10.5 EndZ=0
    g10: LineSegment StartX=-13.1686 StartY=-10.5 StartZ=0 EndX=3 EndY=0 EndZ=0
  constraints (33):
    c: Vertical(g1)
    c: DistanceY(g1,g1) = 5
    c: Coincident(g2,g1)
    c: Horizontal(g2)
    c: DistanceX(g2,g2) = 8
    c: Coincident(g5,g4)
    c: Coincident(g5,g0)
    c: Perpendicular(g0,g5)
    c: Perpendicular(g4,g5)
    c: Distance(g0) = 30
    c: PointOnObject(g6,g-1)
    c: Coincident(g6,g0)
    c: Parallel(g6,g5)
    c: Distance(g5) = 9
    c: Coincident(g7,g1)
    c: Horizontal(g7)
    c: Coincident(g8,g7)
    c: Coincident(g4,g8)
    c: Parallel(g6,g8)
    c: DistanceX(g7,g7) = 1
    c: Distance(g6) = 12.5
    c: Coincident(g9,g2)
    c: Coincident(g9,g3)
    c: Angle(g9,g3) = 2.35619
    c: Horizontal(g3)
    c: Coincident(g10,g6)
    c: Parallel(g10,g6)
    c: DistanceX(g-1,g6) = 3
    c: Angle(g8,g7) = 2.56563
    c: DistanceY(g3,g-1) = 10.5
    c: Coincident(g3,g10)
    c: DistanceX(g1,g-1) = 10
    c: DistanceY(g2,g-1) = 12.5
FEATURE [PartDesign::Pad] Pad160
  Direction = (0,0,1)
  Length = 2.5
  Length2 = 10
  Profile = -> Sketch341
  ReferenceAxis = -> Sketch341 [N_Axis]
  Suppressed = false
  Type = 0
FEATURE [PartDesign::Pocket] Pocket153
  BaseFeature = -> Pad160
  Direction = (1e-16,-2e-16,-1)
  Length = 5
  Length2 = 5
  Profile = -> Binder058
  Reversed = true
  Suppressed = false
  Type = 1
FEATURE [Sketcher::SketchObject] Sketch342
  ArcFitTolerance = 0
  AttachmentSupport = -> [Pocket153]
  ExternalGeometry = -> [Pocket153]
  FullyConstrained = true
  MakeInternals = false
  MapMode = 5
  Placement = pos=(0,-12.5,0) rot=(1,0,0;1.5708rad)
  sketch-geometry (7):
    g0: LineSegment StartX=-18 StartY=4 StartZ=0 EndX=-10 EndY=4 EndZ=0
    g1: LineSegment StartX=-10 StartY=4 StartZ=0 EndX=-10 EndY=-4 EndZ=0
    g2: LineSegment StartX=-10 StartY=-4 StartZ=0 EndX=-18 EndY=-4 EndZ=0
    g3: LineSegment StartX=-18 StartY=-4 StartZ=0 EndX=-18 EndY=4 EndZ=0
    g4: Circle CenterX=-14 CenterY=5.46461e-11 CenterZ=0 NormalX=0 NormalY=0 NormalZ=1 AngleXU=0 Radius=2.5
    g5: LineSegment [constr] StartX=-10 StartY=-4 StartZ=0 EndX=-14 EndY=5.46461e-11 EndZ=0
    g6: LineSegment [constr] StartX=-14 StartY=5.46461e-11 StartZ=0 EndX=-18 EndY=-4 EndZ=0
  constraints (19):
    c: Coincident(g0,g1)
    c: Coincident(g1,g2)
    c: Coincident(g2,g3)
    c: Coincident(g3,g0)
    c: Horizontal(g0)
    c: Horizontal(g2)
    c: Vertical(g1)
    c: Vertical(g3)
    c: PointOnObject(g-3,g1)
    c: Equal(g3,g0)
    c: DistanceY(g2,g-3) = 6.5
    c: Diameter(g4) = 5
    c: Coincident(g5,g1)
    c: Coincident(g5,g4)
    c: Coincident(g6,g4)
    c: Coincident(g6,g2)
    c: Equal(g6,g5)
    c: Perpendicular(g5,g6)
    c: DistanceX(g2,g2) = 8
FEATURE [PartDesign::Pad] Pad161
  BaseFeature = -> Pocket153
  Direction = (0,-1,2e-16)
  Length = 5
  Length2 = 10
  Profile = -> Sketch342
  ReferenceAxis = -> Sketch342 [N_Axis]
  Suppressed = false
  Type = 0
FEATURE [PartDesign::Body] Body121  label="Roll left support001"
  AllowCompound = false
  Group = -> [Sketch341,Pad160,Binder058,Pocket153,Sketch342,Pad161]
  Origin = -> Origin405
  Placement = pos=(-62,48,1) rot=(0,0,1;0rad)
  Tip = -> Pad161
FEATURE [Part::FeaturePython] Tube001  # WARN: FeaturePython — macro-defined, semantics opaque (R4)
  AttacherType = Attacher::AttachEngine3D
  Height = 14
  InnerRadius = 6
  OuterRadius = 10
  Placement = pos=(-76,7,1) rot=(1,0,0;1.5708rad)
FEATURE [Part::Cut] Cut
  Base = -> Body035
  Tool = -> Tube001
FEATURE [Sketcher::SketchObject] Sketch343
  ArcFitTolerance = 0
  FullyConstrained = false
  MakeInternals = false
  MapMode = 5
  Placement = pos=(0,-6,0) rot=(1,0,0;1.5708rad)
  sketch-geometry (7):
    g0: LineSegment StartX=-18 StartY=6.5 StartZ=0 EndX=-10 EndY=6.5 EndZ=0
    g1: LineSegment StartX=-10 StartY=6.5 StartZ=0 EndX=-10 EndY=-1.5 EndZ=0
    g2: LineSegment StartX=-10 StartY=-1.5 StartZ=0 EndX=-18 EndY=-1.5 EndZ=0
    g3: LineSegment StartX=-18 StartY=-1.5 StartZ=0 EndX=-18 EndY=6.5 EndZ=0
    g4: Circle CenterX=-14 CenterY=2.5 CenterZ=0 NormalX=0 NormalY=0 NormalZ=1 AngleXU=0 Radius=2.5
    g5: LineSegment [constr] StartX=-18 StartY=6.5 StartZ=0 EndX=-14 EndY=2.5 EndZ=0
    g6: LineSegment [constr] StartX=-14 StartY=2.5 StartZ=0 EndX=-10 EndY=-1.5 EndZ=0
  constraints (17):
    c: Coincident(g0,g1)
    c: Coincident(g1,g2)
    c: Coincident(g2,g3)
    c: Coincident(g3,g0)
    c: Horizontal(g0)
    c: Horizontal(g2)
    c: Vertical(g1)
    c: Vertical(g3)
    c: Equal(g2,g1)
    c: Diameter(g4) = 5
    c: Coincident(g5,g0)
    c: Coincident(g5,g4)
    c: Coincident(g6,g4)
    c: Coincident(g6,g1)
    c: Parallel(g5,g6)
    c: Equal(g5,g6)
    c: DistanceX(g2,g2) = 8
FEATURE [PartDesign::Pad] Pad162
  BaseFeature = -> Pad115
  Direction = (0,-1,0)
  Length = 5
  Length2 = 10
  Profile = -> Sketch343
  ReferenceAxis = -> Sketch343 [N_Axis]
  Suppressed = false
  Type = 0
FEATURE [PartDesign::SubShapeBinder] Binder059
  BindCopyOnChange = 0
  BindMode = 0
  ClaimChildren = false
  Context = -> Part011 [Body099.Binder059.]
  Fuse = false
  MakeFace = true
  OffsetFill = false
  OffsetIntersection = false
  OffsetJoinType = 0
  OffsetOpenResult = false
  PartialLoad = false
  Relative = true
  Support = -> [Part003[Part008.Body041.Pocket036.Sketch098.]]
  _Version = 2
FEATURE [PartDesign::Pocket] Pocket154
  BaseFeature = -> Pad162
  Direction = (0,0,-1)
  Length = 5
  Length2 = 5
  Profile = -> Binder059
  Suppressed = false
  Type = 1
FEATURE [PartDesign::Body] Body099  label="Roll right support001"
  AllowCompound = false
  Group = -> [Sketch278,Pad115,Sketch343,Pad162,Binder059,Pocket154]
  Origin = -> Origin365
  Placement = pos=(-62,-48,3.5) rot=(1,0,0;3.14159rad)
  Tip = -> Pocket154
FEATURE [App::Part] Part011  label="Dribbler"
  Group = -> [Body034,Body050,Body099,Body121,Body035,Cut,Tube001]
  Origin = -> Origin236
  Placement = pos=(4,0,1) rot=(0,0,1;0rad)
FEATURE [Part::Feature] Part__Feature442  label="114-00841-68--3DModel-STEP-56544 v004"
  Placement = pos=(24.0935,-0.00012972,0.814608) rot=(0.57735,0.57735,0.57735;2.0944rad)
  shape: bbox 10 x 11.95 x 1.48 mm, 267 faces (baked)
FEATURE [App::Part] _14_00841_68__3DModel_STEP_56544_v1  label="114-00841-68--3DModel-STEP-56544 v015"
  Group = -> [Part__Feature439,Part__Feature442]
  Origin = -> Origin052
FEATURE [App::Part] Teensy4_1_v22  label="Teensy 4.1 "
  Group = -> [_14_00841_68__3DModel_STEP_56544_v1,MIMXRT1052CVJ5B_v1,Part__Feature589,Pin_Header_1x6_TH_Pitch_2_54mm_v1,Pin_Header_1x6_TH_Pitch_2_54mm_v002,Pin_Header_1x6_TH_Pitch_2_54mm_v003,Pin_Header_1x6_TH_Pitch_2_54mm_v004,Pin_Header_1x6_TH_Pitch_2_54mm_v1_Mirror_,Pin_Header_1x6_TH_Pitch_2_54mm_v1_Mirror_001,Pin_Header_1x6_TH_Pitch_2_54mm_v1_Mirror_002,Pin_Header_1x6_TH_Pitch_2_54mm_v1_Mirror_003,+2 more]
  Origin = -> Origin050
  Placement = pos=(33.7332,-0.281902,31) rot=(0,0,-1;4.71239rad)
FEATURE [App::Part] Part  label="Main PCB"
  Group = -> [Body024,Teensy4_1_v22,HC05_Modulo]
  Origin = -> Origin077
  Placement = pos=(0,0,-8) rot=(0,0,1;0rad)
FEATURE [Sketcher::SketchObject] Sketch344
  ArcFitTolerance = 1e-06
  AttachmentSupport = -> [XY_Plane]
  FullyConstrained = true
  MakeInternals = false
  MapMode = 5
  sketch-geometry (40):
    g0: LineSegment StartX=-47.2844 StartY=55.9941 StartZ=0 EndX=-53.0811 EndY=47.8707 EndZ=0
    g1: LineSegment StartX=78.3537 StartY=-34.8975 StartZ=0 EndX=72.4894 EndY=-42.9975 EndZ=0
    g2: LineSegment [constr] StartX=-46.1068 StartY=49.0364 StartZ=0 EndX=71.3716 EndY=-36.0154 EndZ=0
    g3: LineSegment [constr] StartX=-46.0969 StartY=-49.074 StartZ=0 EndX=71.3517 EndY=35.9432 EndZ=0
    g4: GeomPoint [constr] X=0 Y=0 Z=0
    g5: LineSegment StartX=72.4793 StartY=43.0129 StartZ=0 EndX=78.356 EndY=34.8943 EndZ=0
    g6: LineSegment StartX=-52.9931 StartY=-48.0742 StartZ=0 EndX=-47.1295 EndY=-56.1747 EndZ=0
    g7: LineSegment StartX=-34.9875 StartY=34.9595 StartZ=0 EndX=-34.9875 EndY=-35.0405 EndZ=0
    g8: GeomPoint [constr] X=0 Y=0 Z=0
    g9: GeomPoint X=-17.9084 Y=-35.0225 Z=0
    g10: GeomPoint X=-17.9205 Y=35.0405 Z=0
    g11: GeomPoint X=34.9875 Y=15.8738 Z=0
    g12: GeomPoint X=34.9875 Y=3.50131 Z=0
    g13: GeomPoint X=34.9875 Y=-3.50131 Z=0
    g14: GeomPoint X=34.9997 Y=-15.8557 Z=0
    g15: LineSegment StartX=-47.2844 StartY=55.9941 StartZ=0 EndX=-17.9205 EndY=35.0405 EndZ=0
    g16: LineSegment StartX=34.9875 StartY=-3.50131 StartZ=0 EndX=78.3537 EndY=-34.8975 EndZ=0
    g17: LineSegment StartX=-17.9205 StartY=35.0405 StartZ=0 EndX=34.9875 EndY=35.0405 EndZ=0
    g18: LineSegment StartX=-17.9084 StartY=-35.0225 StartZ=0 EndX=34.9997 EndY=-35.0225 EndZ=0
    g19: LineSegment StartX=34.9997 StartY=-35.0225 StartZ=0 EndX=34.9997 EndY=-15.8557 EndZ=0
    g20: LineSegment StartX=34.9875 StartY=-3.50131 StartZ=0 EndX=34.9875 EndY=3.50131 EndZ=0
    g21: LineSegment StartX=34.9875 StartY=15.8738 StartZ=0 EndX=34.9875 EndY=35.0405 EndZ=0
    g22: LineSegment StartX=-53.0811 StartY=47.8707 StartZ=0 EndX=-34.9875 EndY=34.9595 EndZ=0
    g23: LineSegment StartX=34.9997 StartY=-15.8557 StartZ=0 EndX=72.4894 EndY=-42.9975 EndZ=0
    g24: LineSegment StartX=34.9875 StartY=15.8738 StartZ=0 EndX=72.4793 EndY=43.0129 EndZ=0
    g25: LineSegment StartX=-52.9931 StartY=-48.0742 StartZ=0 EndX=-34.9875 EndY=-35.0405 EndZ=0
    g26: LineSegment StartX=-47.1295 StartY=-56.1747 StartZ=0 EndX=-17.9084 EndY=-35.0225 EndZ=0
    g27: LineSegment StartX=34.9875 StartY=3.50131 StartZ=0 EndX=78.356 EndY=34.8943 EndZ=0
    g28: Circle CenterX=-46.0969 CenterY=-49.074 CenterZ=0 NormalX=0 NormalY=0 NormalZ=1 AngleXU=0 Radius=2
    g29: Circle CenterX=-46.1068 CenterY=49.0364 CenterZ=0 NormalX=0 NormalY=0 NormalZ=1 AngleXU=0 Radius=2
    g30: Circle CenterX=71.3517 CenterY=35.9432 CenterZ=0 NormalX=0 NormalY=0 NormalZ=1 AngleXU=0 Radius=2
    g31: Circle CenterX=71.3716 CenterY=-36.0154 CenterZ=0 NormalX=0 NormalY=0 NormalZ=1 AngleXU=0 Radius=2
    g32: GeomPoint [constr] X=0 Y=0 Z=0
    g33: LineSegment [constr] StartX=-15.026 StartY=15.026 StartZ=0 EndX=15.026 EndY=-15.026 EndZ=0
    g34: LineSegment [constr] StartX=15.026 StartY=15.026 StartZ=0 EndX=-15.026 EndY=-15.026 EndZ=0
    g35: GeomPoint [constr] X=0 Y=0 Z=0
    g36: Circle CenterX=-15.026 CenterY=15.026 CenterZ=0 NormalX=0 NormalY=0 NormalZ=1 AngleXU=0 Radius=1.5
    g37: Circle CenterX=15.026 CenterY=15.026 CenterZ=0 NormalX=0 NormalY=0 NormalZ=1 AngleXU=0 Radius=1.5
    g38: Circle CenterX=15.026 CenterY=-15.026 CenterZ=0 NormalX=0 NormalY=0 NormalZ=1 AngleXU=0 Radius=1.5
    g39: Circle CenterX=-15.026 CenterY=-15.026 CenterZ=0 NormalX=0 NormalY=0 NormalZ=1 AngleXU=0 Radius=1.5
  constraints (86):
    c: Distance(g0,g1) = 155
    c: Block(g2)
    c: Block(g3)
    c: Distance(g1) = 10
    c: Distance(g2,g1) = 5
    c: Coincident(g4,g-1)
    c: Distance(g6) = 10
    c: Distance(g3,g6) = 5
    c: Vertical(g7)
    c: Symmetric(g17,g7,g8)
    c: DistanceY(g7,g7) = 70
    c: Coincident(g8,g4)
    c: Coincident(g15,g0)
    c: Coincident(g15,g10)
    c: Coincident(g17,g10)
    c: Horizontal(g17)
    c: Coincident(g18,g9)
    c: Horizontal(g18)
    c: Coincident(g19,g18)
    c: Coincident(g19,g14)
    c: Vertical(g19)
    c: Coincident(g20,g13)
    c: Coincident(g20,g12)
    c: Coincident(g21,g11)
    c: Coincident(g21,g17)
    c: Vertical(g21)
    c: Coincident(g22,g0)
    c: Coincident(g22,g7)
    c: Coincident(g23,g14)
    c: Coincident(g23,g1)
    c: Coincident(g24,g11)
    c: Coincident(g24,g5)
    c: Coincident(g25,g6)
    c: Coincident(g25,g7)
    c: Coincident(g26,g6)
    c: Coincident(g26,g9)
    c: Perpendicular(g5,g24)
    c: Perpendicular(g15,g0)
    c: Coincident(g13,g16)
    c: Coincident(g1,g16)
    c: Perpendicular(g1,g16)
    c: Perpendicular(g1,g23)
    c: Perpendicular(g6,g26)
    c: Perpendicular(g25,g6)
    c: Perpendicular(g0,g22)
    c: Coincident(g12,g27)
    c: Coincident(g5,g27)
    c: Equal(g17,g18)
    c: Equal(g19,g21)
    c: Perpendicular(g5,g27)
    c: Equal(g24,g23)
    c: Equal(g27,g16)
    c: Equal(g15,g26)
    c: Equal(g25,g22)
    c: Symmetric(g13,g12,g-1)
    c: Parallel(g16,g2)
    c: Parallel(g27,g3)
    c: Distance(g2,g22) = 5
    c: Distance(g2,g0) = 5
    c: Vertical(g17,g12)
    c: Parallel(g3,g26)
    c: Distance(g2,g23) = 5
    c: Diameter(g28) = 4
    c: Coincident(g28,g3)
    c: Diameter(g29) = 4
    c: Coincident(g29,g2)
    c: Diameter(g30) = 4
    c: Coincident(g30,g3)
    c: Diameter(g31) = 4
    c: Coincident(g31,g2)
    c: Coincident(g32,g4)
    c: Angle(g-1,g33) = 2.35619
    c: Perpendicular(g33,g34)
    c: Equal(g33,g34)
    c: Distance(g34) = 42.5
    c: Symmetric(g33,g33,g4)
    c: Symmetric(g34,g34,g4)
    c: Coincident(g35,g4)
    c: Diameter(g36) = 3
    c: Coincident(g36,g33)
    c: Diameter(g37) = 3
    c: Coincident(g37,g34)
    c: Diameter(g38) = 3
    c: Coincident(g38,g33)
    c: Diameter(g39) = 3
    c: Coincident(g39,g34)
FEATURE [PartDesign::Pad] Pad163
  Direction = (0,0,1)
  Length = 4
  Length2 = 10
  Profile = -> Sketch344
  ReferenceAxis = -> Sketch344 [N_Axis]
  Refine = true
  Suppressed = false
  Type = 0
FEATURE [Part::Feature] Part__Feature  label="Raspberry Pi HQ Camera v2"
  shape: bbox 38 x 1.4 x 38 mm, 22 faces (baked)
FEATURE [Part::Feature] Part__Feature2033  label="Raspberry Pi HQ Camera v003"
  shape: bbox 24 x 10.2 x 16.01 mm, 96 faces (baked)
FEATURE [Part::Feature] Part__Feature2034  label="Raspberry Pi HQ Camera v004"
  shape: bbox 24 x 1.5 x 5.408 mm, 8 faces (baked)
FEATURE [Part::Feature] Part__Feature2035  label="Raspberry Pi HQ Camera v005"
  shape: bbox 37.4 x 11.72 x 40.15 mm, 140 faces (baked)
FEATURE [Part::Feature] Part__Feature2036  label="Raspberry Pi HQ Camera v006"
  shape: bbox 30.65 x 13.45 x 30.65 mm, 91 faces (baked)
FEATURE [Part::Feature] Part__Feature2037  label="Raspberry Pi HQ Camera v007"
  shape: bbox 6.5 x 1 x 4.5 mm, 6 faces (baked)
FEATURE [Part::Feature] Part__Feature2038  label="Raspberry Pi HQ Camera v008"
  shape: bbox 7.5 x 0.5 x 5.5 mm, 6 faces (baked)
FEATURE [App::Part] Raspberry_Pi_HQ_Camera_v2  label="Raspberry Pi HQ Camera v009"
  Group = -> [Part__Feature,Part__Feature2033,Part__Feature2034,Part__Feature2035,Part__Feature2036,Part__Feature2037,Part__Feature2038]
  Origin = -> Origin406
  Placement = pos=(-19,-19,124.5) rot=(1,0,0;4.71239rad)
FEATURE [Sketcher::SketchObject] Sketch345
  ArcFitTolerance = 1e-06
  AttachmentSupport = -> [Pad163]
  ExternalGeometry = -> [Pad163]
  FullyConstrained = false
  MakeInternals = false
  MapMode = 5
  Placement = pos=(0,0,0) rot=(1,0,0;3.14159rad)
  sketch-geometry (28):
    g0: LineSegment StartX=-42.3609 StartY=47.6448 StartZ=0 EndX=-42.9912 EndY=51.5948 EndZ=0
    g1: LineSegment StartX=-42.9912 StartY=51.5948 StartZ=0 EndX=-46.7271 EndY=53.0241 EndZ=0
    g2: LineSegment StartX=-46.7271 StartY=53.0241 StartZ=0 EndX=-49.8329 EndY=50.5032 EndZ=0
    g3: LineSegment StartX=-49.8329 StartY=50.5032 StartZ=0 EndX=-49.2026 EndY=46.5532 EndZ=0
    g4: LineSegment StartX=-49.2026 StartY=46.5532 StartZ=0 EndX=-45.4667 EndY=45.124 EndZ=0
    g5: LineSegment StartX=-45.4667 StartY=45.124 StartZ=0 EndX=-42.3609 EndY=47.6448 EndZ=0
    g6: Circle [constr] CenterX=-46.0969 CenterY=49.074 CenterZ=0 NormalX=0 NormalY=0 NormalZ=1 AngleXU=0 Radius=4
    g7: LineSegment StartX=75.1606 StartY=34.7334 StartZ=0 EndX=74.3763 EndY=38.6558 EndZ=0
    g8: LineSegment StartX=74.3763 StartY=38.6558 StartZ=0 EndX=70.5873 EndY=39.9378 EndZ=0
    g9: LineSegment StartX=70.5873 StartY=39.9378 StartZ=0 EndX=67.5826 EndY=37.2974 EndZ=0
    g10: LineSegment StartX=67.5826 StartY=37.2974 StartZ=0 EndX=68.3668 EndY=33.375 EndZ=0
    g11: LineSegment StartX=68.3668 StartY=33.375 StartZ=0 EndX=72.1558 EndY=32.093 EndZ=0
    g12: LineSegment StartX=72.1558 StartY=32.093 StartZ=0 EndX=75.1606 EndY=34.7334 EndZ=0
    g13: Circle [constr] CenterX=71.3716 CenterY=36.0154 CenterZ=0 NormalX=0 NormalY=0 NormalZ=1 AngleXU=0 Radius=4
    g14: LineSegment StartX=75.176 StartY=-37.1157 StartZ=0 EndX=74.2792 EndY=-33.2175 EndZ=0
    g15: LineSegment StartX=74.2792 StartY=-33.2175 StartZ=0 EndX=70.4549 EndY=-32.045 EndZ=0
    g16: LineSegment StartX=70.4549 StartY=-32.045 StartZ=0 EndX=67.5274 EndY=-34.7707 EndZ=0
    g17: LineSegment StartX=67.5274 StartY=-34.7707 StartZ=0 EndX=68.4242 EndY=-38.6689 EndZ=0
    g18: LineSegment StartX=68.4242 StartY=-38.6689 StartZ=0 EndX=72.2485 EndY=-39.8414 EndZ=0
    g19: LineSegment StartX=72.2485 StartY=-39.8414 StartZ=0 EndX=75.176 EndY=-37.1157 EndZ=0
    g20: Circle [constr] CenterX=71.3517 CenterY=-35.9432 CenterZ=0 NormalX=0 NormalY=0 NormalZ=1 AngleXU=0 Radius=4
    g21: LineSegment StartX=-42.2176 StartY=-49.9713 StartZ=0 EndX=-43.3526 EndY=-46.1357 EndZ=0
    g22: LineSegment StartX=-43.3526 StartY=-46.1357 StartZ=0 EndX=-47.2418 EndY=-45.2008 EndZ=0
    g23: LineSegment StartX=-47.2418 StartY=-45.2008 StartZ=0 EndX=-49.996 EndY=-48.1016 EndZ=0
    g24: LineSegment StartX=-49.996 StartY=-48.1016 StartZ=0 EndX=-48.861 EndY=-51.9372 EndZ=0
    g25: LineSegment StartX=-48.861 StartY=-51.9372 StartZ=0 EndX=-44.9718 EndY=-52.872 EndZ=0
    g26: LineSegment StartX=-44.9718 StartY=-52.872 StartZ=0 EndX=-42.2176 EndY=-49.9713 EndZ=0
    g27: Circle [constr] CenterX=-46.1068 CenterY=-49.0364 CenterZ=0 NormalX=0 NormalY=0 NormalZ=1 AngleXU=0 Radius=4
  constraints (60):
    c: Coincident(g0,g1)
    c: Coincident(g1,g2)
    c: Coincident(g2,g3)
    c: Coincident(g3,g4)
    c: Coincident(g4,g5)
    c: Coincident(g5,g0)
    c: Equal(g0, g1-g5) x5
    c: PointOnObject(g0,g6)
    c: PointOnObject(g1,g6)
    c: PointOnObject(g2,g6)
    c: PointOnObject(g3,g6)
    c: PointOnObject(g4,g6)
    c: PointOnObject(g5,g6)
    c: Coincident(g6,g-3)
    c: Coincident(g7,g8)
    c: Coincident(g8,g9)
    c: Coincident(g9,g10)
    c: Coincident(g10,g11)
    c: Coincident(g11,g12)
    c: Coincident(g12,g7)
    c: Equal(g7, g8-g12) x5
    c: PointOnObject(g7,g13)
    c: PointOnObject(g8,g13)
    c: PointOnObject(g9,g13)
    c: PointOnObject(g10,g13)
    c: PointOnObject(g11,g13)
    c: PointOnObject(g12,g13)
    c: Coincident(g13,g-7)
    c: Coincident(g14,g15)
    c: Coincident(g15,g16)
    c: Coincident(g16,g17)
    c: Coincident(g17,g18)
    c: Coincident(g18,g19)
    c: Coincident(g19,g14)
    c: Equal(g14, g15-g19) x5
    c: PointOnObject(g14,g20)
    c: PointOnObject(g15,g20)
    c: PointOnObject(g16,g20)
    c: PointOnObject(g17,g20)
    c: PointOnObject(g18,g20)
    c: PointOnObject(g19,g20)
    c: Coincident(g20,g-6)
    c: Coincident(g21,g22)
    c: Coincident(g22,g23)
    c: Coincident(g23,g24)
    c: Coincident(g24,g25)
    c: Coincident(g25,g26)
    c: Coincident(g26,g21)
    c: Equal(g21, g22-g26) x5
    c: PointOnObject(g21,g27)
    c: PointOnObject(g22,g27)
    c: PointOnObject(g23,g27)
    c: PointOnObject(g24,g27)
    c: PointOnObject(g25,g27)
    c: PointOnObject(g26,g27)
    c: Coincident(g27,g-5)
    c: Diameter(g6) = 8
    c: Diameter(g13) = 8
    c: Diameter(g20) = 8
    c: Diameter(g27) = 8
FEATURE [PartDesign::Pad] Pad164
  BaseFeature = -> Pad163
  Direction = (0,0,-1)
  Length = 124
  Length2 = 10
  Profile = -> Sketch345
  ReferenceAxis = -> Sketch345 [N_Axis]
  Refine = true
  Suppressed = false
  Type = 0
FEATURE [PartDesign::Body] Body122  label="Nouveau support caméra"
  AllowCompound = false
  Group = -> [Sketch344,Pad163,Sketch345,Pad164]
  Origin = -> Origin
  Placement = pos=(0,0,126) rot=(0,0,1;0rad)
  Tip = -> Pad164
